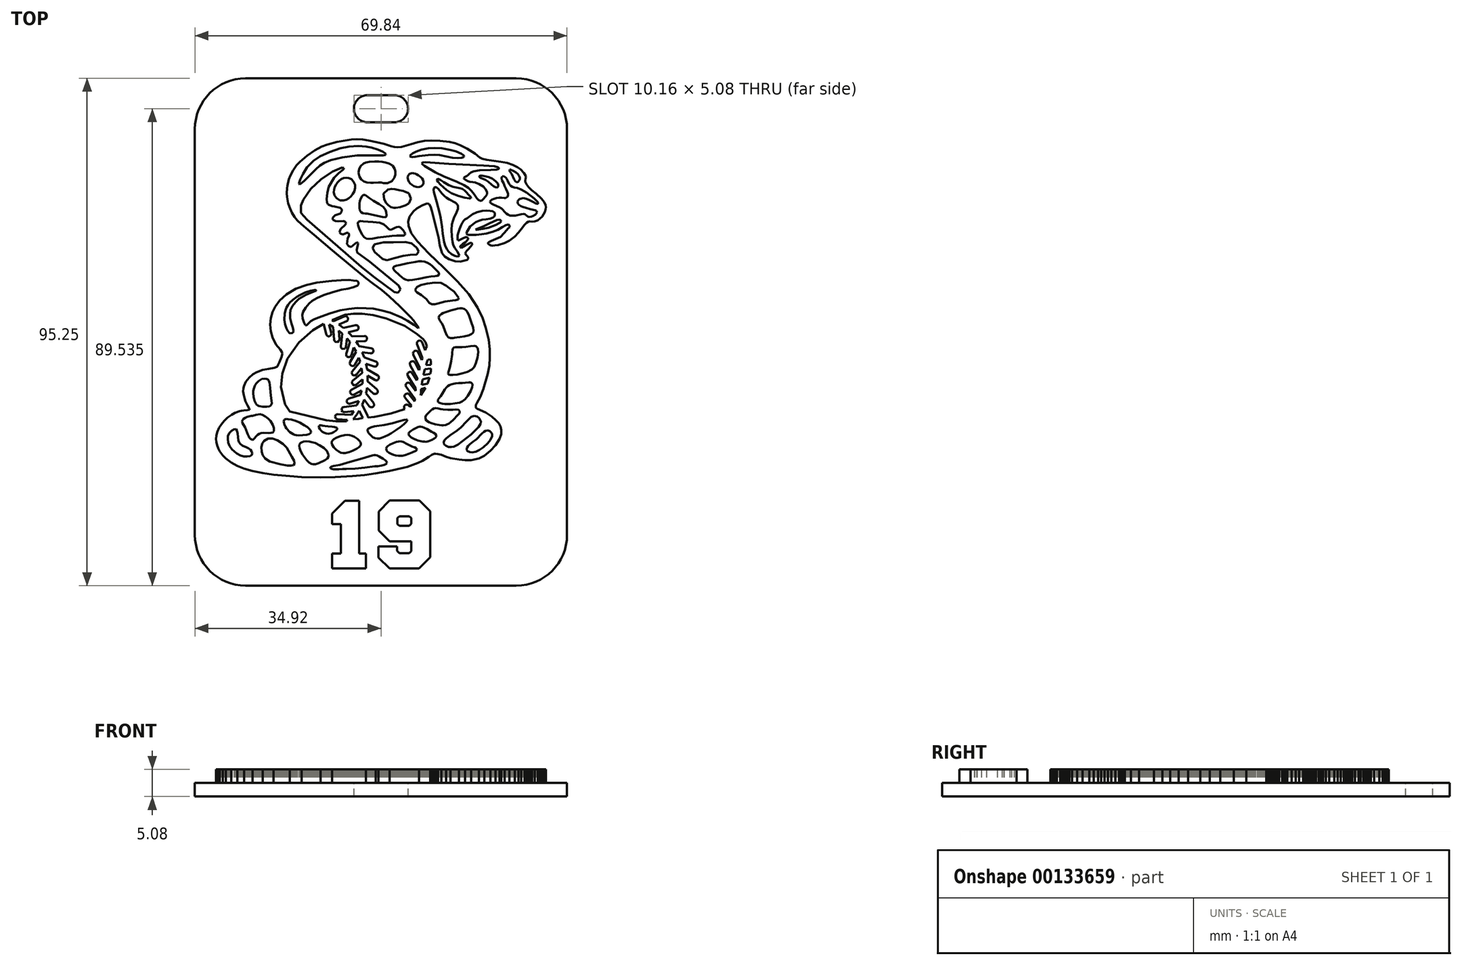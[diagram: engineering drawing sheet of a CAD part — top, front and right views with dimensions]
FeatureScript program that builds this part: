
annotation { "Feature Type Name" : "Feature", "Feature Type Description" : "" }
export const myFeature = defineFeature(function(context is Context, id is Id, definition is map)
    precondition{}
    {
        {
            var Q0;
            Q0=qCreatedBy(makeId("Top.planeOp"),FACE);
            var sketch = newSketch(context, id + "F0", { "sketchPlane" : qUnion([Q0])});
            skLineSegment(sketch, "E0", {"start": v(-10.1, 30.77) * mm, "end": v(-11.14, 30.36) * mm});
            skLineSegment(sketch, "E1", {"start": v(-11.14, 30.36) * mm, "end": v(-12.42, 29.65) * mm});
            skLineSegment(sketch, "E2", {"start": v(-12.42, 29.65) * mm, "end": v(-13.87, 28.65) * mm});
            skLineSegment(sketch, "E3", {"start": v(-13.87, 28.65) * mm, "end": v(-15.23, 27.49) * mm});
            skLineSegment(sketch, "E4", {"start": v(-15.23, 27.49) * mm, "end": v(-15.83, 26.85) * mm});
            skLineSegment(sketch, "E5", {"start": v(-15.83, 26.85) * mm, "end": v(-16.5, 25.91) * mm});
            skLineSegment(sketch, "E6", {"start": v(-16.5, 25.91) * mm, "end": v(-16.99, 24.99) * mm});
            skLineSegment(sketch, "E7", {"start": v(-16.99, 24.99) * mm, "end": v(-17.29, 24.2) * mm});
            skLineSegment(sketch, "E8", {"start": v(-17.29, 24.2) * mm, "end": v(-17.57, 23.01) * mm});
            skLineSegment(sketch, "E9", {"start": v(-17.57, 23.01) * mm, "end": v(-17.63, 22.55) * mm});
            skLineSegment(sketch, "E10", {"start": v(-17.63, 22.55) * mm, "end": v(-17.67, 21.62) * mm});
            skLineSegment(sketch, "E11", {"start": v(-17.67, 21.62) * mm, "end": v(-17.63, 20.87) * mm});
            skLineSegment(sketch, "E12", {"start": v(-17.63, 20.87) * mm, "end": v(-17.43, 19.76) * mm});
            skLineSegment(sketch, "E13", {"start": v(-17.43, 19.76) * mm, "end": v(-17.2, 19.03) * mm});
            skLineSegment(sketch, "E14", {"start": v(-17.2, 19.03) * mm, "end": v(-16.74, 17.98) * mm});
            skLineSegment(sketch, "E15", {"start": v(-16.74, 17.98) * mm, "end": v(-16.21, 17.14) * mm});
            skLineSegment(sketch, "E16", {"start": v(-16.21, 17.14) * mm, "end": v(-15.69, 16.5) * mm});
            skLineSegment(sketch, "E17", {"start": v(-15.69, 16.5) * mm, "end": v(-14.95, 15.79) * mm});
            skLineSegment(sketch, "E18", {"start": v(-14.95, 15.79) * mm, "end": v(-14.07, 15.06) * mm});
            skLineSegment(sketch, "E19", {"start": v(-14.07, 15.06) * mm, "end": v(-12.56, 13.8) * mm});
            skLineSegment(sketch, "E20", {"start": v(-12.56, 13.8) * mm, "end": v(-9.09, 10.85) * mm});
            skLineSegment(sketch, "E21", {"start": v(-9.09, 10.85) * mm, "end": v(-5.34, 7.75) * mm});
            skLineSegment(sketch, "E22", {"start": v(-5.34, 7.75) * mm, "end": v(-2.8, 5.63) * mm});
            skLineSegment(sketch, "E23", {"start": v(-2.8, 5.63) * mm, "end": v(-1.5, 4.63) * mm});
            skLineSegment(sketch, "E24", {"start": v(-1.5, 4.63) * mm, "end": v(0.14, 3.4) * mm});
            skLineSegment(sketch, "E25", {"start": v(0.14, 3.4) * mm, "end": v(1.56, 2.21) * mm});
            skLineSegment(sketch, "E26", {"start": v(1.56, 2.21) * mm, "end": v(3.52, 0.38) * mm});
            skLineSegment(sketch, "E27", {"start": v(3.52, 0.38) * mm, "end": v(5.55, -1.66) * mm});
            skLineSegment(sketch, "E28", {"start": v(5.55, -1.66) * mm, "end": v(6.1, -2.3) * mm});
            skLineSegment(sketch, "E29", {"start": v(6.1, -2.3) * mm, "end": v(6.85, -3.29) * mm});
            skLineSegment(sketch, "E30", {"start": v(6.85, -3.29) * mm, "end": v(7.08, -3.6) * mm});
            skLineSegment(sketch, "E31", {"start": v(7.08, -3.6) * mm, "end": v(7.04, -3.72) * mm});
            skLineSegment(sketch, "E32", {"start": v(7.04, -3.72) * mm, "end": v(6.17, -3.08) * mm});
            skLineSegment(sketch, "E33", {"start": v(6.17, -3.08) * mm, "end": v(5, -2.32) * mm});
            skLineSegment(sketch, "E34", {"start": v(5, -2.32) * mm, "end": v(3.8, -1.71) * mm});
            skLineSegment(sketch, "E35", {"start": v(3.8, -1.71) * mm, "end": v(1.73, -0.85) * mm});
            skLineSegment(sketch, "E36", {"start": v(1.73, -0.85) * mm, "end": v(0.03, -0.35) * mm});
            skLineSegment(sketch, "E37", {"start": v(0.03, -0.35) * mm, "end": v(-1.46, -0.09) * mm});
            skLineSegment(sketch, "E38", {"start": v(-1.46, -0.09) * mm, "end": v(-2.78, 0.03) * mm});
            skLineSegment(sketch, "E39", {"start": v(-2.78, 0.03) * mm, "end": v(-4.43, 0.04) * mm});
            skLineSegment(sketch, "E40", {"start": v(-4.43, 0.04) * mm, "end": v(-6.07, -0.1) * mm});
            skLineSegment(sketch, "E41", {"start": v(-6.07, -0.1) * mm, "end": v(-7.66, -0.38) * mm});
            skLineSegment(sketch, "E42", {"start": v(-7.66, -0.38) * mm, "end": v(-9.54, -0.94) * mm});
            skLineSegment(sketch, "E43", {"start": v(-9.54, -0.94) * mm, "end": v(-11.87, -1.75) * mm});
            skLineSegment(sketch, "E44", {"start": v(-11.87, -1.75) * mm, "end": v(-12.63, -2.07) * mm});
            skLineSegment(sketch, "E45", {"start": v(-12.63, -2.07) * mm, "end": v(-13.17, -2.43) * mm});
            skLineSegment(sketch, "E46", {"start": v(-13.17, -2.43) * mm, "end": v(-13.62, -2.86) * mm});
            skLineSegment(sketch, "E47", {"start": v(-13.62, -2.86) * mm, "end": v(-13.87, -3.09) * mm});
            skLineSegment(sketch, "E48", {"start": v(-13.87, -3.09) * mm, "end": v(-14.01, -3.2) * mm});
            skLineSegment(sketch, "E49", {"start": v(-14.01, -3.2) * mm, "end": v(-14.19, -3.17) * mm});
            skLineSegment(sketch, "E50", {"start": v(-14.19, -3.17) * mm, "end": v(-14.43, -2.69) * mm});
            skLineSegment(sketch, "E51", {"start": v(-14.43, -2.69) * mm, "end": v(-14.7, -1.9) * mm});
            skLineSegment(sketch, "E52", {"start": v(-14.7, -1.9) * mm, "end": v(-14.77, -1.3) * mm});
            skLineSegment(sketch, "E53", {"start": v(-14.77, -1.3) * mm, "end": v(-14.64, -0.72) * mm});
            skLineSegment(sketch, "E54", {"start": v(-14.64, -0.72) * mm, "end": v(-14.15, 0.15) * mm});
            skLineSegment(sketch, "E55", {"start": v(-14.15, 0.15) * mm, "end": v(-13.5, 0.87) * mm});
            skLineSegment(sketch, "E56", {"start": v(-13.5, 0.87) * mm, "end": v(-12.9, 1.37) * mm});
            skLineSegment(sketch, "E57", {"start": v(-12.9, 1.37) * mm, "end": v(-12.05, 1.9) * mm});
            skLineSegment(sketch, "E58", {"start": v(-12.05, 1.9) * mm, "end": v(-10.74, 2.5) * mm});
            skLineSegment(sketch, "E59", {"start": v(-10.74, 2.5) * mm, "end": v(-8.96, 3.08) * mm});
            skLineSegment(sketch, "E60", {"start": v(-8.96, 3.08) * mm, "end": v(-7.41, 3.49) * mm});
            skLineSegment(sketch, "E61", {"start": v(-7.41, 3.49) * mm, "end": v(-6.2, 3.72) * mm});
            skLineSegment(sketch, "E62", {"start": v(-6.2, 3.72) * mm, "end": v(-5.24, 3.9) * mm});
            skLineSegment(sketch, "E63", {"start": v(-5.24, 3.9) * mm, "end": v(-4.44, 4.24) * mm});
            skLineSegment(sketch, "E64", {"start": v(-4.44, 4.24) * mm, "end": v(-4.2, 4.53) * mm});
            skLineSegment(sketch, "E65", {"start": v(-4.2, 4.53) * mm, "end": v(-4.24, 4.9) * mm});
            skLineSegment(sketch, "E66", {"start": v(-4.24, 4.9) * mm, "end": v(-4.48, 5.15) * mm});
            skLineSegment(sketch, "E67", {"start": v(-4.48, 5.15) * mm, "end": v(-5.2, 5.22) * mm});
            skLineSegment(sketch, "E68", {"start": v(-5.2, 5.22) * mm, "end": v(-6.02, 5.3) * mm});
            skLineSegment(sketch, "E69", {"start": v(-6.02, 5.3) * mm, "end": v(-7.46, 5.25) * mm});
            skLineSegment(sketch, "E70", {"start": v(-7.46, 5.25) * mm, "end": v(-9.22, 5.17) * mm});
            skLineSegment(sketch, "E71", {"start": v(-9.22, 5.17) * mm, "end": v(-12.06, 4.86) * mm});
            skLineSegment(sketch, "E72", {"start": v(-12.06, 4.86) * mm, "end": v(-13.96, 4.42) * mm});
            skLineSegment(sketch, "E73", {"start": v(-13.96, 4.42) * mm, "end": v(-15.95, 3.67) * mm});
            skLineSegment(sketch, "E74", {"start": v(-15.95, 3.67) * mm, "end": v(-17.73, 2.62) * mm});
            skLineSegment(sketch, "E75", {"start": v(-17.73, 2.62) * mm, "end": v(-19.03, 1.44) * mm});
            skLineSegment(sketch, "E76", {"start": v(-19.03, 1.44) * mm, "end": v(-19.86, 0.31) * mm});
            skLineSegment(sketch, "E77", {"start": v(-19.86, 0.31) * mm, "end": v(-20.36, -0.72) * mm});
            skLineSegment(sketch, "E78", {"start": v(-20.36, -0.72) * mm, "end": v(-20.7, -1.85) * mm});
            skLineSegment(sketch, "E79", {"start": v(-20.7, -1.85) * mm, "end": v(-20.78, -3.05) * mm});
            skLineSegment(sketch, "E80", {"start": v(-20.78, -3.05) * mm, "end": v(-20.65, -4.3) * mm});
            skLineSegment(sketch, "E81", {"start": v(-20.65, -4.3) * mm, "end": v(-20.33, -5.49) * mm});
            skLineSegment(sketch, "E82", {"start": v(-20.33, -5.49) * mm, "end": v(-19.72, -6.82) * mm});
            skLineSegment(sketch, "E83", {"start": v(-19.72, -6.82) * mm, "end": v(-18.9, -7.76) * mm});
            skLineSegment(sketch, "E84", {"start": v(-18.9, -7.76) * mm, "end": v(-18.56, -8.24) * mm});
            skLineSegment(sketch, "E85", {"start": v(-18.56, -8.24) * mm, "end": v(-18.51, -8.5) * mm});
            skLineSegment(sketch, "E86", {"start": v(-18.51, -8.5) * mm, "end": v(-18.66, -9.08) * mm});
            skLineSegment(sketch, "E87", {"start": v(-18.66, -9.08) * mm, "end": v(-19.09, -10.16) * mm});
            skLineSegment(sketch, "E88", {"start": v(-19.09, -10.16) * mm, "end": v(-19.3, -10.64) * mm});
            skLineSegment(sketch, "E89", {"start": v(-19.3, -10.64) * mm, "end": v(-19.4, -10.82) * mm});
            skLineSegment(sketch, "E90", {"start": v(-19.4, -10.82) * mm, "end": v(-19.52, -10.97) * mm});
            skLineSegment(sketch, "E91", {"start": v(-19.52, -10.97) * mm, "end": v(-20.02, -11.19) * mm});
            skLineSegment(sketch, "E92", {"start": v(-20.02, -11.19) * mm, "end": v(-21.07, -11.38) * mm});
            skLineSegment(sketch, "E93", {"start": v(-21.07, -11.38) * mm, "end": v(-22.22, -11.58) * mm});
            skLineSegment(sketch, "E94", {"start": v(-22.22, -11.58) * mm, "end": v(-23.33, -12) * mm});
            skLineSegment(sketch, "E95", {"start": v(-23.33, -12) * mm, "end": v(-24.01, -12.39) * mm});
            skLineSegment(sketch, "E96", {"start": v(-24.01, -12.39) * mm, "end": v(-24.76, -13.01) * mm});
            skLineSegment(sketch, "E97", {"start": v(-24.76, -13.01) * mm, "end": v(-25.35, -13.79) * mm});
            skLineSegment(sketch, "E98", {"start": v(-25.35, -13.79) * mm, "end": v(-25.69, -14.52) * mm});
            skLineSegment(sketch, "E99", {"start": v(-25.69, -14.52) * mm, "end": v(-25.81, -15) * mm});
            skLineSegment(sketch, "E100", {"start": v(-25.81, -15) * mm, "end": v(-25.85, -15.6) * mm});
            skLineSegment(sketch, "E101", {"start": v(-25.85, -15.6) * mm, "end": v(-25.76, -16.27) * mm});
            skLineSegment(sketch, "E102", {"start": v(-25.76, -16.27) * mm, "end": v(-25.55, -17.04) * mm});
            skLineSegment(sketch, "E103", {"start": v(-25.55, -17.04) * mm, "end": v(-25.42, -17.43) * mm});
            skLineSegment(sketch, "E104", {"start": v(-25.42, -17.43) * mm, "end": v(-25.06, -18.22) * mm});
            skLineSegment(sketch, "E105", {"start": v(-25.06, -18.22) * mm, "end": v(-24.72, -18.77) * mm});
            skLineSegment(sketch, "E106", {"start": v(-24.72, -18.77) * mm, "end": v(-24.67, -18.86) * mm});
            skLineSegment(sketch, "E107", {"start": v(-24.67, -18.86) * mm, "end": v(-24.69, -19.05) * mm});
            skLineSegment(sketch, "E108", {"start": v(-24.69, -19.05) * mm, "end": v(-25.03, -19.14) * mm});
            skLineSegment(sketch, "E109", {"start": v(-25.03, -19.14) * mm, "end": v(-25.72, -19.19) * mm});
            skLineSegment(sketch, "E110", {"start": v(-25.72, -19.19) * mm, "end": v(-26.18, -19.21) * mm});
            skLineSegment(sketch, "E111", {"start": v(-26.18, -19.21) * mm, "end": v(-26.54, -19.27) * mm});
            skLineSegment(sketch, "E112", {"start": v(-26.54, -19.27) * mm, "end": v(-27.37, -19.6) * mm});
            skLineSegment(sketch, "E113", {"start": v(-27.37, -19.6) * mm, "end": v(-28.02, -19.97) * mm});
            skLineSegment(sketch, "E114", {"start": v(-28.02, -19.97) * mm, "end": v(-28.8, -20.53) * mm});
            skLineSegment(sketch, "E115", {"start": v(-28.8, -20.53) * mm, "end": v(-29.42, -21.11) * mm});
            skLineSegment(sketch, "E116", {"start": v(-29.42, -21.11) * mm, "end": v(-29.97, -21.78) * mm});
            skLineSegment(sketch, "E117", {"start": v(-29.97, -21.78) * mm, "end": v(-30.37, -22.42) * mm});
            skLineSegment(sketch, "E118", {"start": v(-30.37, -22.42) * mm, "end": v(-30.7, -23.18) * mm});
            skLineSegment(sketch, "E119", {"start": v(-30.7, -23.18) * mm, "end": v(-30.88, -23.9) * mm});
            skLineSegment(sketch, "E120", {"start": v(-30.88, -23.9) * mm, "end": v(-30.92, -24.55) * mm});
            skLineSegment(sketch, "E121", {"start": v(-30.92, -24.55) * mm, "end": v(-30.88, -25.11) * mm});
            skLineSegment(sketch, "E122", {"start": v(-30.88, -25.11) * mm, "end": v(-30.75, -25.67) * mm});
            skLineSegment(sketch, "E123", {"start": v(-30.75, -25.67) * mm, "end": v(-30.49, -26.36) * mm});
            skLineSegment(sketch, "E124", {"start": v(-30.49, -26.36) * mm, "end": v(-30.24, -26.84) * mm});
            skLineSegment(sketch, "E125", {"start": v(-30.24, -26.84) * mm, "end": v(-29.66, -27.63) * mm});
            skLineSegment(sketch, "E126", {"start": v(-29.66, -27.63) * mm, "end": v(-29.09, -28.2) * mm});
            skLineSegment(sketch, "E127", {"start": v(-29.09, -28.2) * mm, "end": v(-28.13, -28.92) * mm});
            skLineSegment(sketch, "E128", {"start": v(-28.13, -28.92) * mm, "end": v(-26.96, -29.56) * mm});
            skLineSegment(sketch, "E129", {"start": v(-26.96, -29.56) * mm, "end": v(-25.69, -30.07) * mm});
            skLineSegment(sketch, "E130", {"start": v(-25.69, -30.07) * mm, "end": v(-24.07, -30.55) * mm});
            skLineSegment(sketch, "E131", {"start": v(-24.07, -30.55) * mm, "end": v(-22.17, -30.94) * mm});
            skLineSegment(sketch, "E132", {"start": v(-22.17, -30.94) * mm, "end": v(-20.14, -31.23) * mm});
            skLineSegment(sketch, "E133", {"start": v(-20.14, -31.23) * mm, "end": v(-17.14, -31.51) * mm});
            skLineSegment(sketch, "E134", {"start": v(-17.14, -31.51) * mm, "end": v(-14.9, -31.65) * mm});
            skLineSegment(sketch, "E135", {"start": v(-14.9, -31.65) * mm, "end": v(-11.3, -31.75) * mm});
            skLineSegment(sketch, "E136", {"start": v(-11.3, -31.75) * mm, "end": v(-8.64, -31.7) * mm});
            skLineSegment(sketch, "E137", {"start": v(-8.64, -31.7) * mm, "end": v(-5.36, -31.52) * mm});
            skLineSegment(sketch, "E138", {"start": v(-5.36, -31.52) * mm, "end": v(-3.11, -31.3) * mm});
            skLineSegment(sketch, "E139", {"start": v(-3.11, -31.3) * mm, "end": v(-0.98, -31) * mm});
            skLineSegment(sketch, "E140", {"start": v(-0.98, -31) * mm, "end": v(1.54, -30.56) * mm});
            skLineSegment(sketch, "E141", {"start": v(1.54, -30.56) * mm, "end": v(4.34, -29.93) * mm});
            skLineSegment(sketch, "E142", {"start": v(4.34, -29.93) * mm, "end": v(4.94, -29.76) * mm});
            skLineSegment(sketch, "E143", {"start": v(4.94, -29.76) * mm, "end": v(5.94, -29.42) * mm});
            skLineSegment(sketch, "E144", {"start": v(5.94, -29.42) * mm, "end": v(6.92, -29.03) * mm});
            skLineSegment(sketch, "E145", {"start": v(6.92, -29.03) * mm, "end": v(7.77, -28.62) * mm});
            skLineSegment(sketch, "E146", {"start": v(7.77, -28.62) * mm, "end": v(8.27, -28.33) * mm});
            skLineSegment(sketch, "E147", {"start": v(8.27, -28.33) * mm, "end": v(8.98, -27.85) * mm});
            skLineSegment(sketch, "E148", {"start": v(8.98, -27.85) * mm, "end": v(9.53, -27.5) * mm});
            skLineSegment(sketch, "E149", {"start": v(9.53, -27.5) * mm, "end": v(9.97, -27.33) * mm});
            skLineSegment(sketch, "E150", {"start": v(9.97, -27.33) * mm, "end": v(10.23, -27.3) * mm});
            skLineSegment(sketch, "E151", {"start": v(10.23, -27.3) * mm, "end": v(10.7, -27.34) * mm});
            skLineSegment(sketch, "E152", {"start": v(10.7, -27.34) * mm, "end": v(11.31, -27.51) * mm});
            skLineSegment(sketch, "E153", {"start": v(11.31, -27.51) * mm, "end": v(12.22, -27.85) * mm});
            skLineSegment(sketch, "E154", {"start": v(12.22, -27.85) * mm, "end": v(13.04, -28.1) * mm});
            skLineSegment(sketch, "E155", {"start": v(13.04, -28.1) * mm, "end": v(14.63, -28.4) * mm});
            skLineSegment(sketch, "E156", {"start": v(14.63, -28.4) * mm, "end": v(15.79, -28.5) * mm});
            skLineSegment(sketch, "E157", {"start": v(15.79, -28.5) * mm, "end": v(16.93, -28.5) * mm});
            skLineSegment(sketch, "E158", {"start": v(16.93, -28.5) * mm, "end": v(18.37, -28.2) * mm});
            skLineSegment(sketch, "E159", {"start": v(18.37, -28.2) * mm, "end": v(19.37, -27.7) * mm});
            skLineSegment(sketch, "E160", {"start": v(19.37, -27.7) * mm, "end": v(20.57, -26.75) * mm});
            skLineSegment(sketch, "E161", {"start": v(20.57, -26.75) * mm, "end": v(21.5, -25.71) * mm});
            skLineSegment(sketch, "E162", {"start": v(21.5, -25.71) * mm, "end": v(22.25, -24.49) * mm});
            skLineSegment(sketch, "E163", {"start": v(22.25, -24.49) * mm, "end": v(22.55, -23.6) * mm});
            skLineSegment(sketch, "E164", {"start": v(22.55, -23.6) * mm, "end": v(22.6, -22.83) * mm});
            skLineSegment(sketch, "E165", {"start": v(22.6, -22.83) * mm, "end": v(22.45, -22.24) * mm});
            skLineSegment(sketch, "E166", {"start": v(22.45, -22.24) * mm, "end": v(22.1, -21.61) * mm});
            skLineSegment(sketch, "E167", {"start": v(22.1, -21.61) * mm, "end": v(21.57, -20.98) * mm});
            skLineSegment(sketch, "E168", {"start": v(21.57, -20.98) * mm, "end": v(20.8, -20.33) * mm});
            skLineSegment(sketch, "E169", {"start": v(20.8, -20.33) * mm, "end": v(19.63, -19.59) * mm});
            skLineSegment(sketch, "E170", {"start": v(19.63, -19.59) * mm, "end": v(18.08, -18.84) * mm});
            skLineSegment(sketch, "E171", {"start": v(18.08, -18.84) * mm, "end": v(17.83, -18.64) * mm});
            skLineSegment(sketch, "E172", {"start": v(17.83, -18.64) * mm, "end": v(17.78, -18.47) * mm});
            skLineSegment(sketch, "E173", {"start": v(17.78, -18.47) * mm, "end": v(17.83, -18.19) * mm});
            skLineSegment(sketch, "E174", {"start": v(17.83, -18.19) * mm, "end": v(17.99, -17.78) * mm});
            skLineSegment(sketch, "E175", {"start": v(17.99, -17.78) * mm, "end": v(18.65, -16.64) * mm});
            skLineSegment(sketch, "E176", {"start": v(18.65, -16.64) * mm, "end": v(19.22, -15.14) * mm});
            skLineSegment(sketch, "E177", {"start": v(19.22, -15.14) * mm, "end": v(20.06, -12.34) * mm});
            skLineSegment(sketch, "E178", {"start": v(20.06, -12.34) * mm, "end": v(20.34, -10.72) * mm});
            skLineSegment(sketch, "E179", {"start": v(20.34, -10.72) * mm, "end": v(20.43, -9.25) * mm});
            skLineSegment(sketch, "E180", {"start": v(20.43, -9.25) * mm, "end": v(20.4, -7.7) * mm});
            skLineSegment(sketch, "E181", {"start": v(20.4, -7.7) * mm, "end": v(20.2, -5.91) * mm});
            skLineSegment(sketch, "E182", {"start": v(20.2, -5.91) * mm, "end": v(19.68, -3.6) * mm});
            skLineSegment(sketch, "E183", {"start": v(19.68, -3.6) * mm, "end": v(19.05, -1.83) * mm});
            skLineSegment(sketch, "E184", {"start": v(19.05, -1.83) * mm, "end": v(18.12, 0.13) * mm});
            skLineSegment(sketch, "E185", {"start": v(18.12, 0.13) * mm, "end": v(16.49, 2.65) * mm});
            skLineSegment(sketch, "E186", {"start": v(16.49, 2.65) * mm, "end": v(14.4, 5.04) * mm});
            skLineSegment(sketch, "E187", {"start": v(14.4, 5.04) * mm, "end": v(11.78, 7.6) * mm});
            skLineSegment(sketch, "E188", {"start": v(11.78, 7.6) * mm, "end": v(8.99, 10.27) * mm});
            skLineSegment(sketch, "E189", {"start": v(8.99, 10.27) * mm, "end": v(6.8, 12.55) * mm});
            skLineSegment(sketch, "E190", {"start": v(6.8, 12.55) * mm, "end": v(5.7, 14.13) * mm});
            skLineSegment(sketch, "E191", {"start": v(5.7, 14.13) * mm, "end": v(5.18, 15.52) * mm});
            skLineSegment(sketch, "E192", {"start": v(5.18, 15.52) * mm, "end": v(5.13, 16.34) * mm});
            skLineSegment(sketch, "E193", {"start": v(5.13, 16.34) * mm, "end": v(5.35, 17.23) * mm});
            skLineSegment(sketch, "E194", {"start": v(5.35, 17.23) * mm, "end": v(6.03, 18.19) * mm});
            skLineSegment(sketch, "E195", {"start": v(6.03, 18.19) * mm, "end": v(6.72, 18.7) * mm});
            skLineSegment(sketch, "E196", {"start": v(6.72, 18.7) * mm, "end": v(7.74, 19.32) * mm});
            skLineSegment(sketch, "E197", {"start": v(7.74, 19.32) * mm, "end": v(8.48, 19.62) * mm});
            skLineSegment(sketch, "E198", {"start": v(8.48, 19.62) * mm, "end": v(8.75, 19.66) * mm});
            skLineSegment(sketch, "E199", {"start": v(8.75, 19.66) * mm, "end": v(9.05, 19.53) * mm});
            skLineSegment(sketch, "E200", {"start": v(9.05, 19.53) * mm, "end": v(9.3, 19.15) * mm});
            skLineSegment(sketch, "E201", {"start": v(9.3, 19.15) * mm, "end": v(9.58, 18.26) * mm});
            skLineSegment(sketch, "E202", {"start": v(9.58, 18.26) * mm, "end": v(9.87, 17) * mm});
            skLineSegment(sketch, "E203", {"start": v(9.87, 17) * mm, "end": v(10.83, 13.19) * mm});
            skLineSegment(sketch, "E204", {"start": v(10.83, 13.19) * mm, "end": v(11.04, 11.88) * mm});
            skLineSegment(sketch, "E205", {"start": v(11.04, 11.88) * mm, "end": v(11.47, 10.33) * mm});
            skLineSegment(sketch, "E206", {"start": v(11.47, 10.33) * mm, "end": v(11.96, 9.74) * mm});
            skLineSegment(sketch, "E207", {"start": v(11.96, 9.74) * mm, "end": v(12.8, 9.2) * mm});
            skLineSegment(sketch, "E208", {"start": v(12.8, 9.2) * mm, "end": v(13.95, 8.86) * mm});
            skLineSegment(sketch, "E209", {"start": v(13.95, 8.86) * mm, "end": v(14.91, 8.78) * mm});
            skLineSegment(sketch, "E210", {"start": v(14.91, 8.78) * mm, "end": v(16.17, 9.08) * mm});
            skLineSegment(sketch, "E211", {"start": v(16.17, 9.08) * mm, "end": v(16.35, 9.29) * mm});
            skLineSegment(sketch, "E212", {"start": v(16.35, 9.29) * mm, "end": v(16.37, 9.51) * mm});
            skLineSegment(sketch, "E213", {"start": v(16.37, 9.51) * mm, "end": v(16.22, 9.76) * mm});
            skLineSegment(sketch, "E214", {"start": v(16.22, 9.76) * mm, "end": v(15.9, 10.1) * mm});
            skLineSegment(sketch, "E215", {"start": v(15.9, 10.1) * mm, "end": v(15.84, 10.28) * mm});
            skLineSegment(sketch, "E216", {"start": v(15.84, 10.28) * mm, "end": v(15.9, 10.53) * mm});
            skLineSegment(sketch, "E217", {"start": v(15.9, 10.53) * mm, "end": v(16.07, 10.78) * mm});
            skLineSegment(sketch, "E218", {"start": v(16.07, 10.78) * mm, "end": v(16.4, 11.14) * mm});
            skLineSegment(sketch, "E219", {"start": v(16.4, 11.14) * mm, "end": v(17.1, 11.95) * mm});
            skLineSegment(sketch, "E220", {"start": v(17.1, 11.95) * mm, "end": v(17.05, 12.3) * mm});
            skLineSegment(sketch, "E221", {"start": v(17.05, 12.3) * mm, "end": v(16.73, 12.28) * mm});
            skLineSegment(sketch, "E222", {"start": v(16.73, 12.28) * mm, "end": v(15.82, 11.78) * mm});
            skLineSegment(sketch, "E223", {"start": v(15.82, 11.78) * mm, "end": v(15.1, 11.35) * mm});
            skLineSegment(sketch, "E224", {"start": v(15.1, 11.35) * mm, "end": v(14.9, 11.43) * mm});
            skLineSegment(sketch, "E225", {"start": v(14.9, 11.43) * mm, "end": v(14.91, 11.67) * mm});
            skLineSegment(sketch, "E226", {"start": v(14.91, 11.67) * mm, "end": v(15.36, 12.07) * mm});
            skLineSegment(sketch, "E227", {"start": v(15.36, 12.07) * mm, "end": v(15.82, 12.39) * mm});
            skLineSegment(sketch, "E228", {"start": v(15.82, 12.39) * mm, "end": v(16.33, 12.93) * mm});
            skLineSegment(sketch, "E229", {"start": v(16.33, 12.93) * mm, "end": v(16.37, 13.23) * mm});
            skLineSegment(sketch, "E230", {"start": v(16.37, 13.23) * mm, "end": v(16, 13.37) * mm});
            skLineSegment(sketch, "E231", {"start": v(16, 13.37) * mm, "end": v(15.3, 13.1) * mm});
            skLineSegment(sketch, "E232", {"start": v(15.3, 13.1) * mm, "end": v(14.67, 12.8) * mm});
            skLineSegment(sketch, "E233", {"start": v(14.67, 12.8) * mm, "end": v(14.44, 12.75) * mm});
            skLineSegment(sketch, "E234", {"start": v(14.44, 12.75) * mm, "end": v(14.39, 12.9) * mm});
            skLineSegment(sketch, "E235", {"start": v(14.39, 12.9) * mm, "end": v(14.36, 13.15) * mm});
            skLineSegment(sketch, "E236", {"start": v(14.36, 13.15) * mm, "end": v(14.35, 13.48) * mm});
            skLineSegment(sketch, "E237", {"start": v(14.35, 13.48) * mm, "end": v(14.41, 13.72) * mm});
            skLineSegment(sketch, "E238", {"start": v(14.41, 13.72) * mm, "end": v(14.5, 14.16) * mm});
            skLineSegment(sketch, "E239", {"start": v(14.5, 14.16) * mm, "end": v(14.78, 14.91) * mm});
            skLineSegment(sketch, "E240", {"start": v(14.78, 14.91) * mm, "end": v(15.03, 15.57) * mm});
            skLineSegment(sketch, "E241", {"start": v(15.03, 15.57) * mm, "end": v(15.3, 16.1) * mm});
            skLineSegment(sketch, "E242", {"start": v(15.3, 16.1) * mm, "end": v(15.54, 16.45) * mm});
            skLineSegment(sketch, "E243", {"start": v(15.54, 16.45) * mm, "end": v(15.78, 16.68) * mm});
            skLineSegment(sketch, "E244", {"start": v(15.78, 16.68) * mm, "end": v(16.13, 16.9) * mm});
            skLineSegment(sketch, "E245", {"start": v(16.13, 16.9) * mm, "end": v(17.15, 17.65) * mm});
            skLineSegment(sketch, "E246", {"start": v(17.15, 17.65) * mm, "end": v(18, 18.02) * mm});
            skLineSegment(sketch, "E247", {"start": v(18, 18.02) * mm, "end": v(19, 18.29) * mm});
            skLineSegment(sketch, "E248", {"start": v(19, 18.29) * mm, "end": v(19.76, 18.35) * mm});
            skLineSegment(sketch, "E249", {"start": v(19.76, 18.35) * mm, "end": v(20.45, 18.3) * mm});
            skLineSegment(sketch, "E250", {"start": v(20.45, 18.3) * mm, "end": v(21.02, 18.2) * mm});
            skLineSegment(sketch, "E251", {"start": v(21.02, 18.2) * mm, "end": v(21.35, 17.9) * mm});
            skLineSegment(sketch, "E252", {"start": v(21.35, 17.9) * mm, "end": v(21.37, 17.62) * mm});
            skLineSegment(sketch, "E253", {"start": v(21.37, 17.62) * mm, "end": v(21.28, 17.3) * mm});
            skLineSegment(sketch, "E254", {"start": v(21.28, 17.3) * mm, "end": v(21, 17) * mm});
            skLineSegment(sketch, "E255", {"start": v(21, 17) * mm, "end": v(20.48, 16.83) * mm});
            skLineSegment(sketch, "E256", {"start": v(20.48, 16.83) * mm, "end": v(19.7, 16.7) * mm});
            skLineSegment(sketch, "E257", {"start": v(19.7, 16.7) * mm, "end": v(19.01, 16.63) * mm});
            skLineSegment(sketch, "E258", {"start": v(19.01, 16.63) * mm, "end": v(18.42, 16.45) * mm});
            skLineSegment(sketch, "E259", {"start": v(18.42, 16.45) * mm, "end": v(17.78, 16.2) * mm});
            skLineSegment(sketch, "E260", {"start": v(17.78, 16.2) * mm, "end": v(16.75, 15.4) * mm});
            skLineSegment(sketch, "E261", {"start": v(16.75, 15.4) * mm, "end": v(16.3, 14.61) * mm});
            skLineSegment(sketch, "E262", {"start": v(16.3, 14.61) * mm, "end": v(16.08, 14.3) * mm});
            skLineSegment(sketch, "E263", {"start": v(16.08, 14.3) * mm, "end": v(16.06, 14.05) * mm});
            skLineSegment(sketch, "E264", {"start": v(16.06, 14.05) * mm, "end": v(16.14, 13.94) * mm});
            skLineSegment(sketch, "E265", {"start": v(16.14, 13.94) * mm, "end": v(16.27, 13.86) * mm});
            skLineSegment(sketch, "E266", {"start": v(16.27, 13.86) * mm, "end": v(16.45, 13.81) * mm});
            skLineSegment(sketch, "E267", {"start": v(16.45, 13.81) * mm, "end": v(16.87, 13.78) * mm});
            skLineSegment(sketch, "E268", {"start": v(16.87, 13.78) * mm, "end": v(17.88, 13.81) * mm});
            skLineSegment(sketch, "E269", {"start": v(17.88, 13.81) * mm, "end": v(18.92, 13.9) * mm});
            skLineSegment(sketch, "E270", {"start": v(18.92, 13.9) * mm, "end": v(19.8, 14.06) * mm});
            skLineSegment(sketch, "E271", {"start": v(19.8, 14.06) * mm, "end": v(20.9, 14.37) * mm});
            skLineSegment(sketch, "E272", {"start": v(20.9, 14.37) * mm, "end": v(21.95, 14.77) * mm});
            skLineSegment(sketch, "E273", {"start": v(21.95, 14.77) * mm, "end": v(22.77, 15.23) * mm});
            skLineSegment(sketch, "E274", {"start": v(22.77, 15.23) * mm, "end": v(23.44, 15.63) * mm});
            skLineSegment(sketch, "E275", {"start": v(23.44, 15.63) * mm, "end": v(23.7, 15.69) * mm});
            skLineSegment(sketch, "E276", {"start": v(23.7, 15.69) * mm, "end": v(23.96, 15.73) * mm});
            skLineSegment(sketch, "E277", {"start": v(23.96, 15.73) * mm, "end": v(24.11, 15.56) * mm});
            skLineSegment(sketch, "E278", {"start": v(24.11, 15.56) * mm, "end": v(24.14, 15.26) * mm});
            skLineSegment(sketch, "E279", {"start": v(24.14, 15.26) * mm, "end": v(23.86, 14.97) * mm});
            skLineSegment(sketch, "E280", {"start": v(23.86, 14.97) * mm, "end": v(23.6, 14.66) * mm});
            skLineSegment(sketch, "E281", {"start": v(23.6, 14.66) * mm, "end": v(23.11, 14.1) * mm});
            skLineSegment(sketch, "E282", {"start": v(23.11, 14.1) * mm, "end": v(22.45, 13.4) * mm});
            skLineSegment(sketch, "E283", {"start": v(22.45, 13.4) * mm, "end": v(21.59, 13.03) * mm});
            skLineSegment(sketch, "E284", {"start": v(21.59, 13.03) * mm, "end": v(20.67, 12.61) * mm});
            skLineSegment(sketch, "E285", {"start": v(20.67, 12.61) * mm, "end": v(20.27, 12.45) * mm});
            skLineSegment(sketch, "E286", {"start": v(20.27, 12.45) * mm, "end": v(20.13, 12.32) * mm});
            skLineSegment(sketch, "E287", {"start": v(20.13, 12.32) * mm, "end": v(20.12, 12.1) * mm});
            skLineSegment(sketch, "E288", {"start": v(20.12, 12.1) * mm, "end": v(20.32, 11.95) * mm});
            skLineSegment(sketch, "E289", {"start": v(20.32, 11.95) * mm, "end": v(20.62, 11.79) * mm});
            skLineSegment(sketch, "E290", {"start": v(20.62, 11.79) * mm, "end": v(20.95, 11.75) * mm});
            skLineSegment(sketch, "E291", {"start": v(20.95, 11.75) * mm, "end": v(21.36, 11.79) * mm});
            skLineSegment(sketch, "E292", {"start": v(21.36, 11.79) * mm, "end": v(22.01, 11.88) * mm});
            skLineSegment(sketch, "E293", {"start": v(22.01, 11.88) * mm, "end": v(23.19, 12.28) * mm});
            skLineSegment(sketch, "E294", {"start": v(23.19, 12.28) * mm, "end": v(24.09, 12.72) * mm});
            skLineSegment(sketch, "E295", {"start": v(24.09, 12.72) * mm, "end": v(25.1, 13.5) * mm});
            skLineSegment(sketch, "E296", {"start": v(25.1, 13.5) * mm, "end": v(25.82, 14.26) * mm});
            skLineSegment(sketch, "E297", {"start": v(25.82, 14.26) * mm, "end": v(26.29, 14.89) * mm});
            skLineSegment(sketch, "E298", {"start": v(26.29, 14.89) * mm, "end": v(26.96, 15.68) * mm});
            skLineSegment(sketch, "E299", {"start": v(26.96, 15.68) * mm, "end": v(27.32, 16.05) * mm});
            skLineSegment(sketch, "E300", {"start": v(27.32, 16.05) * mm, "end": v(27.64, 16.25) * mm});
            skLineSegment(sketch, "E301", {"start": v(27.64, 16.25) * mm, "end": v(27.93, 16.3) * mm});
            skLineSegment(sketch, "E302", {"start": v(27.93, 16.3) * mm, "end": v(28.36, 16.29) * mm});
            skLineSegment(sketch, "E303", {"start": v(28.36, 16.29) * mm, "end": v(28.87, 16.33) * mm});
            skLineSegment(sketch, "E304", {"start": v(28.87, 16.33) * mm, "end": v(29.43, 16.55) * mm});
            skLineSegment(sketch, "E305", {"start": v(29.43, 16.55) * mm, "end": v(29.9, 16.88) * mm});
            skLineSegment(sketch, "E306", {"start": v(29.9, 16.88) * mm, "end": v(30.23, 17.24) * mm});
            skLineSegment(sketch, "E307", {"start": v(30.23, 17.24) * mm, "end": v(30.51, 17.65) * mm});
            skLineSegment(sketch, "E308", {"start": v(30.51, 17.65) * mm, "end": v(30.74, 18.1) * mm});
            skLineSegment(sketch, "E309", {"start": v(30.74, 18.1) * mm, "end": v(30.89, 18.6) * mm});
            skLineSegment(sketch, "E310", {"start": v(30.89, 18.6) * mm, "end": v(30.92, 18.97) * mm});
            skLineSegment(sketch, "E311", {"start": v(30.92, 18.97) * mm, "end": v(30.87, 19.4) * mm});
            skLineSegment(sketch, "E312", {"start": v(30.87, 19.4) * mm, "end": v(30.65, 19.92) * mm});
            skLineSegment(sketch, "E313", {"start": v(30.65, 19.92) * mm, "end": v(30.14, 20.57) * mm});
            skLineSegment(sketch, "E314", {"start": v(30.14, 20.57) * mm, "end": v(29.09, 21.5) * mm});
            skLineSegment(sketch, "E315", {"start": v(29.09, 21.5) * mm, "end": v(28.3, 22.17) * mm});
            skLineSegment(sketch, "E316", {"start": v(28.3, 22.17) * mm, "end": v(27.7, 22.76) * mm});
            skLineSegment(sketch, "E317", {"start": v(27.7, 22.76) * mm, "end": v(27.31, 23.27) * mm});
            skLineSegment(sketch, "E318", {"start": v(27.31, 23.27) * mm, "end": v(27.07, 23.76) * mm});
            skLineSegment(sketch, "E319", {"start": v(27.07, 23.76) * mm, "end": v(27.05, 24.02) * mm});
            skLineSegment(sketch, "E320", {"start": v(27.05, 24.02) * mm, "end": v(27.13, 24.37) * mm});
            skLineSegment(sketch, "E321", {"start": v(27.13, 24.37) * mm, "end": v(27.18, 24.63) * mm});
            skLineSegment(sketch, "E322", {"start": v(27.18, 24.63) * mm, "end": v(27.12, 24.89) * mm});
            skLineSegment(sketch, "E323", {"start": v(27.12, 24.89) * mm, "end": v(26.83, 25.39) * mm});
            skLineSegment(sketch, "E324", {"start": v(26.83, 25.39) * mm, "end": v(26.21, 26.07) * mm});
            skLineSegment(sketch, "E325", {"start": v(26.21, 26.07) * mm, "end": v(25.63, 26.5) * mm});
            skLineSegment(sketch, "E326", {"start": v(25.63, 26.5) * mm, "end": v(24.72, 26.95) * mm});
            skLineSegment(sketch, "E327", {"start": v(24.72, 26.95) * mm, "end": v(23.63, 27.29) * mm});
            skLineSegment(sketch, "E328", {"start": v(23.63, 27.29) * mm, "end": v(22.48, 27.52) * mm});
            skLineSegment(sketch, "E329", {"start": v(22.48, 27.52) * mm, "end": v(19.85, 27.9) * mm});
            skLineSegment(sketch, "E330", {"start": v(19.85, 27.9) * mm, "end": v(19.02, 28.09) * mm});
            skLineSegment(sketch, "E331", {"start": v(19.02, 28.09) * mm, "end": v(18.49, 28.35) * mm});
            skLineSegment(sketch, "E332", {"start": v(18.49, 28.35) * mm, "end": v(17.66, 29) * mm});
            skLineSegment(sketch, "E333", {"start": v(17.66, 29) * mm, "end": v(16.13, 29.96) * mm});
            skLineSegment(sketch, "E334", {"start": v(16.13, 29.96) * mm, "end": v(14.89, 30.6) * mm});
            skLineSegment(sketch, "E335", {"start": v(14.89, 30.6) * mm, "end": v(13.9, 31) * mm});
            skLineSegment(sketch, "E336", {"start": v(13.9, 31) * mm, "end": v(12.85, 31.24) * mm});
            skLineSegment(sketch, "E337", {"start": v(12.85, 31.24) * mm, "end": v(11.05, 31.43) * mm});
            skLineSegment(sketch, "E338", {"start": v(11.05, 31.43) * mm, "end": v(9.43, 31.52) * mm});
            skLineSegment(sketch, "E339", {"start": v(9.43, 31.52) * mm, "end": v(8.17, 31.46) * mm});
            skLineSegment(sketch, "E340", {"start": v(8.17, 31.46) * mm, "end": v(6.88, 31.2) * mm});
            skLineSegment(sketch, "E341", {"start": v(6.88, 31.2) * mm, "end": v(5.6, 30.8) * mm});
            skLineSegment(sketch, "E342", {"start": v(5.6, 30.8) * mm, "end": v(3.82, 30.32) * mm});
            skLineSegment(sketch, "E343", {"start": v(3.82, 30.32) * mm, "end": v(3.05, 30.23) * mm});
            skLineSegment(sketch, "E344", {"start": v(3.05, 30.23) * mm, "end": v(2.5, 30.27) * mm});
            skLineSegment(sketch, "E345", {"start": v(2.5, 30.27) * mm, "end": v(1.92, 30.42) * mm});
            skLineSegment(sketch, "E346", {"start": v(1.92, 30.42) * mm, "end": v(0.59, 30.87) * mm});
            skLineSegment(sketch, "E347", {"start": v(0.59, 30.87) * mm, "end": v(-0.8, 31.2) * mm});
            skLineSegment(sketch, "E348", {"start": v(-0.8, 31.2) * mm, "end": v(-2.34, 31.52) * mm});
            skLineSegment(sketch, "E349", {"start": v(-2.34, 31.52) * mm, "end": v(-3.4, 31.67) * mm});
            skLineSegment(sketch, "E350", {"start": v(-3.4, 31.67) * mm, "end": v(-4.55, 31.75) * mm});
            skLineSegment(sketch, "E351", {"start": v(-4.55, 31.75) * mm, "end": v(-5.56, 31.72) * mm});
            skLineSegment(sketch, "E352", {"start": v(-5.56, 31.72) * mm, "end": v(-8.23, 31.25) * mm});
            skLineSegment(sketch, "E353", {"start": v(-8.23, 31.25) * mm, "end": v(-10.1, 30.77) * mm});
            skLineSegment(sketch, "E354", {"start": v(-16.8, -2.87) * mm, "end": v(-17.05, -1.86) * mm});
            skLineSegment(sketch, "E355", {"start": v(-17.05, -1.86) * mm, "end": v(-17.08, -0.98) * mm});
            skLineSegment(sketch, "E356", {"start": v(-17.08, -0.98) * mm, "end": v(-16.96, -0.34) * mm});
            skLineSegment(sketch, "E357", {"start": v(-16.96, -0.34) * mm, "end": v(-16.61, 0.47) * mm});
            skLineSegment(sketch, "E358", {"start": v(-16.61, 0.47) * mm, "end": v(-16.06, 1.17) * mm});
            skLineSegment(sketch, "E359", {"start": v(-16.06, 1.17) * mm, "end": v(-15.37, 1.76) * mm});
            skLineSegment(sketch, "E360", {"start": v(-15.37, 1.76) * mm, "end": v(-14.09, 2.54) * mm});
            skLineSegment(sketch, "E361", {"start": v(-14.09, 2.54) * mm, "end": v(-13.2, 2.9) * mm});
            skLineSegment(sketch, "E362", {"start": v(-13.2, 2.9) * mm, "end": v(-12.33, 3.23) * mm});
            skLineSegment(sketch, "E363", {"start": v(-12.33, 3.23) * mm, "end": v(-12.18, 3.32) * mm});
            skLineSegment(sketch, "E364", {"start": v(-12.18, 3.32) * mm, "end": v(-12.18, 3.37) * mm});
            skLineSegment(sketch, "E365", {"start": v(-12.18, 3.37) * mm, "end": v(-12.22, 3.44) * mm});
            skLineSegment(sketch, "E366", {"start": v(-12.22, 3.44) * mm, "end": v(-12.5, 3.44) * mm});
            skLineSegment(sketch, "E367", {"start": v(-12.5, 3.44) * mm, "end": v(-13.15, 3.3) * mm});
            skLineSegment(sketch, "E368", {"start": v(-13.15, 3.3) * mm, "end": v(-14.16, 2.97) * mm});
            skLineSegment(sketch, "E369", {"start": v(-14.16, 2.97) * mm, "end": v(-15.18, 2.51) * mm});
            skLineSegment(sketch, "E370", {"start": v(-15.18, 2.51) * mm, "end": v(-15.8, 2.16) * mm});
            skLineSegment(sketch, "E371", {"start": v(-15.8, 2.16) * mm, "end": v(-16.54, 1.62) * mm});
            skLineSegment(sketch, "E372", {"start": v(-16.54, 1.62) * mm, "end": v(-17.1, 1.07) * mm});
            skLineSegment(sketch, "E373", {"start": v(-17.1, 1.07) * mm, "end": v(-17.45, 0.61) * mm});
            skLineSegment(sketch, "E374", {"start": v(-17.45, 0.61) * mm, "end": v(-17.72, 0.12) * mm});
            skLineSegment(sketch, "E375", {"start": v(-17.72, 0.12) * mm, "end": v(-17.86, -0.23) * mm});
            skLineSegment(sketch, "E376", {"start": v(-17.86, -0.23) * mm, "end": v(-18.04, -0.94) * mm});
            skLineSegment(sketch, "E377", {"start": v(-18.04, -0.94) * mm, "end": v(-18.14, -2.16) * mm});
            skLineSegment(sketch, "E378", {"start": v(-18.14, -2.16) * mm, "end": v(-18.03, -2.96) * mm});
            skLineSegment(sketch, "E379", {"start": v(-18.03, -2.96) * mm, "end": v(-17.76, -3.75) * mm});
            skLineSegment(sketch, "E380", {"start": v(-17.76, -3.75) * mm, "end": v(-17.51, -4.25) * mm});
            skLineSegment(sketch, "E381", {"start": v(-17.51, -4.25) * mm, "end": v(-17.2, -4.6) * mm});
            skLineSegment(sketch, "E382", {"start": v(-17.2, -4.6) * mm, "end": v(-16.95, -4.7) * mm});
            skLineSegment(sketch, "E383", {"start": v(-16.95, -4.7) * mm, "end": v(-16.68, -4.65) * mm});
            skLineSegment(sketch, "E384", {"start": v(-16.68, -4.65) * mm, "end": v(-16.46, -4.5) * mm});
            skLineSegment(sketch, "E385", {"start": v(-16.46, -4.5) * mm, "end": v(-16.4, -4.24) * mm});
            skLineSegment(sketch, "E386", {"start": v(-16.4, -4.24) * mm, "end": v(-16.56, -3.62) * mm});
            skLineSegment(sketch, "E387", {"start": v(-16.56, -3.62) * mm, "end": v(-16.8, -2.87) * mm});
            skLineSegment(sketch, "E388", {"start": v(5.8, 23.2) * mm, "end": v(6.2, 22.95) * mm});
            skLineSegment(sketch, "E389", {"start": v(6.2, 22.95) * mm, "end": v(6.62, 22.8) * mm});
            skLineSegment(sketch, "E390", {"start": v(6.62, 22.8) * mm, "end": v(6.97, 22.75) * mm});
            skLineSegment(sketch, "E391", {"start": v(6.97, 22.75) * mm, "end": v(7.24, 22.78) * mm});
            skLineSegment(sketch, "E392", {"start": v(7.24, 22.78) * mm, "end": v(7.56, 22.9) * mm});
            skLineSegment(sketch, "E393", {"start": v(7.56, 22.9) * mm, "end": v(7.73, 23.05) * mm});
            skLineSegment(sketch, "E394", {"start": v(7.73, 23.05) * mm, "end": v(7.88, 23.22) * mm});
            skLineSegment(sketch, "E395", {"start": v(7.88, 23.22) * mm, "end": v(7.98, 23.47) * mm});
            skLineSegment(sketch, "E396", {"start": v(7.98, 23.47) * mm, "end": v(8, 23.73) * mm});
            skLineSegment(sketch, "E397", {"start": v(8, 23.73) * mm, "end": v(7.9, 24.06) * mm});
            skLineSegment(sketch, "E398", {"start": v(7.9, 24.06) * mm, "end": v(7.7, 24.38) * mm});
            skLineSegment(sketch, "E399", {"start": v(7.7, 24.38) * mm, "end": v(7.55, 24.56) * mm});
            skLineSegment(sketch, "E400", {"start": v(7.55, 24.56) * mm, "end": v(7.23, 24.83) * mm});
            skLineSegment(sketch, "E401", {"start": v(7.23, 24.83) * mm, "end": v(7.02, 24.98) * mm});
            skLineSegment(sketch, "E402", {"start": v(7.02, 24.98) * mm, "end": v(6.72, 25.15) * mm});
            skLineSegment(sketch, "E403", {"start": v(6.72, 25.15) * mm, "end": v(6.42, 25.27) * mm});
            skLineSegment(sketch, "E404", {"start": v(6.42, 25.27) * mm, "end": v(6.12, 25.35) * mm});
            skLineSegment(sketch, "E405", {"start": v(6.12, 25.35) * mm, "end": v(5.91, 25.38) * mm});
            skLineSegment(sketch, "E406", {"start": v(5.91, 25.38) * mm, "end": v(5.71, 25.37) * mm});
            skLineSegment(sketch, "E407", {"start": v(5.71, 25.37) * mm, "end": v(5.48, 25.3) * mm});
            skLineSegment(sketch, "E408", {"start": v(5.48, 25.3) * mm, "end": v(5.38, 25.25) * mm});
            skLineSegment(sketch, "E409", {"start": v(5.38, 25.25) * mm, "end": v(5.18, 25.05) * mm});
            skLineSegment(sketch, "E410", {"start": v(5.18, 25.05) * mm, "end": v(5.1, 24.9) * mm});
            skLineSegment(sketch, "E411", {"start": v(5.1, 24.9) * mm, "end": v(5.01, 24.64) * mm});
            skLineSegment(sketch, "E412", {"start": v(5.01, 24.64) * mm, "end": v(5.02, 24.32) * mm});
            skLineSegment(sketch, "E413", {"start": v(5.02, 24.32) * mm, "end": v(5.1, 24.06) * mm});
            skLineSegment(sketch, "E414", {"start": v(5.1, 24.06) * mm, "end": v(5.27, 23.75) * mm});
            skLineSegment(sketch, "E415", {"start": v(5.27, 23.75) * mm, "end": v(5.5, 23.46) * mm});
            skLineSegment(sketch, "E416", {"start": v(5.5, 23.46) * mm, "end": v(5.8, 23.2) * mm});
            skLineSegment(sketch, "E417", {"start": v(-2.58, 17.76) * mm, "end": v(-1.14, 17.48) * mm});
            skLineSegment(sketch, "E418", {"start": v(-1.14, 17.48) * mm, "end": v(0.29, 17.16) * mm});
            skLineSegment(sketch, "E419", {"start": v(0.29, 17.16) * mm, "end": v(0.83, 17.1) * mm});
            skLineSegment(sketch, "E420", {"start": v(0.83, 17.1) * mm, "end": v(1, 17.24) * mm});
            skLineSegment(sketch, "E421", {"start": v(1, 17.24) * mm, "end": v(1.06, 17.5) * mm});
            skLineSegment(sketch, "E422", {"start": v(1.06, 17.5) * mm, "end": v(1, 18.03) * mm});
            skLineSegment(sketch, "E423", {"start": v(1, 18.03) * mm, "end": v(0.85, 18.5) * mm});
            skLineSegment(sketch, "E424", {"start": v(0.85, 18.5) * mm, "end": v(0.4, 19.03) * mm});
            skLineSegment(sketch, "E425", {"start": v(0.4, 19.03) * mm, "end": v(-0.33, 19.57) * mm});
            skLineSegment(sketch, "E426", {"start": v(-0.33, 19.57) * mm, "end": v(-1.44, 20.2) * mm});
            skLineSegment(sketch, "E427", {"start": v(-1.44, 20.2) * mm, "end": v(-2.2, 20.68) * mm});
            skLineSegment(sketch, "E428", {"start": v(-2.2, 20.68) * mm, "end": v(-2.71, 21.11) * mm});
            skLineSegment(sketch, "E429", {"start": v(-2.71, 21.11) * mm, "end": v(-2.98, 21.27) * mm});
            skLineSegment(sketch, "E430", {"start": v(-2.98, 21.27) * mm, "end": v(-3.31, 21.28) * mm});
            skLineSegment(sketch, "E431", {"start": v(-3.31, 21.28) * mm, "end": v(-3.54, 21.1) * mm});
            skLineSegment(sketch, "E432", {"start": v(-3.54, 21.1) * mm, "end": v(-3.8, 20.64) * mm});
            skLineSegment(sketch, "E433", {"start": v(-3.8, 20.64) * mm, "end": v(-3.96, 20.14) * mm});
            skLineSegment(sketch, "E434", {"start": v(-3.96, 20.14) * mm, "end": v(-4.04, 19.7) * mm});
            skLineSegment(sketch, "E435", {"start": v(-4.04, 19.7) * mm, "end": v(-4.06, 18.86) * mm});
            skLineSegment(sketch, "E436", {"start": v(-4.06, 18.86) * mm, "end": v(-3.95, 18.33) * mm});
            skLineSegment(sketch, "E437", {"start": v(-3.95, 18.33) * mm, "end": v(-3.74, 18.03) * mm});
            skLineSegment(sketch, "E438", {"start": v(-3.74, 18.03) * mm, "end": v(-3.39, 17.86) * mm});
            skLineSegment(sketch, "E439", {"start": v(-3.39, 17.86) * mm, "end": v(-2.98, 17.8) * mm});
            skLineSegment(sketch, "E440", {"start": v(-2.98, 17.8) * mm, "end": v(-2.58, 17.76) * mm});
            skLineSegment(sketch, "E441", {"start": v(-0.58, 13.29) * mm, "end": v(2.08, 13.62) * mm});
            skLineSegment(sketch, "E442", {"start": v(2.08, 13.62) * mm, "end": v(2.95, 13.69) * mm});
            skLineSegment(sketch, "E443", {"start": v(2.95, 13.69) * mm, "end": v(3.88, 13.65) * mm});
            skLineSegment(sketch, "E444", {"start": v(3.88, 13.65) * mm, "end": v(4.22, 13.66) * mm});
            skLineSegment(sketch, "E445", {"start": v(4.22, 13.66) * mm, "end": v(4.49, 13.76) * mm});
            skLineSegment(sketch, "E446", {"start": v(4.49, 13.76) * mm, "end": v(4.52, 13.95) * mm});
            skLineSegment(sketch, "E447", {"start": v(4.52, 13.95) * mm, "end": v(4.4, 14.27) * mm});
            skLineSegment(sketch, "E448", {"start": v(4.4, 14.27) * mm, "end": v(4.14, 14.68) * mm});
            skLineSegment(sketch, "E449", {"start": v(4.14, 14.68) * mm, "end": v(3.67, 15.17) * mm});
            skLineSegment(sketch, "E450", {"start": v(3.67, 15.17) * mm, "end": v(3.32, 15.32) * mm});
            skLineSegment(sketch, "E451", {"start": v(3.32, 15.32) * mm, "end": v(2.95, 15.26) * mm});
            skLineSegment(sketch, "E452", {"start": v(2.95, 15.26) * mm, "end": v(2.66, 15.12) * mm});
            skLineSegment(sketch, "E453", {"start": v(2.66, 15.12) * mm, "end": v(2.14, 14.84) * mm});
            skLineSegment(sketch, "E454", {"start": v(2.14, 14.84) * mm, "end": v(1.83, 14.77) * mm});
            skLineSegment(sketch, "E455", {"start": v(1.83, 14.77) * mm, "end": v(1.5, 14.87) * mm});
            skLineSegment(sketch, "E456", {"start": v(1.5, 14.87) * mm, "end": v(1.02, 15.33) * mm});
            skLineSegment(sketch, "E457", {"start": v(1.02, 15.33) * mm, "end": v(0.57, 15.76) * mm});
            skLineSegment(sketch, "E458", {"start": v(0.57, 15.76) * mm, "end": v(-0.23, 16.05) * mm});
            skLineSegment(sketch, "E459", {"start": v(-0.23, 16.05) * mm, "end": v(-1.5, 16.22) * mm});
            skLineSegment(sketch, "E460", {"start": v(-1.5, 16.22) * mm, "end": v(-2.45, 16.26) * mm});
            skLineSegment(sketch, "E461", {"start": v(-2.45, 16.26) * mm, "end": v(-3.34, 16.32) * mm});
            skLineSegment(sketch, "E462", {"start": v(-3.34, 16.32) * mm, "end": v(-3.86, 16.36) * mm});
            skLineSegment(sketch, "E463", {"start": v(-3.86, 16.36) * mm, "end": v(-4.22, 16.24) * mm});
            skLineSegment(sketch, "E464", {"start": v(-4.22, 16.24) * mm, "end": v(-4.33, 15.95) * mm});
            skLineSegment(sketch, "E465", {"start": v(-4.33, 15.95) * mm, "end": v(-4.28, 15.54) * mm});
            skLineSegment(sketch, "E466", {"start": v(-4.28, 15.54) * mm, "end": v(-4.02, 14.8) * mm});
            skLineSegment(sketch, "E467", {"start": v(-4.02, 14.8) * mm, "end": v(-3.52, 13.82) * mm});
            skLineSegment(sketch, "E468", {"start": v(-3.52, 13.82) * mm, "end": v(-3.2, 13.41) * mm});
            skLineSegment(sketch, "E469", {"start": v(-3.2, 13.41) * mm, "end": v(-2.76, 13.1) * mm});
            skLineSegment(sketch, "E470", {"start": v(-2.76, 13.1) * mm, "end": v(-2.25, 13.03) * mm});
            skLineSegment(sketch, "E471", {"start": v(-2.25, 13.03) * mm, "end": v(-1.58, 13.1) * mm});
            skLineSegment(sketch, "E472", {"start": v(-1.58, 13.1) * mm, "end": v(-0.58, 13.29) * mm});
            skLineSegment(sketch, "E473", {"start": v(7.06, 5.54) * mm, "end": v(8.6, 5.86) * mm});
            skLineSegment(sketch, "E474", {"start": v(8.6, 5.86) * mm, "end": v(9.36, 5.97) * mm});
            skLineSegment(sketch, "E475", {"start": v(9.36, 5.97) * mm, "end": v(10.13, 6.02) * mm});
            skLineSegment(sketch, "E476", {"start": v(10.13, 6.02) * mm, "end": v(10.57, 6.1) * mm});
            skLineSegment(sketch, "E477", {"start": v(10.57, 6.1) * mm, "end": v(10.88, 6.27) * mm});
            skLineSegment(sketch, "E478", {"start": v(10.88, 6.27) * mm, "end": v(10.91, 6.48) * mm});
            skLineSegment(sketch, "E479", {"start": v(10.91, 6.48) * mm, "end": v(10.8, 6.73) * mm});
            skLineSegment(sketch, "E480", {"start": v(10.8, 6.73) * mm, "end": v(10.38, 7.2) * mm});
            skLineSegment(sketch, "E481", {"start": v(10.38, 7.2) * mm, "end": v(9.62, 7.94) * mm});
            skLineSegment(sketch, "E482", {"start": v(9.62, 7.94) * mm, "end": v(9.24, 8.25) * mm});
            skLineSegment(sketch, "E483", {"start": v(9.24, 8.25) * mm, "end": v(8.7, 8.57) * mm});
            skLineSegment(sketch, "E484", {"start": v(8.7, 8.57) * mm, "end": v(8.19, 8.74) * mm});
            skLineSegment(sketch, "E485", {"start": v(8.19, 8.74) * mm, "end": v(7.62, 8.82) * mm});
            skLineSegment(sketch, "E486", {"start": v(7.62, 8.82) * mm, "end": v(7.1, 8.8) * mm});
            skLineSegment(sketch, "E487", {"start": v(7.1, 8.8) * mm, "end": v(6.45, 8.72) * mm});
            skLineSegment(sketch, "E488", {"start": v(6.45, 8.72) * mm, "end": v(4.9, 8.45) * mm});
            skLineSegment(sketch, "E489", {"start": v(4.9, 8.45) * mm, "end": v(3.57, 8.15) * mm});
            skLineSegment(sketch, "E490", {"start": v(3.57, 8.15) * mm, "end": v(2.86, 7.99) * mm});
            skLineSegment(sketch, "E491", {"start": v(2.86, 7.99) * mm, "end": v(2.46, 7.82) * mm});
            skLineSegment(sketch, "E492", {"start": v(2.46, 7.82) * mm, "end": v(2.33, 7.7) * mm});
            skLineSegment(sketch, "E493", {"start": v(2.33, 7.7) * mm, "end": v(2.29, 7.54) * mm});
            skLineSegment(sketch, "E494", {"start": v(2.29, 7.54) * mm, "end": v(2.34, 7.38) * mm});
            skLineSegment(sketch, "E495", {"start": v(2.34, 7.38) * mm, "end": v(2.58, 7.07) * mm});
            skLineSegment(sketch, "E496", {"start": v(2.58, 7.07) * mm, "end": v(3.47, 6.24) * mm});
            skLineSegment(sketch, "E497", {"start": v(3.47, 6.24) * mm, "end": v(3.9, 5.87) * mm});
            skLineSegment(sketch, "E498", {"start": v(3.9, 5.87) * mm, "end": v(4.25, 5.61) * mm});
            skLineSegment(sketch, "E499", {"start": v(4.25, 5.61) * mm, "end": v(4.61, 5.41) * mm});
            skLineSegment(sketch, "E500", {"start": v(4.61, 5.41) * mm, "end": v(5.05, 5.28) * mm});
            skLineSegment(sketch, "E501", {"start": v(5.05, 5.28) * mm, "end": v(5.32, 5.28) * mm});
            skLineSegment(sketch, "E502", {"start": v(5.32, 5.28) * mm, "end": v(5.93, 5.34) * mm});
            skLineSegment(sketch, "E503", {"start": v(5.93, 5.34) * mm, "end": v(7.06, 5.54) * mm});
            skLineSegment(sketch, "E504", {"start": v(14.85, -5.41) * mm, "end": v(15.67, -5.28) * mm});
            skLineSegment(sketch, "E505", {"start": v(15.67, -5.28) * mm, "end": v(16.47, -5.07) * mm});
            skLineSegment(sketch, "E506", {"start": v(16.47, -5.07) * mm, "end": v(17, -4.84) * mm});
            skLineSegment(sketch, "E507", {"start": v(17, -4.84) * mm, "end": v(17.28, -4.56) * mm});
            skLineSegment(sketch, "E508", {"start": v(17.28, -4.56) * mm, "end": v(17.37, -4.2) * mm});
            skLineSegment(sketch, "E509", {"start": v(17.37, -4.2) * mm, "end": v(17.3, -3.64) * mm});
            skLineSegment(sketch, "E510", {"start": v(17.3, -3.64) * mm, "end": v(16.94, -2.56) * mm});
            skLineSegment(sketch, "E511", {"start": v(16.94, -2.56) * mm, "end": v(16.56, -1.37) * mm});
            skLineSegment(sketch, "E512", {"start": v(16.56, -1.37) * mm, "end": v(16.24, -0.7) * mm});
            skLineSegment(sketch, "E513", {"start": v(16.24, -0.7) * mm, "end": v(15.96, -0.36) * mm});
            skLineSegment(sketch, "E514", {"start": v(15.96, -0.36) * mm, "end": v(15.63, -0.11) * mm});
            skLineSegment(sketch, "E515", {"start": v(15.63, -0.11) * mm, "end": v(15.2, 0.01) * mm});
            skLineSegment(sketch, "E516", {"start": v(15.2, 0.01) * mm, "end": v(14.77, 0.01) * mm});
            skLineSegment(sketch, "E517", {"start": v(14.77, 0.01) * mm, "end": v(14.37, -0.06) * mm});
            skLineSegment(sketch, "E518", {"start": v(14.37, -0.06) * mm, "end": v(13.97, -0.18) * mm});
            skLineSegment(sketch, "E519", {"start": v(13.97, -0.18) * mm, "end": v(13.18, -0.4) * mm});
            skLineSegment(sketch, "E520", {"start": v(13.18, -0.4) * mm, "end": v(12.41, -0.62) * mm});
            skLineSegment(sketch, "E521", {"start": v(12.41, -0.62) * mm, "end": v(11.67, -0.9) * mm});
            skLineSegment(sketch, "E522", {"start": v(11.67, -0.9) * mm, "end": v(11.32, -1.1) * mm});
            skLineSegment(sketch, "E523", {"start": v(11.32, -1.1) * mm, "end": v(10.98, -1.37) * mm});
            skLineSegment(sketch, "E524", {"start": v(10.98, -1.37) * mm, "end": v(10.84, -1.69) * mm});
            skLineSegment(sketch, "E525", {"start": v(10.84, -1.69) * mm, "end": v(10.9, -1.94) * mm});
            skLineSegment(sketch, "E526", {"start": v(10.9, -1.94) * mm, "end": v(11.09, -2.33) * mm});
            skLineSegment(sketch, "E527", {"start": v(11.09, -2.33) * mm, "end": v(11.4, -2.82) * mm});
            skLineSegment(sketch, "E528", {"start": v(11.4, -2.82) * mm, "end": v(11.63, -3.24) * mm});
            skLineSegment(sketch, "E529", {"start": v(11.63, -3.24) * mm, "end": v(12.04, -4.34) * mm});
            skLineSegment(sketch, "E530", {"start": v(12.04, -4.34) * mm, "end": v(12.36, -5.05) * mm});
            skLineSegment(sketch, "E531", {"start": v(12.36, -5.05) * mm, "end": v(12.7, -5.48) * mm});
            skLineSegment(sketch, "E532", {"start": v(12.7, -5.48) * mm, "end": v(13.03, -5.6) * mm});
            skLineSegment(sketch, "E533", {"start": v(13.03, -5.6) * mm, "end": v(13.54, -5.56) * mm});
            skLineSegment(sketch, "E534", {"start": v(13.54, -5.56) * mm, "end": v(13.83, -5.52) * mm});
            skLineSegment(sketch, "E535", {"start": v(13.83, -5.52) * mm, "end": v(14.23, -5.48) * mm});
            skLineSegment(sketch, "E536", {"start": v(14.23, -5.48) * mm, "end": v(14.85, -5.41) * mm});
            skLineSegment(sketch, "E537", {"start": v(14.3, -12.43) * mm, "end": v(15.35, -12.2) * mm});
            skLineSegment(sketch, "E538", {"start": v(15.35, -12.2) * mm, "end": v(16.2, -11.92) * mm});
            skLineSegment(sketch, "E539", {"start": v(16.2, -11.92) * mm, "end": v(17.05, -11.48) * mm});
            skLineSegment(sketch, "E540", {"start": v(17.05, -11.48) * mm, "end": v(17.5, -11.05) * mm});
            skLineSegment(sketch, "E541", {"start": v(17.5, -11.05) * mm, "end": v(17.84, -10.26) * mm});
            skLineSegment(sketch, "E542", {"start": v(17.84, -10.26) * mm, "end": v(18.14, -9.21) * mm});
            skLineSegment(sketch, "E543", {"start": v(18.14, -9.21) * mm, "end": v(18.26, -8.23) * mm});
            skLineSegment(sketch, "E544", {"start": v(18.26, -8.23) * mm, "end": v(18.18, -7.62) * mm});
            skLineSegment(sketch, "E545", {"start": v(18.18, -7.62) * mm, "end": v(18.04, -7.33) * mm});
            skLineSegment(sketch, "E546", {"start": v(18.04, -7.33) * mm, "end": v(17.8, -7.14) * mm});
            skLineSegment(sketch, "E547", {"start": v(17.8, -7.14) * mm, "end": v(17.47, -7.05) * mm});
            skLineSegment(sketch, "E548", {"start": v(17.47, -7.05) * mm, "end": v(16.8, -7.12) * mm});
            skLineSegment(sketch, "E549", {"start": v(16.8, -7.12) * mm, "end": v(16, -7.23) * mm});
            skLineSegment(sketch, "E550", {"start": v(16, -7.23) * mm, "end": v(15.18, -7.3) * mm});
            skLineSegment(sketch, "E551", {"start": v(15.18, -7.3) * mm, "end": v(14.47, -7.32) * mm});
            skLineSegment(sketch, "E552", {"start": v(14.47, -7.32) * mm, "end": v(14.02, -7.31) * mm});
            skLineSegment(sketch, "E553", {"start": v(14.02, -7.31) * mm, "end": v(13.69, -7.39) * mm});
            skLineSegment(sketch, "E554", {"start": v(13.69, -7.39) * mm, "end": v(13.5, -7.57) * mm});
            skLineSegment(sketch, "E555", {"start": v(13.5, -7.57) * mm, "end": v(13.42, -7.85) * mm});
            skLineSegment(sketch, "E556", {"start": v(13.42, -7.85) * mm, "end": v(13.4, -8.27) * mm});
            skLineSegment(sketch, "E557", {"start": v(13.4, -8.27) * mm, "end": v(13.37, -8.66) * mm});
            skLineSegment(sketch, "E558", {"start": v(13.37, -8.66) * mm, "end": v(13.18, -9.9) * mm});
            skLineSegment(sketch, "E559", {"start": v(13.18, -9.9) * mm, "end": v(12.91, -11.12) * mm});
            skLineSegment(sketch, "E560", {"start": v(12.91, -11.12) * mm, "end": v(12.66, -11.9) * mm});
            skLineSegment(sketch, "E561", {"start": v(12.66, -11.9) * mm, "end": v(12.6, -12.2) * mm});
            skLineSegment(sketch, "E562", {"start": v(12.6, -12.2) * mm, "end": v(12.64, -12.35) * mm});
            skLineSegment(sketch, "E563", {"start": v(12.64, -12.35) * mm, "end": v(12.74, -12.43) * mm});
            skLineSegment(sketch, "E564", {"start": v(12.74, -12.43) * mm, "end": v(13.01, -12.49) * mm});
            skLineSegment(sketch, "E565", {"start": v(13.01, -12.49) * mm, "end": v(13.47, -12.5) * mm});
            skLineSegment(sketch, "E566", {"start": v(13.47, -12.5) * mm, "end": v(14.3, -12.43) * mm});
            skLineSegment(sketch, "E567", {"start": v(12.4, -17.97) * mm, "end": v(13.07, -17.94) * mm});
            skLineSegment(sketch, "E568", {"start": v(13.07, -17.94) * mm, "end": v(13.9, -17.86) * mm});
            skLineSegment(sketch, "E569", {"start": v(13.9, -17.86) * mm, "end": v(14.74, -17.69) * mm});
            skLineSegment(sketch, "E570", {"start": v(14.74, -17.69) * mm, "end": v(15.3, -17.47) * mm});
            skLineSegment(sketch, "E571", {"start": v(15.3, -17.47) * mm, "end": v(15.8, -17.08) * mm});
            skLineSegment(sketch, "E572", {"start": v(15.8, -17.08) * mm, "end": v(16.28, -16.43) * mm});
            skLineSegment(sketch, "E573", {"start": v(16.28, -16.43) * mm, "end": v(16.86, -15.46) * mm});
            skLineSegment(sketch, "E574", {"start": v(16.86, -15.46) * mm, "end": v(17.13, -14.8) * mm});
            skLineSegment(sketch, "E575", {"start": v(17.13, -14.8) * mm, "end": v(17.18, -14.4) * mm});
            skLineSegment(sketch, "E576", {"start": v(17.18, -14.4) * mm, "end": v(17.15, -14.2) * mm});
            skLineSegment(sketch, "E577", {"start": v(17.15, -14.2) * mm, "end": v(17.07, -14.08) * mm});
            skLineSegment(sketch, "E578", {"start": v(17.07, -14.08) * mm, "end": v(16.9, -13.97) * mm});
            skLineSegment(sketch, "E579", {"start": v(16.9, -13.97) * mm, "end": v(16.73, -13.92) * mm});
            skLineSegment(sketch, "E580", {"start": v(16.73, -13.92) * mm, "end": v(16.5, -13.93) * mm});
            skLineSegment(sketch, "E581", {"start": v(16.5, -13.93) * mm, "end": v(15.87, -13.98) * mm});
            skLineSegment(sketch, "E582", {"start": v(15.87, -13.98) * mm, "end": v(15.24, -14.01) * mm});
            skLineSegment(sketch, "E583", {"start": v(15.24, -14.01) * mm, "end": v(14.57, -14.06) * mm});
            skLineSegment(sketch, "E584", {"start": v(14.57, -14.06) * mm, "end": v(14, -14.11) * mm});
            skLineSegment(sketch, "E585", {"start": v(14, -14.11) * mm, "end": v(13.68, -14.16) * mm});
            skLineSegment(sketch, "E586", {"start": v(13.68, -14.16) * mm, "end": v(13.18, -14.28) * mm});
            skLineSegment(sketch, "E587", {"start": v(13.18, -14.28) * mm, "end": v(12.83, -14.41) * mm});
            skLineSegment(sketch, "E588", {"start": v(12.83, -14.41) * mm, "end": v(12.54, -14.59) * mm});
            skLineSegment(sketch, "E589", {"start": v(12.54, -14.59) * mm, "end": v(12.27, -14.84) * mm});
            skLineSegment(sketch, "E590", {"start": v(12.27, -14.84) * mm, "end": v(11.95, -15.24) * mm});
            skLineSegment(sketch, "E591", {"start": v(11.95, -15.24) * mm, "end": v(11.5, -15.99) * mm});
            skLineSegment(sketch, "E592", {"start": v(11.5, -15.99) * mm, "end": v(11.18, -16.53) * mm});
            skLineSegment(sketch, "E593", {"start": v(11.18, -16.53) * mm, "end": v(10.9, -16.9) * mm});
            skLineSegment(sketch, "E594", {"start": v(10.9, -16.9) * mm, "end": v(10.73, -17.16) * mm});
            skLineSegment(sketch, "E595", {"start": v(10.73, -17.16) * mm, "end": v(10.67, -17.44) * mm});
            skLineSegment(sketch, "E596", {"start": v(10.67, -17.44) * mm, "end": v(10.77, -17.64) * mm});
            skLineSegment(sketch, "E597", {"start": v(10.77, -17.64) * mm, "end": v(11.07, -17.8) * mm});
            skLineSegment(sketch, "E598", {"start": v(11.07, -17.8) * mm, "end": v(11.5, -17.9) * mm});
            skLineSegment(sketch, "E599", {"start": v(11.5, -17.9) * mm, "end": v(11.97, -17.95) * mm});
            skLineSegment(sketch, "E600", {"start": v(11.97, -17.95) * mm, "end": v(12.4, -17.97) * mm});
            skLineSegment(sketch, "E601", {"start": v(-13.9, 16.65) * mm, "end": v(-8.08, 11.6) * mm});
            skLineSegment(sketch, "E602", {"start": v(-8.08, 11.6) * mm, "end": v(-3.68, 7.74) * mm});
            skLineSegment(sketch, "E603", {"start": v(-3.68, 7.74) * mm, "end": v(-1.15, 5.76) * mm});
            skLineSegment(sketch, "E604", {"start": v(-1.15, 5.76) * mm, "end": v(2.48, 3.03) * mm});
            skLineSegment(sketch, "E605", {"start": v(2.48, 3.03) * mm, "end": v(3.2, 2.93) * mm});
            skLineSegment(sketch, "E606", {"start": v(3.2, 2.93) * mm, "end": v(3.67, 3.54) * mm});
            skLineSegment(sketch, "E607", {"start": v(3.67, 3.54) * mm, "end": v(3.35, 4.25) * mm});
            skLineSegment(sketch, "E608", {"start": v(3.35, 4.25) * mm, "end": v(-2.14, 8.74) * mm});
            skLineSegment(sketch, "E609", {"start": v(-2.14, 8.74) * mm, "end": v(-4.5, 10.46) * mm});
            skLineSegment(sketch, "E610", {"start": v(-4.5, 10.46) * mm, "end": v(-4.54, 11) * mm});
            skLineSegment(sketch, "E611", {"start": v(-4.54, 11) * mm, "end": v(-4.27, 12.17) * mm});
            skLineSegment(sketch, "E612", {"start": v(-4.27, 12.17) * mm, "end": v(-4.34, 12.34) * mm});
            skLineSegment(sketch, "E613", {"start": v(-4.34, 12.34) * mm, "end": v(-4.54, 12.4) * mm});
            skLineSegment(sketch, "E614", {"start": v(-4.54, 12.4) * mm, "end": v(-5.17, 11.9) * mm});
            skLineSegment(sketch, "E615", {"start": v(-5.17, 11.9) * mm, "end": v(-5.63, 11.53) * mm});
            skLineSegment(sketch, "E616", {"start": v(-5.63, 11.53) * mm, "end": v(-6.1, 11.7) * mm});
            skLineSegment(sketch, "E617", {"start": v(-6.1, 11.7) * mm, "end": v(-6.4, 12.08) * mm});
            skLineSegment(sketch, "E618", {"start": v(-6.4, 12.08) * mm, "end": v(-6.27, 13.1) * mm});
            skLineSegment(sketch, "E619", {"start": v(-6.27, 13.1) * mm, "end": v(-6, 13.64) * mm});
            skLineSegment(sketch, "E620", {"start": v(-6, 13.64) * mm, "end": v(-6.03, 13.93) * mm});
            skLineSegment(sketch, "E621", {"start": v(-6.03, 13.93) * mm, "end": v(-6.12, 14.17) * mm});
            skLineSegment(sketch, "E622", {"start": v(-6.12, 14.17) * mm, "end": v(-6.43, 14.16) * mm});
            skLineSegment(sketch, "E623", {"start": v(-6.43, 14.16) * mm, "end": v(-7.13, 13.84) * mm});
            skLineSegment(sketch, "E624", {"start": v(-7.13, 13.84) * mm, "end": v(-7.6, 14.03) * mm});
            skLineSegment(sketch, "E625", {"start": v(-7.6, 14.03) * mm, "end": v(-7.76, 14.28) * mm});
            skLineSegment(sketch, "E626", {"start": v(-7.76, 14.28) * mm, "end": v(-7.62, 14.84) * mm});
            skLineSegment(sketch, "E627", {"start": v(-7.62, 14.84) * mm, "end": v(-6.7, 15.66) * mm});
            skLineSegment(sketch, "E628", {"start": v(-6.7, 15.66) * mm, "end": v(-6.56, 15.93) * mm});
            skLineSegment(sketch, "E629", {"start": v(-6.56, 15.93) * mm, "end": v(-6.64, 16.21) * mm});
            skLineSegment(sketch, "E630", {"start": v(-6.64, 16.21) * mm, "end": v(-7.03, 16.37) * mm});
            skLineSegment(sketch, "E631", {"start": v(-7.03, 16.37) * mm, "end": v(-8.05, 16.32) * mm});
            skLineSegment(sketch, "E632", {"start": v(-8.05, 16.32) * mm, "end": v(-8.51, 16.36) * mm});
            skLineSegment(sketch, "E633", {"start": v(-8.51, 16.36) * mm, "end": v(-9.07, 16.64) * mm});
            skLineSegment(sketch, "E634", {"start": v(-9.07, 16.64) * mm, "end": v(-9.07, 17.02) * mm});
            skLineSegment(sketch, "E635", {"start": v(-9.07, 17.02) * mm, "end": v(-8.6, 17.46) * mm});
            skLineSegment(sketch, "E636", {"start": v(-8.6, 17.46) * mm, "end": v(-7.64, 17.79) * mm});
            skLineSegment(sketch, "E637", {"start": v(-7.64, 17.79) * mm, "end": v(-7.37, 18.08) * mm});
            skLineSegment(sketch, "E638", {"start": v(-7.37, 18.08) * mm, "end": v(-7.32, 18.54) * mm});
            skLineSegment(sketch, "E639", {"start": v(-7.32, 18.54) * mm, "end": v(-7.67, 18.87) * mm});
            skLineSegment(sketch, "E640", {"start": v(-7.67, 18.87) * mm, "end": v(-8.74, 19.15) * mm});
            skLineSegment(sketch, "E641", {"start": v(-8.74, 19.15) * mm, "end": v(-9.16, 19.17) * mm});
            skLineSegment(sketch, "E642", {"start": v(-9.16, 19.17) * mm, "end": v(-9.95, 19.5) * mm});
            skLineSegment(sketch, "E643", {"start": v(-9.95, 19.5) * mm, "end": v(-10.15, 19.87) * mm});
            skLineSegment(sketch, "E644", {"start": v(-10.15, 19.87) * mm, "end": v(-10.18, 20.5) * mm});
            skLineSegment(sketch, "E645", {"start": v(-10.18, 20.5) * mm, "end": v(-10.1, 21.68) * mm});
            skLineSegment(sketch, "E646", {"start": v(-10.1, 21.68) * mm, "end": v(-9.83, 22.78) * mm});
            skLineSegment(sketch, "E647", {"start": v(-9.83, 22.78) * mm, "end": v(-8.81, 24.5) * mm});
            skLineSegment(sketch, "E648", {"start": v(-8.81, 24.5) * mm, "end": v(-7.9, 25.4) * mm});
            skLineSegment(sketch, "E649", {"start": v(-7.9, 25.4) * mm, "end": v(-7.06, 26.07) * mm});
            skLineSegment(sketch, "E650", {"start": v(-7.06, 26.07) * mm, "end": v(-6.97, 26.38) * mm});
            skLineSegment(sketch, "E651", {"start": v(-6.97, 26.38) * mm, "end": v(-7.34, 26.43) * mm});
            skLineSegment(sketch, "E652", {"start": v(-7.34, 26.43) * mm, "end": v(-9.12, 25.65) * mm});
            skLineSegment(sketch, "E653", {"start": v(-9.12, 25.65) * mm, "end": v(-11.3, 24.2) * mm});
            skLineSegment(sketch, "E654", {"start": v(-11.3, 24.2) * mm, "end": v(-13.17, 22.45) * mm});
            skLineSegment(sketch, "E655", {"start": v(-13.17, 22.45) * mm, "end": v(-14.6, 20.36) * mm});
            skLineSegment(sketch, "E656", {"start": v(-14.6, 20.36) * mm, "end": v(-14.99, 19.28) * mm});
            skLineSegment(sketch, "E657", {"start": v(-14.99, 19.28) * mm, "end": v(-15, 17.92) * mm});
            skLineSegment(sketch, "E658", {"start": v(-15, 17.92) * mm, "end": v(-13.9, 16.65) * mm});
            skLineSegment(sketch, "E659", {"start": v(-8.18, 23.6) * mm, "end": v(-8.42, 23.27) * mm});
            skLineSegment(sketch, "E660", {"start": v(-8.42, 23.27) * mm, "end": v(-8.66, 22.81) * mm});
            skLineSegment(sketch, "E661", {"start": v(-8.66, 22.81) * mm, "end": v(-8.82, 22.3) * mm});
            skLineSegment(sketch, "E662", {"start": v(-8.82, 22.3) * mm, "end": v(-8.85, 21.81) * mm});
            skLineSegment(sketch, "E663", {"start": v(-8.85, 21.81) * mm, "end": v(-8.75, 21.22) * mm});
            skLineSegment(sketch, "E664", {"start": v(-8.75, 21.22) * mm, "end": v(-8.36, 20.68) * mm});
            skLineSegment(sketch, "E665", {"start": v(-8.36, 20.68) * mm, "end": v(-7.74, 20.27) * mm});
            skLineSegment(sketch, "E666", {"start": v(-7.74, 20.27) * mm, "end": v(-7.03, 20.23) * mm});
            skLineSegment(sketch, "E667", {"start": v(-7.03, 20.23) * mm, "end": v(-6.48, 20.39) * mm});
            skLineSegment(sketch, "E668", {"start": v(-6.48, 20.39) * mm, "end": v(-6.04, 20.66) * mm});
            skLineSegment(sketch, "E669", {"start": v(-6.04, 20.66) * mm, "end": v(-5.63, 21.04) * mm});
            skLineSegment(sketch, "E670", {"start": v(-5.63, 21.04) * mm, "end": v(-5.29, 21.49) * mm});
            skLineSegment(sketch, "E671", {"start": v(-5.29, 21.49) * mm, "end": v(-5.02, 22) * mm});
            skLineSegment(sketch, "E672", {"start": v(-5.02, 22) * mm, "end": v(-4.86, 22.58) * mm});
            skLineSegment(sketch, "E673", {"start": v(-4.86, 22.58) * mm, "end": v(-4.87, 23.21) * mm});
            skLineSegment(sketch, "E674", {"start": v(-4.87, 23.21) * mm, "end": v(-5.15, 23.8) * mm});
            skLineSegment(sketch, "E675", {"start": v(-5.15, 23.8) * mm, "end": v(-5.57, 24.24) * mm});
            skLineSegment(sketch, "E676", {"start": v(-5.57, 24.24) * mm, "end": v(-6.04, 24.46) * mm});
            skLineSegment(sketch, "E677", {"start": v(-6.04, 24.46) * mm, "end": v(-6.52, 24.53) * mm});
            skLineSegment(sketch, "E678", {"start": v(-6.52, 24.53) * mm, "end": v(-7.04, 24.44) * mm});
            skLineSegment(sketch, "E679", {"start": v(-7.04, 24.44) * mm, "end": v(-7.48, 24.24) * mm});
            skLineSegment(sketch, "E680", {"start": v(-7.48, 24.24) * mm, "end": v(-7.84, 23.96) * mm});
            skLineSegment(sketch, "E681", {"start": v(-7.84, 23.96) * mm, "end": v(-8.18, 23.6) * mm});
            skLineSegment(sketch, "E682", {"start": v(-1.43, 23.58) * mm, "end": v(-0.46, 23.65) * mm});
            skLineSegment(sketch, "E683", {"start": v(-0.46, 23.65) * mm, "end": v(-0.2, 23.65) * mm});
            skLineSegment(sketch, "E684", {"start": v(-0.2, 23.65) * mm, "end": v(0.01, 23.62) * mm});
            skLineSegment(sketch, "E685", {"start": v(0.01, 23.62) * mm, "end": v(0.48, 23.5) * mm});
            skLineSegment(sketch, "E686", {"start": v(0.48, 23.5) * mm, "end": v(1.27, 23.47) * mm});
            skLineSegment(sketch, "E687", {"start": v(1.27, 23.47) * mm, "end": v(2.09, 23.87) * mm});
            skLineSegment(sketch, "E688", {"start": v(2.09, 23.87) * mm, "end": v(2.52, 24.5) * mm});
            skLineSegment(sketch, "E689", {"start": v(2.52, 24.5) * mm, "end": v(2.7, 25.12) * mm});
            skLineSegment(sketch, "E690", {"start": v(2.7, 25.12) * mm, "end": v(2.68, 25.72) * mm});
            skLineSegment(sketch, "E691", {"start": v(2.68, 25.72) * mm, "end": v(2.56, 26.17) * mm});
            skLineSegment(sketch, "E692", {"start": v(2.56, 26.17) * mm, "end": v(2.2, 26.8) * mm});
            skLineSegment(sketch, "E693", {"start": v(2.2, 26.8) * mm, "end": v(1.5, 27.2) * mm});
            skLineSegment(sketch, "E694", {"start": v(1.5, 27.2) * mm, "end": v(0.82, 27.4) * mm});
            skLineSegment(sketch, "E695", {"start": v(0.82, 27.4) * mm, "end": v(0.2, 27.5) * mm});
            skLineSegment(sketch, "E696", {"start": v(0.2, 27.5) * mm, "end": v(-0.44, 27.57) * mm});
            skLineSegment(sketch, "E697", {"start": v(-0.44, 27.57) * mm, "end": v(-1.2, 27.6) * mm});
            skLineSegment(sketch, "E698", {"start": v(-1.2, 27.6) * mm, "end": v(-2.18, 27.52) * mm});
            skLineSegment(sketch, "E699", {"start": v(-2.18, 27.52) * mm, "end": v(-2.83, 27.38) * mm});
            skLineSegment(sketch, "E700", {"start": v(-2.83, 27.38) * mm, "end": v(-3.28, 27.18) * mm});
            skLineSegment(sketch, "E701", {"start": v(-3.28, 27.18) * mm, "end": v(-3.82, 26.67) * mm});
            skLineSegment(sketch, "E702", {"start": v(-3.82, 26.67) * mm, "end": v(-4.1, 26.13) * mm});
            skLineSegment(sketch, "E703", {"start": v(-4.1, 26.13) * mm, "end": v(-4.24, 25.48) * mm});
            skLineSegment(sketch, "E704", {"start": v(-4.24, 25.48) * mm, "end": v(-4.06, 24.68) * mm});
            skLineSegment(sketch, "E705", {"start": v(-4.06, 24.68) * mm, "end": v(-3.7, 24.2) * mm});
            skLineSegment(sketch, "E706", {"start": v(-3.7, 24.2) * mm, "end": v(-3.18, 23.81) * mm});
            skLineSegment(sketch, "E707", {"start": v(-3.18, 23.81) * mm, "end": v(-2.65, 23.64) * mm});
            skLineSegment(sketch, "E708", {"start": v(-2.65, 23.64) * mm, "end": v(-1.97, 23.57) * mm});
            skLineSegment(sketch, "E709", {"start": v(-1.97, 23.57) * mm, "end": v(-1.43, 23.58) * mm});
            skLineSegment(sketch, "E710", {"start": v(2.79, 18.88) * mm, "end": v(3.6, 19) * mm});
            skLineSegment(sketch, "E711", {"start": v(3.6, 19) * mm, "end": v(4.51, 19.3) * mm});
            skLineSegment(sketch, "E712", {"start": v(4.51, 19.3) * mm, "end": v(5.23, 19.72) * mm});
            skLineSegment(sketch, "E713", {"start": v(5.23, 19.72) * mm, "end": v(5.64, 20.55) * mm});
            skLineSegment(sketch, "E714", {"start": v(5.64, 20.55) * mm, "end": v(5.25, 21.61) * mm});
            skLineSegment(sketch, "E715", {"start": v(5.25, 21.61) * mm, "end": v(4.5, 21.94) * mm});
            skLineSegment(sketch, "E716", {"start": v(4.5, 21.94) * mm, "end": v(4.14, 22.01) * mm});
            skLineSegment(sketch, "E717", {"start": v(4.14, 22.01) * mm, "end": v(3.46, 22.19) * mm});
            skLineSegment(sketch, "E718", {"start": v(3.46, 22.19) * mm, "end": v(2.66, 22.37) * mm});
            skLineSegment(sketch, "E719", {"start": v(2.66, 22.37) * mm, "end": v(2.02, 22.44) * mm});
            skLineSegment(sketch, "E720", {"start": v(2.02, 22.44) * mm, "end": v(1.28, 22.32) * mm});
            skLineSegment(sketch, "E721", {"start": v(1.28, 22.32) * mm, "end": v(0.45, 21.54) * mm});
            skLineSegment(sketch, "E722", {"start": v(0.45, 21.54) * mm, "end": v(0.57, 20.43) * mm});
            skLineSegment(sketch, "E723", {"start": v(0.57, 20.43) * mm, "end": v(1, 19.74) * mm});
            skLineSegment(sketch, "E724", {"start": v(1, 19.74) * mm, "end": v(1.38, 19.35) * mm});
            skLineSegment(sketch, "E725", {"start": v(1.38, 19.35) * mm, "end": v(1.86, 19) * mm});
            skLineSegment(sketch, "E726", {"start": v(1.86, 19) * mm, "end": v(2.44, 18.89) * mm});
            skLineSegment(sketch, "E727", {"start": v(2.44, 18.89) * mm, "end": v(2.79, 18.88) * mm});
            skLineSegment(sketch, "E728", {"start": v(-1.15, 10.52) * mm, "end": v(-0.35, 9.87) * mm});
            skLineSegment(sketch, "E729", {"start": v(-0.35, 9.87) * mm, "end": v(0.28, 9.28) * mm});
            skLineSegment(sketch, "E730", {"start": v(0.28, 9.28) * mm, "end": v(1.1, 9.02) * mm});
            skLineSegment(sketch, "E731", {"start": v(1.1, 9.02) * mm, "end": v(2.43, 9.43) * mm});
            skLineSegment(sketch, "E732", {"start": v(2.43, 9.43) * mm, "end": v(4.16, 9.85) * mm});
            skLineSegment(sketch, "E733", {"start": v(4.16, 9.85) * mm, "end": v(5.5, 10.02) * mm});
            skLineSegment(sketch, "E734", {"start": v(5.5, 10.02) * mm, "end": v(6.69, 10.12) * mm});
            skLineSegment(sketch, "E735", {"start": v(6.69, 10.12) * mm, "end": v(7.06, 10.66) * mm});
            skLineSegment(sketch, "E736", {"start": v(7.06, 10.66) * mm, "end": v(6.7, 11.37) * mm});
            skLineSegment(sketch, "E737", {"start": v(6.7, 11.37) * mm, "end": v(5.73, 12.16) * mm});
            skLineSegment(sketch, "E738", {"start": v(5.73, 12.16) * mm, "end": v(4.5, 12.42) * mm});
            skLineSegment(sketch, "E739", {"start": v(4.5, 12.42) * mm, "end": v(2.31, 12.4) * mm});
            skLineSegment(sketch, "E740", {"start": v(2.31, 12.4) * mm, "end": v(0.47, 12.36) * mm});
            skLineSegment(sketch, "E741", {"start": v(0.47, 12.36) * mm, "end": v(-1.23, 11.98) * mm});
            skLineSegment(sketch, "E742", {"start": v(-1.23, 11.98) * mm, "end": v(-1.53, 11.32) * mm});
            skLineSegment(sketch, "E743", {"start": v(-1.53, 11.32) * mm, "end": v(-1.15, 10.52) * mm});
            skLineSegment(sketch, "E744", {"start": v(10.65, 0.87) * mm, "end": v(12.01, 1.28) * mm});
            skLineSegment(sketch, "E745", {"start": v(12.01, 1.28) * mm, "end": v(13.4, 1.48) * mm});
            skLineSegment(sketch, "E746", {"start": v(13.4, 1.48) * mm, "end": v(14.02, 1.55) * mm});
            skLineSegment(sketch, "E747", {"start": v(14.02, 1.55) * mm, "end": v(14.5, 1.67) * mm});
            skLineSegment(sketch, "E748", {"start": v(14.5, 1.67) * mm, "end": v(14.55, 2) * mm});
            skLineSegment(sketch, "E749", {"start": v(14.55, 2) * mm, "end": v(13.72, 3.1) * mm});
            skLineSegment(sketch, "E750", {"start": v(13.72, 3.1) * mm, "end": v(12.8, 3.8) * mm});
            skLineSegment(sketch, "E751", {"start": v(12.8, 3.8) * mm, "end": v(12.24, 4.28) * mm});
            skLineSegment(sketch, "E752", {"start": v(12.24, 4.28) * mm, "end": v(11.25, 4.75) * mm});
            skLineSegment(sketch, "E753", {"start": v(11.25, 4.75) * mm, "end": v(10.15, 4.82) * mm});
            skLineSegment(sketch, "E754", {"start": v(10.15, 4.82) * mm, "end": v(8.65, 4.62) * mm});
            skLineSegment(sketch, "E755", {"start": v(8.65, 4.62) * mm, "end": v(7.53, 4.4) * mm});
            skLineSegment(sketch, "E756", {"start": v(7.53, 4.4) * mm, "end": v(6.74, 3.98) * mm});
            skLineSegment(sketch, "E757", {"start": v(6.74, 3.98) * mm, "end": v(6.38, 3.46) * mm});
            skLineSegment(sketch, "E758", {"start": v(6.38, 3.46) * mm, "end": v(6.74, 3) * mm});
            skLineSegment(sketch, "E759", {"start": v(6.74, 3) * mm, "end": v(7.59, 2.5) * mm});
            skLineSegment(sketch, "E760", {"start": v(7.59, 2.5) * mm, "end": v(8.51, 1.7) * mm});
            skLineSegment(sketch, "E761", {"start": v(8.51, 1.7) * mm, "end": v(9.06, 1.02) * mm});
            skLineSegment(sketch, "E762", {"start": v(9.06, 1.02) * mm, "end": v(9.57, 0.78) * mm});
            skLineSegment(sketch, "E763", {"start": v(9.57, 0.78) * mm, "end": v(10.14, 0.8) * mm});
            skLineSegment(sketch, "E764", {"start": v(10.14, 0.8) * mm, "end": v(10.65, 0.87) * mm});
            skLineSegment(sketch, "E765", {"start": v(8.92, -24.94) * mm, "end": v(9.57, -24.68) * mm});
            skLineSegment(sketch, "E766", {"start": v(9.57, -24.68) * mm, "end": v(10, -24.45) * mm});
            skLineSegment(sketch, "E767", {"start": v(10, -24.45) * mm, "end": v(10.18, -24.31) * mm});
            skLineSegment(sketch, "E768", {"start": v(10.18, -24.31) * mm, "end": v(10.37, -24.08) * mm});
            skLineSegment(sketch, "E769", {"start": v(10.37, -24.08) * mm, "end": v(10.4, -23.84) * mm});
            skLineSegment(sketch, "E770", {"start": v(10.4, -23.84) * mm, "end": v(10.2, -23.55) * mm});
            skLineSegment(sketch, "E771", {"start": v(10.2, -23.55) * mm, "end": v(9.9, -23.37) * mm});
            skLineSegment(sketch, "E772", {"start": v(9.9, -23.37) * mm, "end": v(9.51, -23.18) * mm});
            skLineSegment(sketch, "E773", {"start": v(9.51, -23.18) * mm, "end": v(9.19, -23) * mm});
            skLineSegment(sketch, "E774", {"start": v(9.19, -23) * mm, "end": v(8.66, -22.67) * mm});
            skLineSegment(sketch, "E775", {"start": v(8.66, -22.67) * mm, "end": v(8.09, -22.39) * mm});
            skLineSegment(sketch, "E776", {"start": v(8.09, -22.39) * mm, "end": v(7.79, -22.29) * mm});
            skLineSegment(sketch, "E777", {"start": v(7.79, -22.29) * mm, "end": v(7.49, -22.23) * mm});
            skLineSegment(sketch, "E778", {"start": v(7.49, -22.23) * mm, "end": v(7.19, -22.25) * mm});
            skLineSegment(sketch, "E779", {"start": v(7.19, -22.25) * mm, "end": v(6.98, -22.3) * mm});
            skLineSegment(sketch, "E780", {"start": v(6.98, -22.3) * mm, "end": v(6.72, -22.41) * mm});
            skLineSegment(sketch, "E781", {"start": v(6.72, -22.41) * mm, "end": v(6.08, -22.74) * mm});
            skLineSegment(sketch, "E782", {"start": v(6.08, -22.74) * mm, "end": v(5.66, -23) * mm});
            skLineSegment(sketch, "E783", {"start": v(5.66, -23) * mm, "end": v(5.4, -23.2) * mm});
            skLineSegment(sketch, "E784", {"start": v(5.4, -23.2) * mm, "end": v(5.26, -23.35) * mm});
            skLineSegment(sketch, "E785", {"start": v(5.26, -23.35) * mm, "end": v(5.18, -23.53) * mm});
            skLineSegment(sketch, "E786", {"start": v(5.18, -23.53) * mm, "end": v(5.25, -23.78) * mm});
            skLineSegment(sketch, "E787", {"start": v(5.25, -23.78) * mm, "end": v(5.46, -24.05) * mm});
            skLineSegment(sketch, "E788", {"start": v(5.46, -24.05) * mm, "end": v(5.7, -24.23) * mm});
            skLineSegment(sketch, "E789", {"start": v(5.7, -24.23) * mm, "end": v(6.17, -24.5) * mm});
            skLineSegment(sketch, "E790", {"start": v(6.17, -24.5) * mm, "end": v(6.6, -24.68) * mm});
            skLineSegment(sketch, "E791", {"start": v(6.6, -24.68) * mm, "end": v(6.95, -24.8) * mm});
            skLineSegment(sketch, "E792", {"start": v(6.95, -24.8) * mm, "end": v(7.51, -24.95) * mm});
            skLineSegment(sketch, "E793", {"start": v(7.51, -24.95) * mm, "end": v(7.84, -25) * mm});
            skLineSegment(sketch, "E794", {"start": v(7.84, -25) * mm, "end": v(8.13, -25.04) * mm});
            skLineSegment(sketch, "E795", {"start": v(8.13, -25.04) * mm, "end": v(8.39, -25.06) * mm});
            skLineSegment(sketch, "E796", {"start": v(8.39, -25.06) * mm, "end": v(8.66, -25.02) * mm});
            skLineSegment(sketch, "E797", {"start": v(8.66, -25.02) * mm, "end": v(8.92, -24.94) * mm});
            skLineSegment(sketch, "E798", {"start": v(9.4, -21.54) * mm, "end": v(10.18, -21.78) * mm});
            skLineSegment(sketch, "E799", {"start": v(10.18, -21.78) * mm, "end": v(10.96, -21.92) * mm});
            skLineSegment(sketch, "E800", {"start": v(10.96, -21.92) * mm, "end": v(11.4, -21.96) * mm});
            skLineSegment(sketch, "E801", {"start": v(11.4, -21.96) * mm, "end": v(11.74, -21.95) * mm});
            skLineSegment(sketch, "E802", {"start": v(11.74, -21.95) * mm, "end": v(12.16, -21.9) * mm});
            skLineSegment(sketch, "E803", {"start": v(12.16, -21.9) * mm, "end": v(12.44, -21.8) * mm});
            skLineSegment(sketch, "E804", {"start": v(12.44, -21.8) * mm, "end": v(12.72, -21.67) * mm});
            skLineSegment(sketch, "E805", {"start": v(12.72, -21.67) * mm, "end": v(13.07, -21.42) * mm});
            skLineSegment(sketch, "E806", {"start": v(13.07, -21.42) * mm, "end": v(13.55, -20.97) * mm});
            skLineSegment(sketch, "E807", {"start": v(13.55, -20.97) * mm, "end": v(14.38, -20.07) * mm});
            skLineSegment(sketch, "E808", {"start": v(14.38, -20.07) * mm, "end": v(14.68, -19.73) * mm});
            skLineSegment(sketch, "E809", {"start": v(14.68, -19.73) * mm, "end": v(14.8, -19.49) * mm});
            skLineSegment(sketch, "E810", {"start": v(14.8, -19.49) * mm, "end": v(14.77, -19.31) * mm});
            skLineSegment(sketch, "E811", {"start": v(14.77, -19.31) * mm, "end": v(14.57, -19.06) * mm});
            skLineSegment(sketch, "E812", {"start": v(14.57, -19.06) * mm, "end": v(14.08, -19) * mm});
            skLineSegment(sketch, "E813", {"start": v(14.08, -19) * mm, "end": v(13.49, -19.03) * mm});
            skLineSegment(sketch, "E814", {"start": v(13.49, -19.03) * mm, "end": v(12.57, -19.04) * mm});
            skLineSegment(sketch, "E815", {"start": v(12.57, -19.04) * mm, "end": v(11.66, -18.99) * mm});
            skLineSegment(sketch, "E816", {"start": v(11.66, -18.99) * mm, "end": v(11.18, -18.9) * mm});
            skLineSegment(sketch, "E817", {"start": v(11.18, -18.9) * mm, "end": v(10.7, -18.78) * mm});
            skLineSegment(sketch, "E818", {"start": v(10.7, -18.78) * mm, "end": v(10.27, -18.74) * mm});
            skLineSegment(sketch, "E819", {"start": v(10.27, -18.74) * mm, "end": v(9.94, -18.8) * mm});
            skLineSegment(sketch, "E820", {"start": v(9.94, -18.8) * mm, "end": v(9.62, -18.98) * mm});
            skLineSegment(sketch, "E821", {"start": v(9.62, -18.98) * mm, "end": v(9.43, -19.14) * mm});
            skLineSegment(sketch, "E822", {"start": v(9.43, -19.14) * mm, "end": v(8.8, -19.73) * mm});
            skLineSegment(sketch, "E823", {"start": v(8.8, -19.73) * mm, "end": v(8.49, -20.08) * mm});
            skLineSegment(sketch, "E824", {"start": v(8.49, -20.08) * mm, "end": v(8.34, -20.4) * mm});
            skLineSegment(sketch, "E825", {"start": v(8.34, -20.4) * mm, "end": v(8.33, -20.76) * mm});
            skLineSegment(sketch, "E826", {"start": v(8.33, -20.76) * mm, "end": v(8.55, -21.07) * mm});
            skLineSegment(sketch, "E827", {"start": v(8.55, -21.07) * mm, "end": v(9.04, -21.39) * mm});
            skLineSegment(sketch, "E828", {"start": v(9.04, -21.39) * mm, "end": v(9.4, -21.54) * mm});
            skLineSegment(sketch, "E829", {"start": v(4.56, -27.54) * mm, "end": v(5.27, -27.28) * mm});
            skLineSegment(sketch, "E830", {"start": v(5.27, -27.28) * mm, "end": v(5.85, -27.04) * mm});
            skLineSegment(sketch, "E831", {"start": v(5.85, -27.04) * mm, "end": v(6.03, -26.96) * mm});
            skLineSegment(sketch, "E832", {"start": v(6.03, -26.96) * mm, "end": v(6.45, -26.8) * mm});
            skLineSegment(sketch, "E833", {"start": v(6.45, -26.8) * mm, "end": v(6.58, -26.73) * mm});
            skLineSegment(sketch, "E834", {"start": v(6.58, -26.73) * mm, "end": v(6.78, -26.52) * mm});
            skLineSegment(sketch, "E835", {"start": v(6.78, -26.52) * mm, "end": v(6.66, -26.26) * mm});
            skLineSegment(sketch, "E836", {"start": v(6.66, -26.26) * mm, "end": v(6.3, -26.1) * mm});
            skLineSegment(sketch, "E837", {"start": v(6.3, -26.1) * mm, "end": v(5.85, -25.96) * mm});
            skLineSegment(sketch, "E838", {"start": v(5.85, -25.96) * mm, "end": v(5.25, -25.65) * mm});
            skLineSegment(sketch, "E839", {"start": v(5.25, -25.65) * mm, "end": v(4.87, -25.43) * mm});
            skLineSegment(sketch, "E840", {"start": v(4.87, -25.43) * mm, "end": v(4.18, -25.1) * mm});
            skLineSegment(sketch, "E841", {"start": v(4.18, -25.1) * mm, "end": v(3.88, -25) * mm});
            skLineSegment(sketch, "E842", {"start": v(3.88, -25) * mm, "end": v(3.59, -24.96) * mm});
            skLineSegment(sketch, "E843", {"start": v(3.59, -24.96) * mm, "end": v(3.28, -25) * mm});
            skLineSegment(sketch, "E844", {"start": v(3.28, -25) * mm, "end": v(2.9, -25.1) * mm});
            skLineSegment(sketch, "E845", {"start": v(2.9, -25.1) * mm, "end": v(2.23, -25.35) * mm});
            skLineSegment(sketch, "E846", {"start": v(2.23, -25.35) * mm, "end": v(1.67, -25.62) * mm});
            skLineSegment(sketch, "E847", {"start": v(1.67, -25.62) * mm, "end": v(1.3, -25.85) * mm});
            skLineSegment(sketch, "E848", {"start": v(1.3, -25.85) * mm, "end": v(1.1, -26.03) * mm});
            skLineSegment(sketch, "E849", {"start": v(1.1, -26.03) * mm, "end": v(1.03, -26.12) * mm});
            skLineSegment(sketch, "E850", {"start": v(1.03, -26.12) * mm, "end": v(0.97, -26.37) * mm});
            skLineSegment(sketch, "E851", {"start": v(0.97, -26.37) * mm, "end": v(1.04, -26.64) * mm});
            skLineSegment(sketch, "E852", {"start": v(1.04, -26.64) * mm, "end": v(1.18, -26.84) * mm});
            skLineSegment(sketch, "E853", {"start": v(1.18, -26.84) * mm, "end": v(1.51, -27.11) * mm});
            skLineSegment(sketch, "E854", {"start": v(1.51, -27.11) * mm, "end": v(1.9, -27.31) * mm});
            skLineSegment(sketch, "E855", {"start": v(1.9, -27.31) * mm, "end": v(2.33, -27.47) * mm});
            skLineSegment(sketch, "E856", {"start": v(2.33, -27.47) * mm, "end": v(2.77, -27.59) * mm});
            skLineSegment(sketch, "E857", {"start": v(2.77, -27.59) * mm, "end": v(3.27, -27.68) * mm});
            skLineSegment(sketch, "E858", {"start": v(3.27, -27.68) * mm, "end": v(3.6, -27.7) * mm});
            skLineSegment(sketch, "E859", {"start": v(3.6, -27.7) * mm, "end": v(4.04, -27.66) * mm});
            skLineSegment(sketch, "E860", {"start": v(4.04, -27.66) * mm, "end": v(4.56, -27.54) * mm});
            skLineSegment(sketch, "E861", {"start": v(-6.5, -30.16) * mm, "end": v(-4.85, -30.09) * mm});
            skLineSegment(sketch, "E862", {"start": v(-4.85, -30.09) * mm, "end": v(-3, -29.91) * mm});
            skLineSegment(sketch, "E863", {"start": v(-3, -29.91) * mm, "end": v(-1.16, -29.68) * mm});
            skLineSegment(sketch, "E864", {"start": v(-1.16, -29.68) * mm, "end": v(-0.61, -29.62) * mm});
            skLineSegment(sketch, "E865", {"start": v(-0.61, -29.62) * mm, "end": v(0.07, -29.54) * mm});
            skLineSegment(sketch, "E866", {"start": v(0.07, -29.54) * mm, "end": v(0.62, -29.4) * mm});
            skLineSegment(sketch, "E867", {"start": v(0.62, -29.4) * mm, "end": v(0.98, -29.2) * mm});
            skLineSegment(sketch, "E868", {"start": v(0.98, -29.2) * mm, "end": v(1.11, -29) * mm});
            skLineSegment(sketch, "E869", {"start": v(1.11, -29) * mm, "end": v(1.06, -28.75) * mm});
            skLineSegment(sketch, "E870", {"start": v(1.06, -28.75) * mm, "end": v(0.82, -28.52) * mm});
            skLineSegment(sketch, "E871", {"start": v(0.82, -28.52) * mm, "end": v(0.42, -28.26) * mm});
            skLineSegment(sketch, "E872", {"start": v(0.42, -28.26) * mm, "end": v(-0.35, -27.79) * mm});
            skLineSegment(sketch, "E873", {"start": v(-0.35, -27.79) * mm, "end": v(-0.74, -27.64) * mm});
            skLineSegment(sketch, "E874", {"start": v(-0.74, -27.64) * mm, "end": v(-1.05, -27.58) * mm});
            skLineSegment(sketch, "E875", {"start": v(-1.05, -27.58) * mm, "end": v(-1.28, -27.57) * mm});
            skLineSegment(sketch, "E876", {"start": v(-1.28, -27.57) * mm, "end": v(-1.61, -27.62) * mm});
            skLineSegment(sketch, "E877", {"start": v(-1.61, -27.62) * mm, "end": v(-2.27, -27.8) * mm});
            skLineSegment(sketch, "E878", {"start": v(-2.27, -27.8) * mm, "end": v(-3.52, -28.16) * mm});
            skLineSegment(sketch, "E879", {"start": v(-3.52, -28.16) * mm, "end": v(-5.81, -28.82) * mm});
            skLineSegment(sketch, "E880", {"start": v(-5.81, -28.82) * mm, "end": v(-7.69, -29.37) * mm});
            skLineSegment(sketch, "E881", {"start": v(-7.69, -29.37) * mm, "end": v(-8.85, -29.6) * mm});
            skLineSegment(sketch, "E882", {"start": v(-8.85, -29.6) * mm, "end": v(-9.31, -29.7) * mm});
            skLineSegment(sketch, "E883", {"start": v(-9.31, -29.7) * mm, "end": v(-9.52, -29.81) * mm});
            skLineSegment(sketch, "E884", {"start": v(-9.52, -29.81) * mm, "end": v(-9.47, -30.04) * mm});
            skLineSegment(sketch, "E885", {"start": v(-9.47, -30.04) * mm, "end": v(-9.34, -30.11) * mm});
            skLineSegment(sketch, "E886", {"start": v(-9.34, -30.11) * mm, "end": v(-9.2, -30.16) * mm});
            skLineSegment(sketch, "E887", {"start": v(-9.2, -30.16) * mm, "end": v(-8.95, -30.2) * mm});
            skLineSegment(sketch, "E888", {"start": v(-8.95, -30.2) * mm, "end": v(-8.6, -30.22) * mm});
            skLineSegment(sketch, "E889", {"start": v(-8.6, -30.22) * mm, "end": v(-7.88, -30.21) * mm});
            skLineSegment(sketch, "E890", {"start": v(-7.88, -30.21) * mm, "end": v(-7.22, -30.17) * mm});
            skLineSegment(sketch, "E891", {"start": v(-7.22, -30.17) * mm, "end": v(-6.5, -30.16) * mm});
            skLineSegment(sketch, "E892", {"start": v(-5.22, -20.85) * mm, "end": v(-4.22, -20.79) * mm});
            skLineSegment(sketch, "E893", {"start": v(-4.22, -20.79) * mm, "end": v(-3.4, -20.58) * mm});
            skLineSegment(sketch, "E894", {"start": v(-3.4, -20.58) * mm, "end": v(-4.1, -19.22) * mm});
            skArc(sketch, "E895", {"start": v(-4.1, -19.22) * mm, "mid": v(-4.62, -20.06) * mm, "end": v(-5.22, -20.85) * mm});
            skLineSegment(sketch, "E896", {"start": v(7.44, -16.3) * mm, "end": v(7.92, -15.64) * mm});
            skLineSegment(sketch, "E897", {"start": v(7.92, -15.64) * mm, "end": v(8.34, -14.94) * mm});
            skLineSegment(sketch, "E898", {"start": v(8.34, -14.94) * mm, "end": v(7.55, -15.18) * mm});
            skLineSegment(sketch, "E899", {"start": v(7.55, -15.18) * mm, "end": v(7.5, -15.74) * mm});
            skLineSegment(sketch, "E900", {"start": v(7.5, -15.74) * mm, "end": v(7.44, -16.3) * mm});
            skLineSegment(sketch, "E901", {"start": v(7.66, -14.37) * mm, "end": v(8.73, -14.13) * mm});
            skLineSegment(sketch, "E902", {"start": v(8.73, -14.13) * mm, "end": v(8.93, -13.58) * mm});
            skLineSegment(sketch, "E903", {"start": v(8.93, -13.58) * mm, "end": v(9.1, -13.02) * mm});
            skLineSegment(sketch, "E904", {"start": v(9.1, -13.02) * mm, "end": v(7.84, -13.3) * mm});
            skLineSegment(sketch, "E905", {"start": v(7.84, -13.3) * mm, "end": v(7.74, -13.84) * mm});
            skLineSegment(sketch, "E906", {"start": v(7.74, -13.84) * mm, "end": v(7.66, -14.37) * mm});
            skLineSegment(sketch, "E907", {"start": v(8, -12.5) * mm, "end": v(9.26, -12.3) * mm});
            skLineSegment(sketch, "E908", {"start": v(9.26, -12.3) * mm, "end": v(9.33, -11.8) * mm});
            skLineSegment(sketch, "E909", {"start": v(9.33, -11.8) * mm, "end": v(9.38, -11.27) * mm});
            skLineSegment(sketch, "E910", {"start": v(9.38, -11.27) * mm, "end": v(8.24, -11.46) * mm});
            skLineSegment(sketch, "E911", {"start": v(8.24, -11.46) * mm, "end": v(8.11, -11.98) * mm});
            skLineSegment(sketch, "E912", {"start": v(8.11, -11.98) * mm, "end": v(8, -12.5) * mm});
            skLineSegment(sketch, "E913", {"start": v(8.45, -10.67) * mm, "end": v(9.4, -10.58) * mm});
            skLineSegment(sketch, "E914", {"start": v(9.4, -10.58) * mm, "end": v(9.37, -10.08) * mm});
            skLineSegment(sketch, "E915", {"start": v(9.37, -10.08) * mm, "end": v(9.32, -9.59) * mm});
            skLineSegment(sketch, "E916", {"start": v(9.32, -9.59) * mm, "end": v(8.77, -9.64) * mm});
            skLineSegment(sketch, "E917", {"start": v(8.77, -9.64) * mm, "end": v(8.6, -10.15) * mm});
            skLineSegment(sketch, "E918", {"start": v(8.6, -10.15) * mm, "end": v(8.45, -10.67) * mm});
            skLineSegment(sketch, "E919", {"start": v(-10.8, -2.93) * mm, "end": v(-12.83, -4.15) * mm});
            skLineSegment(sketch, "E920", {"start": v(-12.83, -4.15) * mm, "end": v(-15.41, -6.42) * mm});
            skLineSegment(sketch, "E921", {"start": v(-15.41, -6.42) * mm, "end": v(-17.55, -9.46) * mm});
            skLineSegment(sketch, "E922", {"start": v(-17.55, -9.46) * mm, "end": v(-18.51, -12.23) * mm});
            skLineSegment(sketch, "E923", {"start": v(-18.51, -12.23) * mm, "end": v(-18.77, -14.78) * mm});
            skLineSegment(sketch, "E924", {"start": v(-18.77, -14.78) * mm, "end": v(-18.02, -18.04) * mm});
            skLineSegment(sketch, "E925", {"start": v(-18.02, -18.04) * mm, "end": v(-17.13, -19.35) * mm});
            skLineSegment(sketch, "E926", {"start": v(-17.13, -19.35) * mm, "end": v(-10.28, -21.02) * mm});
            skLineSegment(sketch, "E927", {"start": v(-10.28, -21.02) * mm, "end": v(-8.49, -21.2) * mm});
            skLineSegment(sketch, "E928", {"start": v(-8.49, -21.2) * mm, "end": v(-6.45, -21.2) * mm});
            skLineSegment(sketch, "E929", {"start": v(-6.45, -21.2) * mm, "end": v(-6.32, -20.96) * mm});
            skLineSegment(sketch, "E930", {"start": v(-6.32, -20.96) * mm, "end": v(-8.15, -20.85) * mm});
            skLineSegment(sketch, "E931", {"start": v(-8.15, -20.85) * mm, "end": v(-8.48, -20.69) * mm});
            skLineSegment(sketch, "E932", {"start": v(-8.48, -20.69) * mm, "end": v(-8.61, -20.34) * mm});
            skLineSegment(sketch, "E933", {"start": v(-8.61, -20.34) * mm, "end": v(-8.54, -20.08) * mm});
            skLineSegment(sketch, "E934", {"start": v(-8.54, -20.08) * mm, "end": v(-8.35, -19.9) * mm});
            skLineSegment(sketch, "E935", {"start": v(-8.35, -19.9) * mm, "end": v(-8.1, -19.85) * mm});
            skLineSegment(sketch, "E936", {"start": v(-8.1, -19.85) * mm, "end": v(-5.57, -20) * mm});
            skLineSegment(sketch, "E937", {"start": v(-5.57, -20) * mm, "end": v(-5.1, -19.28) * mm});
            skLineSegment(sketch, "E938", {"start": v(-5.1, -19.28) * mm, "end": v(-6.83, -19.5) * mm});
            skLineSegment(sketch, "E939", {"start": v(-6.83, -19.5) * mm, "end": v(-7.19, -19.4) * mm});
            skLineSegment(sketch, "E940", {"start": v(-7.19, -19.4) * mm, "end": v(-7.38, -19.1) * mm});
            skLineSegment(sketch, "E941", {"start": v(-7.38, -19.1) * mm, "end": v(-7.35, -18.81) * mm});
            skLineSegment(sketch, "E942", {"start": v(-7.35, -18.81) * mm, "end": v(-7.2, -18.62) * mm});
            skLineSegment(sketch, "E943", {"start": v(-7.2, -18.62) * mm, "end": v(-6.96, -18.51) * mm});
            skLineSegment(sketch, "E944", {"start": v(-6.96, -18.51) * mm, "end": v(-4.52, -18.2) * mm});
            skLineSegment(sketch, "E945", {"start": v(-4.52, -18.2) * mm, "end": v(-4.19, -17.4) * mm});
            skLineSegment(sketch, "E946", {"start": v(-4.19, -17.4) * mm, "end": v(-5.78, -17.93) * mm});
            skLineSegment(sketch, "E947", {"start": v(-5.78, -17.93) * mm, "end": v(-6.15, -17.9) * mm});
            skLineSegment(sketch, "E948", {"start": v(-6.15, -17.9) * mm, "end": v(-6.4, -17.63) * mm});
            skLineSegment(sketch, "E949", {"start": v(-6.4, -17.63) * mm, "end": v(-6.43, -17.37) * mm});
            skLineSegment(sketch, "E950", {"start": v(-6.43, -17.37) * mm, "end": v(-6.3, -17.12) * mm});
            skLineSegment(sketch, "E951", {"start": v(-6.3, -17.12) * mm, "end": v(-6.1, -16.98) * mm});
            skLineSegment(sketch, "E952", {"start": v(-6.1, -16.98) * mm, "end": v(-3.82, -16.24) * mm});
            skLineSegment(sketch, "E953", {"start": v(-3.82, -16.24) * mm, "end": v(-3.63, -15.4) * mm});
            skLineSegment(sketch, "E954", {"start": v(-3.63, -15.4) * mm, "end": v(-5.05, -16.2) * mm});
            skLineSegment(sketch, "E955", {"start": v(-5.05, -16.2) * mm, "end": v(-5.41, -16.24) * mm});
            skLineSegment(sketch, "E956", {"start": v(-5.41, -16.24) * mm, "end": v(-5.72, -16) * mm});
            skLineSegment(sketch, "E957", {"start": v(-5.72, -16) * mm, "end": v(-5.78, -15.72) * mm});
            skLineSegment(sketch, "E958", {"start": v(-5.78, -15.72) * mm, "end": v(-5.72, -15.5) * mm});
            skLineSegment(sketch, "E959", {"start": v(-5.72, -15.5) * mm, "end": v(-5.53, -15.32) * mm});
            skLineSegment(sketch, "E960", {"start": v(-5.53, -15.32) * mm, "end": v(-3.48, -14.18) * mm});
            skLineSegment(sketch, "E961", {"start": v(-3.48, -14.18) * mm, "end": v(-3.44, -13.34) * mm});
            skLineSegment(sketch, "E962", {"start": v(-3.44, -13.34) * mm, "end": v(-4.65, -14.35) * mm});
            skLineSegment(sketch, "E963", {"start": v(-4.65, -14.35) * mm, "end": v(-5, -14.46) * mm});
            skLineSegment(sketch, "E964", {"start": v(-5, -14.46) * mm, "end": v(-5.33, -14.3) * mm});
            skLineSegment(sketch, "E965", {"start": v(-5.33, -14.3) * mm, "end": v(-5.46, -14.04) * mm});
            skLineSegment(sketch, "E966", {"start": v(-5.46, -14.04) * mm, "end": v(-5.44, -13.79) * mm});
            skLineSegment(sketch, "E967", {"start": v(-5.44, -13.79) * mm, "end": v(-5.3, -13.58) * mm});
            skLineSegment(sketch, "E968", {"start": v(-5.3, -13.58) * mm, "end": v(-3.5, -12.1) * mm});
            skLineSegment(sketch, "E969", {"start": v(-3.5, -12.1) * mm, "end": v(-3.63, -11.27) * mm});
            skLineSegment(sketch, "E970", {"start": v(-3.63, -11.27) * mm, "end": v(-4.6, -12.46) * mm});
            skLineSegment(sketch, "E971", {"start": v(-4.6, -12.46) * mm, "end": v(-4.93, -12.64) * mm});
            skLineSegment(sketch, "E972", {"start": v(-4.93, -12.64) * mm, "end": v(-5.3, -12.53) * mm});
            skLineSegment(sketch, "E973", {"start": v(-5.3, -12.53) * mm, "end": v(-5.46, -12.31) * mm});
            skLineSegment(sketch, "E974", {"start": v(-5.46, -12.31) * mm, "end": v(-5.48, -12.05) * mm});
            skLineSegment(sketch, "E975", {"start": v(-5.48, -12.05) * mm, "end": v(-5.38, -11.83) * mm});
            skLineSegment(sketch, "E976", {"start": v(-5.38, -11.83) * mm, "end": v(-3.92, -10.05) * mm});
            skLineSegment(sketch, "E977", {"start": v(-3.92, -10.05) * mm, "end": v(-4.18, -9.25) * mm});
            skLineSegment(sketch, "E978", {"start": v(-4.18, -9.25) * mm, "end": v(-4.92, -10.6) * mm});
            skLineSegment(sketch, "E979", {"start": v(-4.92, -10.6) * mm, "end": v(-5.2, -10.83) * mm});
            skLineSegment(sketch, "E980", {"start": v(-5.2, -10.83) * mm, "end": v(-5.57, -10.8) * mm});
            skLineSegment(sketch, "E981", {"start": v(-5.57, -10.8) * mm, "end": v(-5.78, -10.63) * mm});
            skLineSegment(sketch, "E982", {"start": v(-5.78, -10.63) * mm, "end": v(-5.86, -10.37) * mm});
            skLineSegment(sketch, "E983", {"start": v(-5.86, -10.37) * mm, "end": v(-5.8, -10.12) * mm});
            skLineSegment(sketch, "E984", {"start": v(-5.8, -10.12) * mm, "end": v(-4.7, -8.1) * mm});
            skLineSegment(sketch, "E985", {"start": v(-4.7, -8.1) * mm, "end": v(-5.1, -7.35) * mm});
            skLineSegment(sketch, "E986", {"start": v(-5.1, -7.35) * mm, "end": v(-5.58, -8.83) * mm});
            skLineSegment(sketch, "E987", {"start": v(-5.58, -8.83) * mm, "end": v(-5.81, -9.11) * mm});
            skLineSegment(sketch, "E988", {"start": v(-5.81, -9.11) * mm, "end": v(-6.2, -9.15) * mm});
            skLineSegment(sketch, "E989", {"start": v(-6.2, -9.15) * mm, "end": v(-6.42, -9) * mm});
            skLineSegment(sketch, "E990", {"start": v(-6.42, -9) * mm, "end": v(-6.54, -8.8) * mm});
            skLineSegment(sketch, "E991", {"start": v(-6.54, -8.8) * mm, "end": v(-6.53, -8.52) * mm});
            skLineSegment(sketch, "E992", {"start": v(-6.53, -8.52) * mm, "end": v(-5.81, -6.3) * mm});
            skLineSegment(sketch, "E993", {"start": v(-5.81, -6.3) * mm, "end": v(-6.36, -5.65) * mm});
            skLineSegment(sketch, "E994", {"start": v(-6.36, -5.65) * mm, "end": v(-6.55, -7.21) * mm});
            skLineSegment(sketch, "E995", {"start": v(-6.55, -7.21) * mm, "end": v(-6.73, -7.53) * mm});
            skLineSegment(sketch, "E996", {"start": v(-6.73, -7.53) * mm, "end": v(-7.09, -7.64) * mm});
            skLineSegment(sketch, "E997", {"start": v(-7.09, -7.64) * mm, "end": v(-7.35, -7.54) * mm});
            skLineSegment(sketch, "E998", {"start": v(-7.35, -7.54) * mm, "end": v(-7.5, -7.35) * mm});
            skLineSegment(sketch, "E999", {"start": v(-7.5, -7.35) * mm, "end": v(-7.54, -7.1) * mm});
            skLineSegment(sketch, "E1000", {"start": v(-7.54, -7.1) * mm, "end": v(-7.25, -4.74) * mm});
            skLineSegment(sketch, "E1001", {"start": v(-7.25, -4.74) * mm, "end": v(-7.92, -4.18) * mm});
            skLineSegment(sketch, "E1002", {"start": v(-7.92, -4.18) * mm, "end": v(-7.81, -5.8) * mm});
            skLineSegment(sketch, "E1003", {"start": v(-7.81, -5.8) * mm, "end": v(-7.93, -6.16) * mm});
            skLineSegment(sketch, "E1004", {"start": v(-7.93, -6.16) * mm, "end": v(-8.25, -6.33) * mm});
            skLineSegment(sketch, "E1005", {"start": v(-8.25, -6.33) * mm, "end": v(-8.53, -6.28) * mm});
            skLineSegment(sketch, "E1006", {"start": v(-8.53, -6.28) * mm, "end": v(-8.72, -6.12) * mm});
            skLineSegment(sketch, "E1007", {"start": v(-8.72, -6.12) * mm, "end": v(-8.8, -5.87) * mm});
            skLineSegment(sketch, "E1008", {"start": v(-8.8, -5.87) * mm, "end": v(-8.97, -3.46) * mm});
            skLineSegment(sketch, "E1009", {"start": v(-8.97, -3.46) * mm, "end": v(-9.74, -3.02) * mm});
            skLineSegment(sketch, "E1010", {"start": v(-9.74, -3.02) * mm, "end": v(-9.31, -4.66) * mm});
            skLineSegment(sketch, "E1011", {"start": v(-9.31, -4.66) * mm, "end": v(-9.36, -5.03) * mm});
            skLineSegment(sketch, "E1012", {"start": v(-9.36, -5.03) * mm, "end": v(-9.66, -5.26) * mm});
            skLineSegment(sketch, "E1013", {"start": v(-9.66, -5.26) * mm, "end": v(-9.92, -5.27) * mm});
            skLineSegment(sketch, "E1014", {"start": v(-9.92, -5.27) * mm, "end": v(-10.15, -5.14) * mm});
            skLineSegment(sketch, "E1015", {"start": v(-10.15, -5.14) * mm, "end": v(-10.28, -4.92) * mm});
            skLineSegment(sketch, "E1016", {"start": v(-10.28, -4.92) * mm, "end": v(-10.8, -2.93) * mm});
            skLineSegment(sketch, "E1017", {"start": v(-2.45, -20.5) * mm, "end": v(-2.44, -20.37) * mm});
            skLineSegment(sketch, "E1018", {"start": v(-2.44, -20.37) * mm, "end": v(-2.46, -20.25) * mm});
            skLineSegment(sketch, "E1019", {"start": v(-2.46, -20.25) * mm, "end": v(-2.49, -20.17) * mm});
            skLineSegment(sketch, "E1020", {"start": v(-2.49, -20.17) * mm, "end": v(-3.54, -18.12) * mm});
            skLineSegment(sketch, "E1021", {"start": v(-3.54, -18.12) * mm, "end": v(-3.33, -17.63) * mm});
            skLineSegment(sketch, "E1022", {"start": v(-3.33, -17.63) * mm, "end": v(-3.15, -17.14) * mm});
            skLineSegment(sketch, "E1023", {"start": v(-3.15, -17.14) * mm, "end": v(-2.18, -18.4) * mm});
            skLineSegment(sketch, "E1024", {"start": v(-2.18, -18.4) * mm, "end": v(-2.04, -18.51) * mm});
            skLineSegment(sketch, "E1025", {"start": v(-2.04, -18.51) * mm, "end": v(-1.9, -18.57) * mm});
            skLineSegment(sketch, "E1026", {"start": v(-1.9, -18.57) * mm, "end": v(-1.76, -18.58) * mm});
            skLineSegment(sketch, "E1027", {"start": v(-1.76, -18.58) * mm, "end": v(-1.63, -18.56) * mm});
            skLineSegment(sketch, "E1028", {"start": v(-1.63, -18.56) * mm, "end": v(-1.5, -18.49) * mm});
            skLineSegment(sketch, "E1029", {"start": v(-1.5, -18.49) * mm, "end": v(-1.39, -18.38) * mm});
            skLineSegment(sketch, "E1030", {"start": v(-1.39, -18.38) * mm, "end": v(-1.32, -18.24) * mm});
            skLineSegment(sketch, "E1031", {"start": v(-1.32, -18.24) * mm, "end": v(-1.29, -18.1) * mm});
            skLineSegment(sketch, "E1032", {"start": v(-1.29, -18.1) * mm, "end": v(-1.3, -17.96) * mm});
            skLineSegment(sketch, "E1033", {"start": v(-1.3, -17.96) * mm, "end": v(-1.34, -17.87) * mm});
            skLineSegment(sketch, "E1034", {"start": v(-1.34, -17.87) * mm, "end": v(-1.4, -17.78) * mm});
            skLineSegment(sketch, "E1035", {"start": v(-1.4, -17.78) * mm, "end": v(-2.8, -15.96) * mm});
            skLineSegment(sketch, "E1036", {"start": v(-2.8, -15.96) * mm, "end": v(-2.72, -15.56) * mm});
            skLineSegment(sketch, "E1037", {"start": v(-2.72, -15.56) * mm, "end": v(-2.61, -14.92) * mm});
            skLineSegment(sketch, "E1038", {"start": v(-2.61, -14.92) * mm, "end": v(-1.43, -15.97) * mm});
            skLineSegment(sketch, "E1039", {"start": v(-1.43, -15.97) * mm, "end": v(-1.27, -16.06) * mm});
            skLineSegment(sketch, "E1040", {"start": v(-1.27, -16.06) * mm, "end": v(-1.1, -16.1) * mm});
            skLineSegment(sketch, "E1041", {"start": v(-1.1, -16.1) * mm, "end": v(-0.96, -16.07) * mm});
            skLineSegment(sketch, "E1042", {"start": v(-0.96, -16.07) * mm, "end": v(-0.81, -16) * mm});
            skLineSegment(sketch, "E1043", {"start": v(-0.81, -16) * mm, "end": v(-0.68, -15.87) * mm});
            skLineSegment(sketch, "E1044", {"start": v(-0.68, -15.87) * mm, "end": v(-0.61, -15.7) * mm});
            skLineSegment(sketch, "E1045", {"start": v(-0.61, -15.7) * mm, "end": v(-0.6, -15.54) * mm});
            skLineSegment(sketch, "E1046", {"start": v(-0.6, -15.54) * mm, "end": v(-0.63, -15.42) * mm});
            skLineSegment(sketch, "E1047", {"start": v(-0.63, -15.42) * mm, "end": v(-0.7, -15.28) * mm});
            skLineSegment(sketch, "E1048", {"start": v(-0.7, -15.28) * mm, "end": v(-0.8, -15.2) * mm});
            skLineSegment(sketch, "E1049", {"start": v(-0.8, -15.2) * mm, "end": v(-2.5, -13.7) * mm});
            skLineSegment(sketch, "E1050", {"start": v(-2.5, -13.7) * mm, "end": v(-2.49, -13.25) * mm});
            skLineSegment(sketch, "E1051", {"start": v(-2.49, -13.25) * mm, "end": v(-2.5, -12.64) * mm});
            skLineSegment(sketch, "E1052", {"start": v(-2.5, -12.64) * mm, "end": v(-1.14, -13.45) * mm});
            skLineSegment(sketch, "E1053", {"start": v(-1.14, -13.45) * mm, "end": v(-1.03, -13.5) * mm});
            skLineSegment(sketch, "E1054", {"start": v(-1.03, -13.5) * mm, "end": v(-0.9, -13.52) * mm});
            skLineSegment(sketch, "E1055", {"start": v(-0.9, -13.52) * mm, "end": v(-0.77, -13.5) * mm});
            skLineSegment(sketch, "E1056", {"start": v(-0.77, -13.5) * mm, "end": v(-0.63, -13.45) * mm});
            skLineSegment(sketch, "E1057", {"start": v(-0.63, -13.45) * mm, "end": v(-0.52, -13.35) * mm});
            skLineSegment(sketch, "E1058", {"start": v(-0.52, -13.35) * mm, "end": v(-0.44, -13.25) * mm});
            skLineSegment(sketch, "E1059", {"start": v(-0.44, -13.25) * mm, "end": v(-0.4, -13.13) * mm});
            skLineSegment(sketch, "E1060", {"start": v(-0.4, -13.13) * mm, "end": v(-0.39, -13) * mm});
            skLineSegment(sketch, "E1061", {"start": v(-0.39, -13) * mm, "end": v(-0.41, -12.85) * mm});
            skLineSegment(sketch, "E1062", {"start": v(-0.41, -12.85) * mm, "end": v(-0.48, -12.72) * mm});
            skLineSegment(sketch, "E1063", {"start": v(-0.48, -12.72) * mm, "end": v(-0.56, -12.63) * mm});
            skLineSegment(sketch, "E1064", {"start": v(-0.56, -12.63) * mm, "end": v(-0.68, -12.56) * mm});
            skLineSegment(sketch, "E1065", {"start": v(-0.68, -12.56) * mm, "end": v(-2.61, -11.42) * mm});
            skLineSegment(sketch, "E1066", {"start": v(-2.61, -11.42) * mm, "end": v(-2.7, -10.86) * mm});
            skLineSegment(sketch, "E1067", {"start": v(-2.7, -10.86) * mm, "end": v(-2.81, -10.38) * mm});
            skLineSegment(sketch, "E1068", {"start": v(-2.81, -10.38) * mm, "end": v(-1.27, -10.93) * mm});
            skLineSegment(sketch, "E1069", {"start": v(-1.27, -10.93) * mm, "end": v(-1.14, -10.95) * mm});
            skLineSegment(sketch, "E1070", {"start": v(-1.14, -10.95) * mm, "end": v(-1, -10.92) * mm});
            skLineSegment(sketch, "E1071", {"start": v(-1, -10.92) * mm, "end": v(-0.87, -10.86) * mm});
            skLineSegment(sketch, "E1072", {"start": v(-0.87, -10.86) * mm, "end": v(-0.78, -10.77) * mm});
            skLineSegment(sketch, "E1073", {"start": v(-0.78, -10.77) * mm, "end": v(-0.7, -10.65) * mm});
            skLineSegment(sketch, "E1074", {"start": v(-0.7, -10.65) * mm, "end": v(-0.66, -10.49) * mm});
            skLineSegment(sketch, "E1075", {"start": v(-0.66, -10.49) * mm, "end": v(-0.67, -10.33) * mm});
            skLineSegment(sketch, "E1076", {"start": v(-0.67, -10.33) * mm, "end": v(-0.75, -10.16) * mm});
            skLineSegment(sketch, "E1077", {"start": v(-0.75, -10.16) * mm, "end": v(-0.86, -10.05) * mm});
            skLineSegment(sketch, "E1078", {"start": v(-0.86, -10.05) * mm, "end": v(-1.05, -9.96) * mm});
            skLineSegment(sketch, "E1079", {"start": v(-1.05, -9.96) * mm, "end": v(-3.16, -9.2) * mm});
            skLineSegment(sketch, "E1080", {"start": v(-3.16, -9.2) * mm, "end": v(-3.54, -8.22) * mm});
            skLineSegment(sketch, "E1081", {"start": v(-3.54, -8.22) * mm, "end": v(-1.98, -8.47) * mm});
            skLineSegment(sketch, "E1082", {"start": v(-1.98, -8.47) * mm, "end": v(-1.79, -8.46) * mm});
            skLineSegment(sketch, "E1083", {"start": v(-1.79, -8.46) * mm, "end": v(-1.62, -8.39) * mm});
            skLineSegment(sketch, "E1084", {"start": v(-1.62, -8.39) * mm, "end": v(-1.48, -8.24) * mm});
            skLineSegment(sketch, "E1085", {"start": v(-1.48, -8.24) * mm, "end": v(-1.41, -8.04) * mm});
            skLineSegment(sketch, "E1086", {"start": v(-1.41, -8.04) * mm, "end": v(-1.43, -7.83) * mm});
            skLineSegment(sketch, "E1087", {"start": v(-1.43, -7.83) * mm, "end": v(-1.54, -7.64) * mm});
            skLineSegment(sketch, "E1088", {"start": v(-1.54, -7.64) * mm, "end": v(-1.67, -7.53) * mm});
            skLineSegment(sketch, "E1089", {"start": v(-1.67, -7.53) * mm, "end": v(-1.88, -7.47) * mm});
            skLineSegment(sketch, "E1090", {"start": v(-1.88, -7.47) * mm, "end": v(-4.1, -7.12) * mm});
            skLineSegment(sketch, "E1091", {"start": v(-4.1, -7.12) * mm, "end": v(-4.34, -6.72) * mm});
            skLineSegment(sketch, "E1092", {"start": v(-4.34, -6.72) * mm, "end": v(-4.67, -6.24) * mm});
            skLineSegment(sketch, "E1093", {"start": v(-4.67, -6.24) * mm, "end": v(-3.09, -6.19) * mm});
            skLineSegment(sketch, "E1094", {"start": v(-3.09, -6.19) * mm, "end": v(-2.89, -6.14) * mm});
            skLineSegment(sketch, "E1095", {"start": v(-2.89, -6.14) * mm, "end": v(-2.73, -6.02) * mm});
            skLineSegment(sketch, "E1096", {"start": v(-2.73, -6.02) * mm, "end": v(-2.64, -5.85) * mm});
            skLineSegment(sketch, "E1097", {"start": v(-2.64, -5.85) * mm, "end": v(-2.61, -5.7) * mm});
            skLineSegment(sketch, "E1098", {"start": v(-2.61, -5.7) * mm, "end": v(-2.65, -5.48) * mm});
            skLineSegment(sketch, "E1099", {"start": v(-2.65, -5.48) * mm, "end": v(-2.76, -5.33) * mm});
            skLineSegment(sketch, "E1100", {"start": v(-2.76, -5.33) * mm, "end": v(-2.9, -5.23) * mm});
            skLineSegment(sketch, "E1101", {"start": v(-2.9, -5.23) * mm, "end": v(-3.06, -5.19) * mm});
            skLineSegment(sketch, "E1102", {"start": v(-3.06, -5.19) * mm, "end": v(-5.43, -5.26) * mm});
            skLineSegment(sketch, "E1103", {"start": v(-5.43, -5.26) * mm, "end": v(-5.78, -4.87) * mm});
            skLineSegment(sketch, "E1104", {"start": v(-5.78, -4.87) * mm, "end": v(-6.14, -4.5) * mm});
            skLineSegment(sketch, "E1105", {"start": v(-6.14, -4.5) * mm, "end": v(-4.6, -4.15) * mm});
            skLineSegment(sketch, "E1106", {"start": v(-4.6, -4.15) * mm, "end": v(-4.4, -4.05) * mm});
            skLineSegment(sketch, "E1107", {"start": v(-4.4, -4.05) * mm, "end": v(-4.25, -3.84) * mm});
            skLineSegment(sketch, "E1108", {"start": v(-4.25, -3.84) * mm, "end": v(-4.23, -3.58) * mm});
            skLineSegment(sketch, "E1109", {"start": v(-4.23, -3.58) * mm, "end": v(-4.31, -3.37) * mm});
            skLineSegment(sketch, "E1110", {"start": v(-4.31, -3.37) * mm, "end": v(-4.44, -3.25) * mm});
            skLineSegment(sketch, "E1111", {"start": v(-4.44, -3.25) * mm, "end": v(-4.62, -3.17) * mm});
            skLineSegment(sketch, "E1112", {"start": v(-4.62, -3.17) * mm, "end": v(-4.79, -3.17) * mm});
            skLineSegment(sketch, "E1113", {"start": v(-4.79, -3.17) * mm, "end": v(-7.07, -3.68) * mm});
            skLineSegment(sketch, "E1114", {"start": v(-7.07, -3.68) * mm, "end": v(-7.49, -3.36) * mm});
            skLineSegment(sketch, "E1115", {"start": v(-7.49, -3.36) * mm, "end": v(-7.92, -3.06) * mm});
            skLineSegment(sketch, "E1116", {"start": v(-7.92, -3.06) * mm, "end": v(-6.47, -2.44) * mm});
            skLineSegment(sketch, "E1117", {"start": v(-6.47, -2.44) * mm, "end": v(-6.33, -2.34) * mm});
            skLineSegment(sketch, "E1118", {"start": v(-6.33, -2.34) * mm, "end": v(-6.21, -2.17) * mm});
            skLineSegment(sketch, "E1119", {"start": v(-6.21, -2.17) * mm, "end": v(-6.17, -1.96) * mm});
            skLineSegment(sketch, "E1120", {"start": v(-6.17, -1.96) * mm, "end": v(-6.21, -1.8) * mm});
            skLineSegment(sketch, "E1121", {"start": v(-6.21, -1.8) * mm, "end": v(-6.31, -1.63) * mm});
            skLineSegment(sketch, "E1122", {"start": v(-6.31, -1.63) * mm, "end": v(-6.44, -1.54) * mm});
            skLineSegment(sketch, "E1123", {"start": v(-6.44, -1.54) * mm, "end": v(-6.57, -1.49) * mm});
            skLineSegment(sketch, "E1124", {"start": v(-6.57, -1.49) * mm, "end": v(-6.72, -1.48) * mm});
            skLineSegment(sketch, "E1125", {"start": v(-6.72, -1.48) * mm, "end": v(-6.9, -1.53) * mm});
            skLineSegment(sketch, "E1126", {"start": v(-6.9, -1.53) * mm, "end": v(-8.9, -2.4) * mm});
            skLineSegment(sketch, "E1127", {"start": v(-8.9, -2.4) * mm, "end": v(-9.02, -2.32) * mm});
            skLineSegment(sketch, "E1128", {"start": v(-9.02, -2.32) * mm, "end": v(-9.15, -2.25) * mm});
            skLineSegment(sketch, "E1129", {"start": v(-9.15, -2.25) * mm, "end": v(-7.66, -1.59) * mm});
            skLineSegment(sketch, "E1130", {"start": v(-7.66, -1.59) * mm, "end": v(-6.89, -1.26) * mm});
            skLineSegment(sketch, "E1131", {"start": v(-6.89, -1.26) * mm, "end": v(-6.72, -1.23) * mm});
            skLineSegment(sketch, "E1132", {"start": v(-6.72, -1.23) * mm, "end": v(-5.18, -1.01) * mm});
            skLineSegment(sketch, "E1133", {"start": v(-5.18, -1.01) * mm, "end": v(-3.55, -1) * mm});
            skLineSegment(sketch, "E1134", {"start": v(-3.55, -1) * mm, "end": v(-1.47, -1.27) * mm});
            skLineSegment(sketch, "E1135", {"start": v(-1.47, -1.27) * mm, "end": v(1, -1.87) * mm});
            skLineSegment(sketch, "E1136", {"start": v(1, -1.87) * mm, "end": v(4.45, -3.3) * mm});
            skLineSegment(sketch, "E1137", {"start": v(4.45, -3.3) * mm, "end": v(6.84, -4.9) * mm});
            skLineSegment(sketch, "E1138", {"start": v(6.84, -4.9) * mm, "end": v(7.9, -5.75) * mm});
            skLineSegment(sketch, "E1139", {"start": v(7.9, -5.75) * mm, "end": v(8.35, -6.36) * mm});
            skLineSegment(sketch, "E1140", {"start": v(8.35, -6.36) * mm, "end": v(8.6, -7.12) * mm});
            skLineSegment(sketch, "E1141", {"start": v(8.6, -7.12) * mm, "end": v(8.3, -7.87) * mm});
            skLineSegment(sketch, "E1142", {"start": v(8.3, -7.87) * mm, "end": v(7.72, -6.35) * mm});
            skLineSegment(sketch, "E1143", {"start": v(7.72, -6.35) * mm, "end": v(7.62, -6.2) * mm});
            skLineSegment(sketch, "E1144", {"start": v(7.62, -6.2) * mm, "end": v(7.46, -6.08) * mm});
            skLineSegment(sketch, "E1145", {"start": v(7.46, -6.08) * mm, "end": v(7.28, -6.03) * mm});
            skLineSegment(sketch, "E1146", {"start": v(7.28, -6.03) * mm, "end": v(7.1, -6.06) * mm});
            skLineSegment(sketch, "E1147", {"start": v(7.1, -6.06) * mm, "end": v(6.94, -6.14) * mm});
            skLineSegment(sketch, "E1148", {"start": v(6.94, -6.14) * mm, "end": v(6.82, -6.28) * mm});
            skLineSegment(sketch, "E1149", {"start": v(6.82, -6.28) * mm, "end": v(6.76, -6.43) * mm});
            skLineSegment(sketch, "E1150", {"start": v(6.76, -6.43) * mm, "end": v(6.75, -6.58) * mm});
            skLineSegment(sketch, "E1151", {"start": v(6.75, -6.58) * mm, "end": v(6.79, -6.7) * mm});
            skLineSegment(sketch, "E1152", {"start": v(6.79, -6.7) * mm, "end": v(7.8, -9.31) * mm});
            skLineSegment(sketch, "E1153", {"start": v(7.8, -9.31) * mm, "end": v(7.73, -9.52) * mm});
            skLineSegment(sketch, "E1154", {"start": v(7.73, -9.52) * mm, "end": v(7.67, -9.72) * mm});
            skLineSegment(sketch, "E1155", {"start": v(7.67, -9.72) * mm, "end": v(6.93, -8.17) * mm});
            skLineSegment(sketch, "E1156", {"start": v(6.93, -8.17) * mm, "end": v(6.84, -8.07) * mm});
            skLineSegment(sketch, "E1157", {"start": v(6.84, -8.07) * mm, "end": v(6.7, -8) * mm});
            skLineSegment(sketch, "E1158", {"start": v(6.7, -8) * mm, "end": v(6.53, -7.96) * mm});
            skLineSegment(sketch, "E1159", {"start": v(6.53, -7.96) * mm, "end": v(6.38, -7.98) * mm});
            skLineSegment(sketch, "E1160", {"start": v(6.38, -7.98) * mm, "end": v(6.22, -8.06) * mm});
            skLineSegment(sketch, "E1161", {"start": v(6.22, -8.06) * mm, "end": v(6.1, -8.18) * mm});
            skLineSegment(sketch, "E1162", {"start": v(6.1, -8.18) * mm, "end": v(6.06, -8.28) * mm});
            skLineSegment(sketch, "E1163", {"start": v(6.06, -8.28) * mm, "end": v(6.02, -8.42) * mm});
            skLineSegment(sketch, "E1164", {"start": v(6.02, -8.42) * mm, "end": v(6.03, -8.56) * mm});
            skLineSegment(sketch, "E1165", {"start": v(6.03, -8.56) * mm, "end": v(6.1, -8.72) * mm});
            skLineSegment(sketch, "E1166", {"start": v(6.1, -8.72) * mm, "end": v(7.25, -11.2) * mm});
            skLineSegment(sketch, "E1167", {"start": v(7.25, -11.2) * mm, "end": v(7.2, -11.4) * mm});
            skLineSegment(sketch, "E1168", {"start": v(7.2, -11.4) * mm, "end": v(7.15, -11.62) * mm});
            skLineSegment(sketch, "E1169", {"start": v(7.15, -11.62) * mm, "end": v(6.36, -10.18) * mm});
            skLineSegment(sketch, "E1170", {"start": v(6.36, -10.18) * mm, "end": v(6.28, -10.08) * mm});
            skLineSegment(sketch, "E1171", {"start": v(6.28, -10.08) * mm, "end": v(6.15, -9.98) * mm});
            skLineSegment(sketch, "E1172", {"start": v(6.15, -9.98) * mm, "end": v(5.98, -9.93) * mm});
            skLineSegment(sketch, "E1173", {"start": v(5.98, -9.93) * mm, "end": v(5.78, -9.95) * mm});
            skLineSegment(sketch, "E1174", {"start": v(5.78, -9.95) * mm, "end": v(5.63, -10.02) * mm});
            skLineSegment(sketch, "E1175", {"start": v(5.63, -10.02) * mm, "end": v(5.5, -10.17) * mm});
            skLineSegment(sketch, "E1176", {"start": v(5.5, -10.17) * mm, "end": v(5.43, -10.31) * mm});
            skLineSegment(sketch, "E1177", {"start": v(5.43, -10.31) * mm, "end": v(5.42, -10.45) * mm});
            skLineSegment(sketch, "E1178", {"start": v(5.42, -10.45) * mm, "end": v(5.46, -10.62) * mm});
            skLineSegment(sketch, "E1179", {"start": v(5.46, -10.62) * mm, "end": v(5.51, -10.72) * mm});
            skLineSegment(sketch, "E1180", {"start": v(5.51, -10.72) * mm, "end": v(6.83, -13.1) * mm});
            skLineSegment(sketch, "E1181", {"start": v(6.83, -13.1) * mm, "end": v(6.75, -13.54) * mm});
            skLineSegment(sketch, "E1182", {"start": v(6.75, -13.54) * mm, "end": v(5.81, -12.09) * mm});
            skLineSegment(sketch, "E1183", {"start": v(5.81, -12.09) * mm, "end": v(5.7, -12) * mm});
            skLineSegment(sketch, "E1184", {"start": v(5.7, -12) * mm, "end": v(5.5, -11.93) * mm});
            skLineSegment(sketch, "E1185", {"start": v(5.5, -11.93) * mm, "end": v(5.3, -11.95) * mm});
            skLineSegment(sketch, "E1186", {"start": v(5.3, -11.95) * mm, "end": v(5.16, -12.03) * mm});
            skLineSegment(sketch, "E1187", {"start": v(5.16, -12.03) * mm, "end": v(5.04, -12.15) * mm});
            skLineSegment(sketch, "E1188", {"start": v(5.04, -12.15) * mm, "end": v(4.96, -12.31) * mm});
            skLineSegment(sketch, "E1189", {"start": v(4.96, -12.31) * mm, "end": v(4.95, -12.47) * mm});
            skLineSegment(sketch, "E1190", {"start": v(4.95, -12.47) * mm, "end": v(4.98, -12.58) * mm});
            skLineSegment(sketch, "E1191", {"start": v(4.98, -12.58) * mm, "end": v(5.04, -12.7) * mm});
            skLineSegment(sketch, "E1192", {"start": v(5.04, -12.7) * mm, "end": v(6.53, -15.05) * mm});
            skLineSegment(sketch, "E1193", {"start": v(6.53, -15.05) * mm, "end": v(6.48, -15.48) * mm});
            skLineSegment(sketch, "E1194", {"start": v(6.48, -15.48) * mm, "end": v(5.51, -14.16) * mm});
            skLineSegment(sketch, "E1195", {"start": v(5.51, -14.16) * mm, "end": v(5.4, -14.05) * mm});
            skLineSegment(sketch, "E1196", {"start": v(5.4, -14.05) * mm, "end": v(5.2, -13.97) * mm});
            skLineSegment(sketch, "E1197", {"start": v(5.2, -13.97) * mm, "end": v(5.04, -13.97) * mm});
            skLineSegment(sketch, "E1198", {"start": v(5.04, -13.97) * mm, "end": v(4.84, -14.04) * mm});
            skLineSegment(sketch, "E1199", {"start": v(4.84, -14.04) * mm, "end": v(4.7, -14.17) * mm});
            skLineSegment(sketch, "E1200", {"start": v(4.7, -14.17) * mm, "end": v(4.64, -14.3) * mm});
            skLineSegment(sketch, "E1201", {"start": v(4.64, -14.3) * mm, "end": v(4.61, -14.47) * mm});
            skLineSegment(sketch, "E1202", {"start": v(4.61, -14.47) * mm, "end": v(4.64, -14.62) * mm});
            skLineSegment(sketch, "E1203", {"start": v(4.64, -14.62) * mm, "end": v(4.7, -14.75) * mm});
            skLineSegment(sketch, "E1204", {"start": v(4.7, -14.75) * mm, "end": v(6.36, -17) * mm});
            skLineSegment(sketch, "E1205", {"start": v(6.36, -17) * mm, "end": v(6.34, -17.44) * mm});
            skLineSegment(sketch, "E1206", {"start": v(6.34, -17.44) * mm, "end": v(5.29, -16.18) * mm});
            skLineSegment(sketch, "E1207", {"start": v(5.29, -16.18) * mm, "end": v(5.17, -16.08) * mm});
            skLineSegment(sketch, "E1208", {"start": v(5.17, -16.08) * mm, "end": v(5.04, -16.02) * mm});
            skLineSegment(sketch, "E1209", {"start": v(5.04, -16.02) * mm, "end": v(4.9, -16) * mm});
            skLineSegment(sketch, "E1210", {"start": v(4.9, -16) * mm, "end": v(4.76, -16.03) * mm});
            skLineSegment(sketch, "E1211", {"start": v(4.76, -16.03) * mm, "end": v(4.6, -16.11) * mm});
            skLineSegment(sketch, "E1212", {"start": v(4.6, -16.11) * mm, "end": v(4.49, -16.24) * mm});
            skLineSegment(sketch, "E1213", {"start": v(4.49, -16.24) * mm, "end": v(4.42, -16.38) * mm});
            skLineSegment(sketch, "E1214", {"start": v(4.42, -16.38) * mm, "end": v(4.4, -16.54) * mm});
            skLineSegment(sketch, "E1215", {"start": v(4.4, -16.54) * mm, "end": v(4.45, -16.72) * mm});
            skLineSegment(sketch, "E1216", {"start": v(4.45, -16.72) * mm, "end": v(4.58, -16.9) * mm});
            skLineSegment(sketch, "E1217", {"start": v(4.58, -16.9) * mm, "end": v(5.75, -18.28) * mm});
            skLineSegment(sketch, "E1218", {"start": v(5.75, -18.28) * mm, "end": v(5.6, -18.4) * mm});
            skLineSegment(sketch, "E1219", {"start": v(5.6, -18.4) * mm, "end": v(5.45, -18.48) * mm});
            skLineSegment(sketch, "E1220", {"start": v(5.45, -18.48) * mm, "end": v(5.2, -18.22) * mm});
            skLineSegment(sketch, "E1221", {"start": v(5.2, -18.22) * mm, "end": v(5.07, -18.12) * mm});
            skLineSegment(sketch, "E1222", {"start": v(5.07, -18.12) * mm, "end": v(4.91, -18.07) * mm});
            skLineSegment(sketch, "E1223", {"start": v(4.91, -18.07) * mm, "end": v(4.7, -18.08) * mm});
            skLineSegment(sketch, "E1224", {"start": v(4.7, -18.08) * mm, "end": v(4.55, -18.15) * mm});
            skLineSegment(sketch, "E1225", {"start": v(4.55, -18.15) * mm, "end": v(4.43, -18.27) * mm});
            skLineSegment(sketch, "E1226", {"start": v(4.43, -18.27) * mm, "end": v(4.36, -18.41) * mm});
            skLineSegment(sketch, "E1227", {"start": v(4.36, -18.41) * mm, "end": v(4.34, -18.6) * mm});
            skLineSegment(sketch, "E1228", {"start": v(4.34, -18.6) * mm, "end": v(4.35, -18.7) * mm});
            skLineSegment(sketch, "E1229", {"start": v(4.35, -18.7) * mm, "end": v(4.42, -18.84) * mm});
            skLineSegment(sketch, "E1230", {"start": v(4.42, -18.84) * mm, "end": v(4.5, -18.93) * mm});
            skLineSegment(sketch, "E1231", {"start": v(4.5, -18.93) * mm, "end": v(1.9, -19.74) * mm});
            skLineSegment(sketch, "E1232", {"start": v(1.9, -19.74) * mm, "end": v(-1.24, -20.4) * mm});
            skLineSegment(sketch, "E1233", {"start": v(-1.24, -20.4) * mm, "end": v(-2.45, -20.5) * mm});
            skLineSegment(sketch, "E1234", {"start": v(8.34, 27.45) * mm, "end": v(12.72, 27.14) * mm});
            skLineSegment(sketch, "E1235", {"start": v(12.72, 27.14) * mm, "end": v(19.28, 26.81) * mm});
            skLineSegment(sketch, "E1236", {"start": v(19.28, 26.81) * mm, "end": v(21.33, 26.66) * mm});
            skLineSegment(sketch, "E1237", {"start": v(21.33, 26.66) * mm, "end": v(21.92, 26.5) * mm});
            skLineSegment(sketch, "E1238", {"start": v(21.92, 26.5) * mm, "end": v(22.15, 26.34) * mm});
            skLineSegment(sketch, "E1239", {"start": v(22.15, 26.34) * mm, "end": v(22.16, 26.24) * mm});
            skLineSegment(sketch, "E1240", {"start": v(22.16, 26.24) * mm, "end": v(22.06, 26.16) * mm});
            skLineSegment(sketch, "E1241", {"start": v(22.06, 26.16) * mm, "end": v(21.67, 26.06) * mm});
            skLineSegment(sketch, "E1242", {"start": v(21.67, 26.06) * mm, "end": v(20.58, 25.99) * mm});
            skLineSegment(sketch, "E1243", {"start": v(20.58, 25.99) * mm, "end": v(18.5, 25.88) * mm});
            skLineSegment(sketch, "E1244", {"start": v(18.5, 25.88) * mm, "end": v(17.45, 25.71) * mm});
            skLineSegment(sketch, "E1245", {"start": v(17.45, 25.71) * mm, "end": v(16.94, 25.53) * mm});
            skLineSegment(sketch, "E1246", {"start": v(16.94, 25.53) * mm, "end": v(16.55, 25.22) * mm});
            skLineSegment(sketch, "E1247", {"start": v(16.55, 25.22) * mm, "end": v(16.31, 24.97) * mm});
            skLineSegment(sketch, "E1248", {"start": v(16.31, 24.97) * mm, "end": v(16.07, 24.8) * mm});
            skLineSegment(sketch, "E1249", {"start": v(16.07, 24.8) * mm, "end": v(15.71, 24.63) * mm});
            skLineSegment(sketch, "E1250", {"start": v(15.71, 24.63) * mm, "end": v(15.58, 24.53) * mm});
            skLineSegment(sketch, "E1251", {"start": v(15.58, 24.53) * mm, "end": v(15.55, 24.46) * mm});
            skLineSegment(sketch, "E1252", {"start": v(15.55, 24.46) * mm, "end": v(15.6, 24.35) * mm});
            skLineSegment(sketch, "E1253", {"start": v(15.6, 24.35) * mm, "end": v(15.87, 24.12) * mm});
            skLineSegment(sketch, "E1254", {"start": v(15.87, 24.12) * mm, "end": v(16.3, 23.9) * mm});
            skLineSegment(sketch, "E1255", {"start": v(16.3, 23.9) * mm, "end": v(16.66, 23.78) * mm});
            skLineSegment(sketch, "E1256", {"start": v(16.66, 23.78) * mm, "end": v(17.2, 23.7) * mm});
            skLineSegment(sketch, "E1257", {"start": v(17.2, 23.7) * mm, "end": v(17.67, 23.62) * mm});
            skLineSegment(sketch, "E1258", {"start": v(17.67, 23.62) * mm, "end": v(18.44, 23.31) * mm});
            skLineSegment(sketch, "E1259", {"start": v(18.44, 23.31) * mm, "end": v(19.18, 22.84) * mm});
            skLineSegment(sketch, "E1260", {"start": v(19.18, 22.84) * mm, "end": v(19.6, 22.44) * mm});
            skLineSegment(sketch, "E1261", {"start": v(19.6, 22.44) * mm, "end": v(19.9, 21.87) * mm});
            skLineSegment(sketch, "E1262", {"start": v(19.9, 21.87) * mm, "end": v(19.88, 21.42) * mm});
            skLineSegment(sketch, "E1263", {"start": v(19.88, 21.42) * mm, "end": v(19.66, 21.03) * mm});
            skLineSegment(sketch, "E1264", {"start": v(19.66, 21.03) * mm, "end": v(19.14, 20.43) * mm});
            skLineSegment(sketch, "E1265", {"start": v(19.14, 20.43) * mm, "end": v(18.95, 20.26) * mm});
            skLineSegment(sketch, "E1266", {"start": v(18.95, 20.26) * mm, "end": v(18.77, 20.18) * mm});
            skLineSegment(sketch, "E1267", {"start": v(18.77, 20.18) * mm, "end": v(18.61, 20.17) * mm});
            skLineSegment(sketch, "E1268", {"start": v(18.61, 20.17) * mm, "end": v(18.33, 20.3) * mm});
            skLineSegment(sketch, "E1269", {"start": v(18.33, 20.3) * mm, "end": v(18, 20.67) * mm});
            skLineSegment(sketch, "E1270", {"start": v(18, 20.67) * mm, "end": v(17.52, 21.38) * mm});
            skLineSegment(sketch, "E1271", {"start": v(17.52, 21.38) * mm, "end": v(16.98, 22.06) * mm});
            skLineSegment(sketch, "E1272", {"start": v(16.98, 22.06) * mm, "end": v(16.4, 22.58) * mm});
            skLineSegment(sketch, "E1273", {"start": v(16.4, 22.58) * mm, "end": v(15.56, 23.11) * mm});
            skLineSegment(sketch, "E1274", {"start": v(15.56, 23.11) * mm, "end": v(14.24, 23.73) * mm});
            skLineSegment(sketch, "E1275", {"start": v(14.24, 23.73) * mm, "end": v(11.77, 24.74) * mm});
            skLineSegment(sketch, "E1276", {"start": v(11.77, 24.74) * mm, "end": v(10.2, 25.53) * mm});
            skLineSegment(sketch, "E1277", {"start": v(10.2, 25.53) * mm, "end": v(8.18, 26.73) * mm});
            skLineSegment(sketch, "E1278", {"start": v(8.18, 26.73) * mm, "end": v(7.77, 27.04) * mm});
            skLineSegment(sketch, "E1279", {"start": v(7.77, 27.04) * mm, "end": v(7.64, 27.23) * mm});
            skLineSegment(sketch, "E1280", {"start": v(7.64, 27.23) * mm, "end": v(7.76, 27.38) * mm});
            skLineSegment(sketch, "E1281", {"start": v(7.76, 27.38) * mm, "end": v(8.34, 27.45) * mm});
            skLineSegment(sketch, "E1282", {"start": v(7.12, 28.55) * mm, "end": v(8.83, 28.8) * mm});
            skLineSegment(sketch, "E1283", {"start": v(8.83, 28.8) * mm, "end": v(10.05, 28.86) * mm});
            skLineSegment(sketch, "E1284", {"start": v(10.05, 28.86) * mm, "end": v(11, 28.8) * mm});
            skLineSegment(sketch, "E1285", {"start": v(11, 28.8) * mm, "end": v(12.22, 28.55) * mm});
            skLineSegment(sketch, "E1286", {"start": v(12.22, 28.55) * mm, "end": v(13.45, 28.29) * mm});
            skLineSegment(sketch, "E1287", {"start": v(13.45, 28.29) * mm, "end": v(14.42, 28.21) * mm});
            skLineSegment(sketch, "E1288", {"start": v(14.42, 28.21) * mm, "end": v(15.11, 28.27) * mm});
            skLineSegment(sketch, "E1289", {"start": v(15.11, 28.27) * mm, "end": v(15.5, 28.4) * mm});
            skLineSegment(sketch, "E1290", {"start": v(15.5, 28.4) * mm, "end": v(15.6, 28.5) * mm});
            skLineSegment(sketch, "E1291", {"start": v(15.6, 28.5) * mm, "end": v(15.53, 28.68) * mm});
            skLineSegment(sketch, "E1292", {"start": v(15.53, 28.68) * mm, "end": v(15.1, 29) * mm});
            skLineSegment(sketch, "E1293", {"start": v(15.1, 29) * mm, "end": v(14.04, 29.45) * mm});
            skLineSegment(sketch, "E1294", {"start": v(14.04, 29.45) * mm, "end": v(13.04, 29.73) * mm});
            skLineSegment(sketch, "E1295", {"start": v(13.04, 29.73) * mm, "end": v(11.44, 30.02) * mm});
            skLineSegment(sketch, "E1296", {"start": v(11.44, 30.02) * mm, "end": v(10.04, 30.12) * mm});
            skLineSegment(sketch, "E1297", {"start": v(10.04, 30.12) * mm, "end": v(8.87, 30.06) * mm});
            skLineSegment(sketch, "E1298", {"start": v(8.87, 30.06) * mm, "end": v(7.58, 29.78) * mm});
            skLineSegment(sketch, "E1299", {"start": v(7.58, 29.78) * mm, "end": v(6.54, 29.4) * mm});
            skLineSegment(sketch, "E1300", {"start": v(6.54, 29.4) * mm, "end": v(5.94, 29.07) * mm});
            skLineSegment(sketch, "E1301", {"start": v(5.94, 29.07) * mm, "end": v(5.53, 28.74) * mm});
            skLineSegment(sketch, "E1302", {"start": v(5.53, 28.74) * mm, "end": v(5.45, 28.59) * mm});
            skLineSegment(sketch, "E1303", {"start": v(5.45, 28.59) * mm, "end": v(5.5, 28.5) * mm});
            skLineSegment(sketch, "E1304", {"start": v(5.5, 28.5) * mm, "end": v(5.62, 28.44) * mm});
            skLineSegment(sketch, "E1305", {"start": v(5.62, 28.44) * mm, "end": v(5.93, 28.4) * mm});
            skLineSegment(sketch, "E1306", {"start": v(5.93, 28.4) * mm, "end": v(6.43, 28.45) * mm});
            skLineSegment(sketch, "E1307", {"start": v(6.43, 28.45) * mm, "end": v(7.12, 28.55) * mm});
            skLineSegment(sketch, "E1308", {"start": v(-10.66, 27.3) * mm, "end": v(-9.46, 27.82) * mm});
            skLineSegment(sketch, "E1309", {"start": v(-9.46, 27.82) * mm, "end": v(-7.3, 28.35) * mm});
            skLineSegment(sketch, "E1310", {"start": v(-7.3, 28.35) * mm, "end": v(-4.46, 28.7) * mm});
            skLineSegment(sketch, "E1311", {"start": v(-4.46, 28.7) * mm, "end": v(-0.96, 28.68) * mm});
            skLineSegment(sketch, "E1312", {"start": v(-0.96, 28.68) * mm, "end": v(0.4, 28.7) * mm});
            skLineSegment(sketch, "E1313", {"start": v(0.4, 28.7) * mm, "end": v(0.73, 28.76) * mm});
            skLineSegment(sketch, "E1314", {"start": v(0.73, 28.76) * mm, "end": v(0.88, 28.84) * mm});
            skLineSegment(sketch, "E1315", {"start": v(0.88, 28.84) * mm, "end": v(0.9, 28.96) * mm});
            skLineSegment(sketch, "E1316", {"start": v(0.9, 28.96) * mm, "end": v(0.8, 29.1) * mm});
            skLineSegment(sketch, "E1317", {"start": v(0.8, 29.1) * mm, "end": v(0.34, 29.39) * mm});
            skLineSegment(sketch, "E1318", {"start": v(0.34, 29.39) * mm, "end": v(-0.55, 29.78) * mm});
            skLineSegment(sketch, "E1319", {"start": v(-0.55, 29.78) * mm, "end": v(-1.72, 30.15) * mm});
            skLineSegment(sketch, "E1320", {"start": v(-1.72, 30.15) * mm, "end": v(-2.79, 30.38) * mm});
            skLineSegment(sketch, "E1321", {"start": v(-2.79, 30.38) * mm, "end": v(-4.31, 30.51) * mm});
            skLineSegment(sketch, "E1322", {"start": v(-4.31, 30.51) * mm, "end": v(-6.03, 30.38) * mm});
            skLineSegment(sketch, "E1323", {"start": v(-6.03, 30.38) * mm, "end": v(-7.64, 30.03) * mm});
            skLineSegment(sketch, "E1324", {"start": v(-7.64, 30.03) * mm, "end": v(-9.64, 29.36) * mm});
            skLineSegment(sketch, "E1325", {"start": v(-9.64, 29.36) * mm, "end": v(-11.48, 28.49) * mm});
            skLineSegment(sketch, "E1326", {"start": v(-11.48, 28.49) * mm, "end": v(-12.65, 27.67) * mm});
            skLineSegment(sketch, "E1327", {"start": v(-12.65, 27.67) * mm, "end": v(-13.85, 26.46) * mm});
            skLineSegment(sketch, "E1328", {"start": v(-13.85, 26.46) * mm, "end": v(-14.67, 25.22) * mm});
            skLineSegment(sketch, "E1329", {"start": v(-14.67, 25.22) * mm, "end": v(-15.16, 24.18) * mm});
            skLineSegment(sketch, "E1330", {"start": v(-15.16, 24.18) * mm, "end": v(-15.36, 23.6) * mm});
            skLineSegment(sketch, "E1331", {"start": v(-15.36, 23.6) * mm, "end": v(-15.4, 23.36) * mm});
            skLineSegment(sketch, "E1332", {"start": v(-15.4, 23.36) * mm, "end": v(-15.36, 23.28) * mm});
            skLineSegment(sketch, "E1333", {"start": v(-15.36, 23.28) * mm, "end": v(-15.28, 23.27) * mm});
            skLineSegment(sketch, "E1334", {"start": v(-15.28, 23.27) * mm, "end": v(-15.1, 23.35) * mm});
            skLineSegment(sketch, "E1335", {"start": v(-15.1, 23.35) * mm, "end": v(-14.39, 23.97) * mm});
            skLineSegment(sketch, "E1336", {"start": v(-14.39, 23.97) * mm, "end": v(-12.25, 26.11) * mm});
            skLineSegment(sketch, "E1337", {"start": v(-12.25, 26.11) * mm, "end": v(-11.44, 26.79) * mm});
            skLineSegment(sketch, "E1338", {"start": v(-11.44, 26.79) * mm, "end": v(-10.66, 27.3) * mm});
            skLineSegment(sketch, "E1339", {"start": v(17.78, 14.82) * mm, "end": v(19.22, 15.35) * mm});
            skLineSegment(sketch, "E1340", {"start": v(19.22, 15.35) * mm, "end": v(20.33, 15.91) * mm});
            skLineSegment(sketch, "E1341", {"start": v(20.33, 15.91) * mm, "end": v(21.75, 16.58) * mm});
            skLineSegment(sketch, "E1342", {"start": v(21.75, 16.58) * mm, "end": v(22.14, 16.63) * mm});
            skLineSegment(sketch, "E1343", {"start": v(22.14, 16.63) * mm, "end": v(22.41, 16.56) * mm});
            skLineSegment(sketch, "E1344", {"start": v(22.41, 16.56) * mm, "end": v(22.53, 16.47) * mm});
            skLineSegment(sketch, "E1345", {"start": v(22.53, 16.47) * mm, "end": v(22.55, 16.33) * mm});
            skLineSegment(sketch, "E1346", {"start": v(22.55, 16.33) * mm, "end": v(22.34, 16.05) * mm});
            skLineSegment(sketch, "E1347", {"start": v(22.34, 16.05) * mm, "end": v(21.51, 15.66) * mm});
            skLineSegment(sketch, "E1348", {"start": v(21.51, 15.66) * mm, "end": v(20.17, 15.1) * mm});
            skLineSegment(sketch, "E1349", {"start": v(20.17, 15.1) * mm, "end": v(19.15, 14.9) * mm});
            skLineSegment(sketch, "E1350", {"start": v(19.15, 14.9) * mm, "end": v(18, 14.76) * mm});
            skLineSegment(sketch, "E1351", {"start": v(18, 14.76) * mm, "end": v(17.84, 14.8) * mm});
            skLineSegment(sketch, "E1352", {"start": v(17.84, 14.8) * mm, "end": v(17.78, 14.82) * mm});
            skLineSegment(sketch, "E1353", {"start": v(25.3, 25.5) * mm, "end": v(25.66, 25.2) * mm});
            skLineSegment(sketch, "E1354", {"start": v(25.66, 25.2) * mm, "end": v(25.95, 24.82) * mm});
            skLineSegment(sketch, "E1355", {"start": v(25.95, 24.82) * mm, "end": v(26.06, 24.5) * mm});
            skLineSegment(sketch, "E1356", {"start": v(26.06, 24.5) * mm, "end": v(26.04, 24.25) * mm});
            skLineSegment(sketch, "E1357", {"start": v(26.04, 24.25) * mm, "end": v(25.92, 23.98) * mm});
            skLineSegment(sketch, "E1358", {"start": v(25.92, 23.98) * mm, "end": v(25.77, 23.78) * mm});
            skLineSegment(sketch, "E1359", {"start": v(25.77, 23.78) * mm, "end": v(25.57, 23.66) * mm});
            skLineSegment(sketch, "E1360", {"start": v(25.57, 23.66) * mm, "end": v(25.43, 23.67) * mm});
            skLineSegment(sketch, "E1361", {"start": v(25.43, 23.67) * mm, "end": v(25.26, 23.8) * mm});
            skLineSegment(sketch, "E1362", {"start": v(25.26, 23.8) * mm, "end": v(25, 24.2) * mm});
            skLineSegment(sketch, "E1363", {"start": v(25, 24.2) * mm, "end": v(24.53, 25.21) * mm});
            skLineSegment(sketch, "E1364", {"start": v(24.53, 25.21) * mm, "end": v(24.19, 25.74) * mm});
            skLineSegment(sketch, "E1365", {"start": v(24.19, 25.74) * mm, "end": v(24.12, 25.92) * mm});
            skLineSegment(sketch, "E1366", {"start": v(24.12, 25.92) * mm, "end": v(24.15, 26.03) * mm});
            skLineSegment(sketch, "E1367", {"start": v(24.15, 26.03) * mm, "end": v(24.32, 26.02) * mm});
            skLineSegment(sketch, "E1368", {"start": v(24.32, 26.02) * mm, "end": v(24.87, 25.78) * mm});
            skLineSegment(sketch, "E1369", {"start": v(24.87, 25.78) * mm, "end": v(25.3, 25.5) * mm});
            skLineSegment(sketch, "E1370", {"start": v(25.58, 22.58) * mm, "end": v(26.34, 22.3) * mm});
            skLineSegment(sketch, "E1371", {"start": v(26.34, 22.3) * mm, "end": v(27.34, 21.7) * mm});
            skLineSegment(sketch, "E1372", {"start": v(27.34, 21.7) * mm, "end": v(28.71, 20.65) * mm});
            skLineSegment(sketch, "E1373", {"start": v(28.71, 20.65) * mm, "end": v(29.35, 20.03) * mm});
            skLineSegment(sketch, "E1374", {"start": v(29.35, 20.03) * mm, "end": v(29.48, 19.8) * mm});
            skLineSegment(sketch, "E1375", {"start": v(29.48, 19.8) * mm, "end": v(29.5, 19.7) * mm});
            skLineSegment(sketch, "E1376", {"start": v(29.5, 19.7) * mm, "end": v(29.45, 19.64) * mm});
            skLineSegment(sketch, "E1377", {"start": v(29.45, 19.64) * mm, "end": v(29.32, 19.62) * mm});
            skLineSegment(sketch, "E1378", {"start": v(29.32, 19.62) * mm, "end": v(29.04, 19.72) * mm});
            skLineSegment(sketch, "E1379", {"start": v(29.04, 19.72) * mm, "end": v(28.58, 19.95) * mm});
            skLineSegment(sketch, "E1380", {"start": v(28.58, 19.95) * mm, "end": v(27.72, 20.4) * mm});
            skLineSegment(sketch, "E1381", {"start": v(27.72, 20.4) * mm, "end": v(27.21, 20.6) * mm});
            skLineSegment(sketch, "E1382", {"start": v(27.21, 20.6) * mm, "end": v(26.72, 20.68) * mm});
            skLineSegment(sketch, "E1383", {"start": v(26.72, 20.68) * mm, "end": v(26.26, 20.6) * mm});
            skLineSegment(sketch, "E1384", {"start": v(26.26, 20.6) * mm, "end": v(26, 20.5) * mm});
            skLineSegment(sketch, "E1385", {"start": v(26, 20.5) * mm, "end": v(25.75, 20.27) * mm});
            skLineSegment(sketch, "E1386", {"start": v(25.75, 20.27) * mm, "end": v(25.64, 20) * mm});
            skLineSegment(sketch, "E1387", {"start": v(25.64, 20) * mm, "end": v(25.68, 19.72) * mm});
            skLineSegment(sketch, "E1388", {"start": v(25.68, 19.72) * mm, "end": v(25.9, 19.42) * mm});
            skLineSegment(sketch, "E1389", {"start": v(25.9, 19.42) * mm, "end": v(26.27, 19.17) * mm});
            skLineSegment(sketch, "E1390", {"start": v(26.27, 19.17) * mm, "end": v(26.6, 19.03) * mm});
            skLineSegment(sketch, "E1391", {"start": v(26.6, 19.03) * mm, "end": v(27.2, 18.84) * mm});
            skLineSegment(sketch, "E1392", {"start": v(27.2, 18.84) * mm, "end": v(28.04, 18.64) * mm});
            skLineSegment(sketch, "E1393", {"start": v(28.04, 18.64) * mm, "end": v(28.92, 18.43) * mm});
            skLineSegment(sketch, "E1394", {"start": v(28.92, 18.43) * mm, "end": v(29.17, 18.3) * mm});
            skLineSegment(sketch, "E1395", {"start": v(29.17, 18.3) * mm, "end": v(29.27, 18.17) * mm});
            skLineSegment(sketch, "E1396", {"start": v(29.27, 18.17) * mm, "end": v(29.28, 18.04) * mm});
            skLineSegment(sketch, "E1397", {"start": v(29.28, 18.04) * mm, "end": v(29.2, 17.86) * mm});
            skLineSegment(sketch, "E1398", {"start": v(29.2, 17.86) * mm, "end": v(28.98, 17.6) * mm});
            skLineSegment(sketch, "E1399", {"start": v(28.98, 17.6) * mm, "end": v(28.56, 17.31) * mm});
            skLineSegment(sketch, "E1400", {"start": v(28.56, 17.31) * mm, "end": v(28.2, 17.19) * mm});
            skLineSegment(sketch, "E1401", {"start": v(28.2, 17.19) * mm, "end": v(27.84, 17.17) * mm});
            skLineSegment(sketch, "E1402", {"start": v(27.84, 17.17) * mm, "end": v(27.59, 17.23) * mm});
            skLineSegment(sketch, "E1403", {"start": v(27.59, 17.23) * mm, "end": v(27.32, 17.42) * mm});
            skLineSegment(sketch, "E1404", {"start": v(27.32, 17.42) * mm, "end": v(27.03, 17.63) * mm});
            skLineSegment(sketch, "E1405", {"start": v(27.03, 17.63) * mm, "end": v(26.74, 17.7) * mm});
            skLineSegment(sketch, "E1406", {"start": v(26.74, 17.7) * mm, "end": v(26.3, 17.64) * mm});
            skLineSegment(sketch, "E1407", {"start": v(26.3, 17.64) * mm, "end": v(25.25, 17.42) * mm});
            skLineSegment(sketch, "E1408", {"start": v(25.25, 17.42) * mm, "end": v(24.78, 17.37) * mm});
            skLineSegment(sketch, "E1409", {"start": v(24.78, 17.37) * mm, "end": v(24.24, 17.43) * mm});
            skLineSegment(sketch, "E1410", {"start": v(24.24, 17.43) * mm, "end": v(23.82, 17.58) * mm});
            skLineSegment(sketch, "E1411", {"start": v(23.82, 17.58) * mm, "end": v(23.52, 17.77) * mm});
            skLineSegment(sketch, "E1412", {"start": v(23.52, 17.77) * mm, "end": v(23.14, 18.16) * mm});
            skLineSegment(sketch, "E1413", {"start": v(23.14, 18.16) * mm, "end": v(22.86, 18.5) * mm});
            skLineSegment(sketch, "E1414", {"start": v(22.86, 18.5) * mm, "end": v(22.65, 18.71) * mm});
            skLineSegment(sketch, "E1415", {"start": v(22.65, 18.71) * mm, "end": v(22.22, 18.99) * mm});
            skLineSegment(sketch, "E1416", {"start": v(22.22, 18.99) * mm, "end": v(21.2, 19.4) * mm});
            skLineSegment(sketch, "E1417", {"start": v(21.2, 19.4) * mm, "end": v(20.8, 19.6) * mm});
            skLineSegment(sketch, "E1418", {"start": v(20.8, 19.6) * mm, "end": v(20.56, 19.82) * mm});
            skLineSegment(sketch, "E1419", {"start": v(20.56, 19.82) * mm, "end": v(20.5, 20) * mm});
            skLineSegment(sketch, "E1420", {"start": v(20.5, 20) * mm, "end": v(20.53, 20.13) * mm});
            skLineSegment(sketch, "E1421", {"start": v(20.53, 20.13) * mm, "end": v(20.63, 20.26) * mm});
            skLineSegment(sketch, "E1422", {"start": v(20.63, 20.26) * mm, "end": v(20.79, 20.38) * mm});
            skLineSegment(sketch, "E1423", {"start": v(20.79, 20.38) * mm, "end": v(21.12, 20.54) * mm});
            skLineSegment(sketch, "E1424", {"start": v(21.12, 20.54) * mm, "end": v(21.68, 20.69) * mm});
            skLineSegment(sketch, "E1425", {"start": v(21.68, 20.69) * mm, "end": v(22.14, 20.74) * mm});
            skLineSegment(sketch, "E1426", {"start": v(22.14, 20.74) * mm, "end": v(22.61, 20.74) * mm});
            skLineSegment(sketch, "E1427", {"start": v(22.61, 20.74) * mm, "end": v(23.12, 20.7) * mm});
            skLineSegment(sketch, "E1428", {"start": v(23.12, 20.7) * mm, "end": v(23.42, 20.73) * mm});
            skLineSegment(sketch, "E1429", {"start": v(23.42, 20.73) * mm, "end": v(23.6, 20.8) * mm});
            skLineSegment(sketch, "E1430", {"start": v(23.6, 20.8) * mm, "end": v(23.78, 20.99) * mm});
            skLineSegment(sketch, "E1431", {"start": v(23.78, 20.99) * mm, "end": v(23.84, 21.26) * mm});
            skLineSegment(sketch, "E1432", {"start": v(23.84, 21.26) * mm, "end": v(23.82, 21.53) * mm});
            skLineSegment(sketch, "E1433", {"start": v(23.82, 21.53) * mm, "end": v(23.72, 21.84) * mm});
            skLineSegment(sketch, "E1434", {"start": v(23.72, 21.84) * mm, "end": v(23.47, 22.4) * mm});
            skLineSegment(sketch, "E1435", {"start": v(23.47, 22.4) * mm, "end": v(23.23, 22.91) * mm});
            skLineSegment(sketch, "E1436", {"start": v(23.23, 22.91) * mm, "end": v(23.01, 23.52) * mm});
            skLineSegment(sketch, "E1437", {"start": v(23.01, 23.52) * mm, "end": v(22.73, 24.04) * mm});
            skLineSegment(sketch, "E1438", {"start": v(22.73, 24.04) * mm, "end": v(22.62, 24.38) * mm});
            skLineSegment(sketch, "E1439", {"start": v(22.62, 24.38) * mm, "end": v(22.63, 24.54) * mm});
            skLineSegment(sketch, "E1440", {"start": v(22.63, 24.54) * mm, "end": v(22.74, 24.75) * mm});
            skLineSegment(sketch, "E1441", {"start": v(22.74, 24.75) * mm, "end": v(22.83, 24.8) * mm});
            skLineSegment(sketch, "E1442", {"start": v(22.83, 24.8) * mm, "end": v(23.02, 24.8) * mm});
            skLineSegment(sketch, "E1443", {"start": v(23.02, 24.8) * mm, "end": v(23.3, 24.67) * mm});
            skLineSegment(sketch, "E1444", {"start": v(23.3, 24.67) * mm, "end": v(23.46, 24.52) * mm});
            skLineSegment(sketch, "E1445", {"start": v(23.46, 24.52) * mm, "end": v(23.6, 24.35) * mm});
            skLineSegment(sketch, "E1446", {"start": v(23.6, 24.35) * mm, "end": v(23.78, 23.96) * mm});
            skLineSegment(sketch, "E1447", {"start": v(23.78, 23.96) * mm, "end": v(24.02, 23.4) * mm});
            skLineSegment(sketch, "E1448", {"start": v(24.02, 23.4) * mm, "end": v(24.34, 22.98) * mm});
            skLineSegment(sketch, "E1449", {"start": v(24.34, 22.98) * mm, "end": v(24.65, 22.77) * mm});
            skLineSegment(sketch, "E1450", {"start": v(24.65, 22.77) * mm, "end": v(25.02, 22.68) * mm});
            skLineSegment(sketch, "E1451", {"start": v(25.02, 22.68) * mm, "end": v(25.58, 22.58) * mm});
            skLineSegment(sketch, "E1452", {"start": v(19.33, 24.84) * mm, "end": v(20.24, 24.64) * mm});
            skLineSegment(sketch, "E1453", {"start": v(20.24, 24.64) * mm, "end": v(20.92, 24.34) * mm});
            skLineSegment(sketch, "E1454", {"start": v(20.92, 24.34) * mm, "end": v(21.51, 23.89) * mm});
            skLineSegment(sketch, "E1455", {"start": v(21.51, 23.89) * mm, "end": v(21.9, 23.43) * mm});
            skLineSegment(sketch, "E1456", {"start": v(21.9, 23.43) * mm, "end": v(22.03, 23.1) * mm});
            skLineSegment(sketch, "E1457", {"start": v(22.03, 23.1) * mm, "end": v(22, 22.9) * mm});
            skLineSegment(sketch, "E1458", {"start": v(22, 22.9) * mm, "end": v(21.89, 22.74) * mm});
            skLineSegment(sketch, "E1459", {"start": v(21.89, 22.74) * mm, "end": v(21.72, 22.69) * mm});
            skLineSegment(sketch, "E1460", {"start": v(21.72, 22.69) * mm, "end": v(21.48, 22.72) * mm});
            skLineSegment(sketch, "E1461", {"start": v(21.48, 22.72) * mm, "end": v(21.13, 22.9) * mm});
            skLineSegment(sketch, "E1462", {"start": v(21.13, 22.9) * mm, "end": v(20.75, 23.24) * mm});
            skLineSegment(sketch, "E1463", {"start": v(20.75, 23.24) * mm, "end": v(20.19, 23.77) * mm});
            skLineSegment(sketch, "E1464", {"start": v(20.19, 23.77) * mm, "end": v(19.58, 24.14) * mm});
            skLineSegment(sketch, "E1465", {"start": v(19.58, 24.14) * mm, "end": v(19.1, 24.33) * mm});
            skLineSegment(sketch, "E1466", {"start": v(19.1, 24.33) * mm, "end": v(18.65, 24.49) * mm});
            skLineSegment(sketch, "E1467", {"start": v(18.65, 24.49) * mm, "end": v(18.48, 24.62) * mm});
            skLineSegment(sketch, "E1468", {"start": v(18.48, 24.62) * mm, "end": v(18.45, 24.7) * mm});
            skLineSegment(sketch, "E1469", {"start": v(18.45, 24.7) * mm, "end": v(18.45, 24.76) * mm});
            skLineSegment(sketch, "E1470", {"start": v(18.45, 24.76) * mm, "end": v(18.51, 24.83) * mm});
            skLineSegment(sketch, "E1471", {"start": v(18.51, 24.83) * mm, "end": v(18.65, 24.88) * mm});
            skLineSegment(sketch, "E1472", {"start": v(18.65, 24.88) * mm, "end": v(19.05, 24.88) * mm});
            skLineSegment(sketch, "E1473", {"start": v(19.05, 24.88) * mm, "end": v(19.33, 24.84) * mm});
            skLineSegment(sketch, "E1474", {"start": v(12.7, 23.12) * mm, "end": v(13.57, 22.8) * mm});
            skLineSegment(sketch, "E1475", {"start": v(13.57, 22.8) * mm, "end": v(14.82, 22.53) * mm});
            skLineSegment(sketch, "E1476", {"start": v(14.82, 22.53) * mm, "end": v(15.25, 22.42) * mm});
            skLineSegment(sketch, "E1477", {"start": v(15.25, 22.42) * mm, "end": v(15.67, 22.17) * mm});
            skLineSegment(sketch, "E1478", {"start": v(15.67, 22.17) * mm, "end": v(16.82, 20.94) * mm});
            skLineSegment(sketch, "E1479", {"start": v(16.82, 20.94) * mm, "end": v(16.92, 20.76) * mm});
            skLineSegment(sketch, "E1480", {"start": v(16.92, 20.76) * mm, "end": v(16.92, 20.72) * mm});
            skLineSegment(sketch, "E1481", {"start": v(16.92, 20.72) * mm, "end": v(16.88, 20.67) * mm});
            skLineSegment(sketch, "E1482", {"start": v(16.88, 20.67) * mm, "end": v(16.66, 20.63) * mm});
            skLineSegment(sketch, "E1483", {"start": v(16.66, 20.63) * mm, "end": v(16.51, 20.64) * mm});
            skLineSegment(sketch, "E1484", {"start": v(16.51, 20.64) * mm, "end": v(15.73, 20.79) * mm});
            skLineSegment(sketch, "E1485", {"start": v(15.73, 20.79) * mm, "end": v(14.6, 21.07) * mm});
            skLineSegment(sketch, "E1486", {"start": v(14.6, 21.07) * mm, "end": v(13.26, 21.6) * mm});
            skLineSegment(sketch, "E1487", {"start": v(13.26, 21.6) * mm, "end": v(12.25, 22.22) * mm});
            skLineSegment(sketch, "E1488", {"start": v(12.25, 22.22) * mm, "end": v(11.12, 23.22) * mm});
            skLineSegment(sketch, "E1489", {"start": v(11.12, 23.22) * mm, "end": v(10.67, 23.75) * mm});
            skLineSegment(sketch, "E1490", {"start": v(10.67, 23.75) * mm, "end": v(10.51, 24.07) * mm});
            skLineSegment(sketch, "E1491", {"start": v(10.51, 24.07) * mm, "end": v(10.53, 24.22) * mm});
            skLineSegment(sketch, "E1492", {"start": v(10.53, 24.22) * mm, "end": v(10.63, 24.3) * mm});
            skLineSegment(sketch, "E1493", {"start": v(10.63, 24.3) * mm, "end": v(10.81, 24.28) * mm});
            skLineSegment(sketch, "E1494", {"start": v(10.81, 24.28) * mm, "end": v(11.2, 24.07) * mm});
            skLineSegment(sketch, "E1495", {"start": v(11.2, 24.07) * mm, "end": v(11.8, 23.66) * mm});
            skLineSegment(sketch, "E1496", {"start": v(11.8, 23.66) * mm, "end": v(12.7, 23.12) * mm});
            skLineSegment(sketch, "E1497", {"start": v(11, 17.87) * mm, "end": v(10.44, 20.03) * mm});
            skLineSegment(sketch, "E1498", {"start": v(10.44, 20.03) * mm, "end": v(9.92, 21.76) * mm});
            skLineSegment(sketch, "E1499", {"start": v(9.92, 21.76) * mm, "end": v(9.86, 22.24) * mm});
            skLineSegment(sketch, "E1500", {"start": v(9.86, 22.24) * mm, "end": v(9.92, 22.56) * mm});
            skLineSegment(sketch, "E1501", {"start": v(9.92, 22.56) * mm, "end": v(10.06, 22.72) * mm});
            skLineSegment(sketch, "E1502", {"start": v(10.06, 22.72) * mm, "end": v(10.24, 22.74) * mm});
            skLineSegment(sketch, "E1503", {"start": v(10.24, 22.74) * mm, "end": v(10.47, 22.65) * mm});
            skLineSegment(sketch, "E1504", {"start": v(10.47, 22.65) * mm, "end": v(10.75, 22.41) * mm});
            skLineSegment(sketch, "E1505", {"start": v(10.75, 22.41) * mm, "end": v(11.47, 21.56) * mm});
            skLineSegment(sketch, "E1506", {"start": v(11.47, 21.56) * mm, "end": v(11.91, 21.08) * mm});
            skLineSegment(sketch, "E1507", {"start": v(11.91, 21.08) * mm, "end": v(12.27, 20.76) * mm});
            skLineSegment(sketch, "E1508", {"start": v(12.27, 20.76) * mm, "end": v(12.79, 20.42) * mm});
            skLineSegment(sketch, "E1509", {"start": v(12.79, 20.42) * mm, "end": v(13.97, 19.82) * mm});
            skLineSegment(sketch, "E1510", {"start": v(13.97, 19.82) * mm, "end": v(14.34, 19.52) * mm});
            skLineSegment(sketch, "E1511", {"start": v(14.34, 19.52) * mm, "end": v(14.47, 19.23) * mm});
            skLineSegment(sketch, "E1512", {"start": v(14.47, 19.23) * mm, "end": v(14.44, 18.7) * mm});
            skLineSegment(sketch, "E1513", {"start": v(14.44, 18.7) * mm, "end": v(14.04, 17.75) * mm});
            skLineSegment(sketch, "E1514", {"start": v(14.04, 17.75) * mm, "end": v(13.75, 17.12) * mm});
            skLineSegment(sketch, "E1515", {"start": v(13.75, 17.12) * mm, "end": v(13.47, 16.4) * mm});
            skLineSegment(sketch, "E1516", {"start": v(13.47, 16.4) * mm, "end": v(13.31, 15.75) * mm});
            skLineSegment(sketch, "E1517", {"start": v(13.31, 15.75) * mm, "end": v(13.24, 14.74) * mm});
            skLineSegment(sketch, "E1518", {"start": v(13.24, 14.74) * mm, "end": v(13.3, 13.5) * mm});
            skLineSegment(sketch, "E1519", {"start": v(13.3, 13.5) * mm, "end": v(13.4, 12.5) * mm});
            skLineSegment(sketch, "E1520", {"start": v(13.4, 12.5) * mm, "end": v(13.54, 11.9) * mm});
            skLineSegment(sketch, "E1521", {"start": v(13.54, 11.9) * mm, "end": v(13.85, 11.29) * mm});
            skLineSegment(sketch, "E1522", {"start": v(13.85, 11.29) * mm, "end": v(14.3, 10.67) * mm});
            skLineSegment(sketch, "E1523", {"start": v(14.3, 10.67) * mm, "end": v(14.64, 10.1) * mm});
            skLineSegment(sketch, "E1524", {"start": v(14.64, 10.1) * mm, "end": v(14.67, 9.88) * mm});
            skLineSegment(sketch, "E1525", {"start": v(14.67, 9.88) * mm, "end": v(14.54, 9.76) * mm});
            skLineSegment(sketch, "E1526", {"start": v(14.54, 9.76) * mm, "end": v(14.31, 9.75) * mm});
            skLineSegment(sketch, "E1527", {"start": v(14.31, 9.75) * mm, "end": v(13.88, 9.85) * mm});
            skLineSegment(sketch, "E1528", {"start": v(13.88, 9.85) * mm, "end": v(13.25, 10.15) * mm});
            skLineSegment(sketch, "E1529", {"start": v(13.25, 10.15) * mm, "end": v(12.67, 10.65) * mm});
            skLineSegment(sketch, "E1530", {"start": v(12.67, 10.65) * mm, "end": v(12.4, 11.03) * mm});
            skLineSegment(sketch, "E1531", {"start": v(12.4, 11.03) * mm, "end": v(12.1, 11.62) * mm});
            skLineSegment(sketch, "E1532", {"start": v(12.1, 11.62) * mm, "end": v(11.86, 12.47) * mm});
            skLineSegment(sketch, "E1533", {"start": v(11.86, 12.47) * mm, "end": v(11.6, 14.04) * mm});
            skLineSegment(sketch, "E1534", {"start": v(11.6, 14.04) * mm, "end": v(11.44, 15.33) * mm});
            skLineSegment(sketch, "E1535", {"start": v(11.44, 15.33) * mm, "end": v(11.2, 16.94) * mm});
            skLineSegment(sketch, "E1536", {"start": v(11.2, 16.94) * mm, "end": v(11, 17.87) * mm});
            skLineSegment(sketch, "E1537", {"start": v(15.04, -22.32) * mm, "end": v(16.05, -21.26) * mm});
            skLineSegment(sketch, "E1538", {"start": v(16.05, -21.26) * mm, "end": v(16.93, -20.36) * mm});
            skLineSegment(sketch, "E1539", {"start": v(16.93, -20.36) * mm, "end": v(17.52, -20.16) * mm});
            skLineSegment(sketch, "E1540", {"start": v(17.52, -20.16) * mm, "end": v(18.05, -20.29) * mm});
            skLineSegment(sketch, "E1541", {"start": v(18.05, -20.29) * mm, "end": v(18.47, -20.63) * mm});
            skLineSegment(sketch, "E1542", {"start": v(18.47, -20.63) * mm, "end": v(18.75, -21.25) * mm});
            skLineSegment(sketch, "E1543", {"start": v(18.75, -21.25) * mm, "end": v(18.71, -21.67) * mm});
            skLineSegment(sketch, "E1544", {"start": v(18.71, -21.67) * mm, "end": v(18.32, -22.27) * mm});
            skLineSegment(sketch, "E1545", {"start": v(18.32, -22.27) * mm, "end": v(16.9, -23.67) * mm});
            skLineSegment(sketch, "E1546", {"start": v(16.9, -23.67) * mm, "end": v(14.42, -25.61) * mm});
            skLineSegment(sketch, "E1547", {"start": v(14.42, -25.61) * mm, "end": v(13.7, -25.96) * mm});
            skLineSegment(sketch, "E1548", {"start": v(13.7, -25.96) * mm, "end": v(13.26, -26.04) * mm});
            skLineSegment(sketch, "E1549", {"start": v(13.26, -26.04) * mm, "end": v(12.69, -26) * mm});
            skLineSegment(sketch, "E1550", {"start": v(12.69, -26) * mm, "end": v(12.15, -25.79) * mm});
            skLineSegment(sketch, "E1551", {"start": v(12.15, -25.79) * mm, "end": v(11.87, -25.52) * mm});
            skLineSegment(sketch, "E1552", {"start": v(11.87, -25.52) * mm, "end": v(11.78, -25.17) * mm});
            skLineSegment(sketch, "E1553", {"start": v(11.78, -25.17) * mm, "end": v(11.9, -24.78) * mm});
            skLineSegment(sketch, "E1554", {"start": v(11.9, -24.78) * mm, "end": v(12.2, -24.42) * mm});
            skLineSegment(sketch, "E1555", {"start": v(12.2, -24.42) * mm, "end": v(12.93, -23.87) * mm});
            skLineSegment(sketch, "E1556", {"start": v(12.93, -23.87) * mm, "end": v(14.3, -22.93) * mm});
            skLineSegment(sketch, "E1557", {"start": v(14.3, -22.93) * mm, "end": v(15.04, -22.32) * mm});
            skLineSegment(sketch, "E1558", {"start": v(17.97, -24.55) * mm, "end": v(18.91, -23.56) * mm});
            skLineSegment(sketch, "E1559", {"start": v(18.91, -23.56) * mm, "end": v(19.32, -23.19) * mm});
            skLineSegment(sketch, "E1560", {"start": v(19.32, -23.19) * mm, "end": v(19.64, -23) * mm});
            skLineSegment(sketch, "E1561", {"start": v(19.64, -23) * mm, "end": v(20.02, -22.95) * mm});
            skLineSegment(sketch, "E1562", {"start": v(20.02, -22.95) * mm, "end": v(20.42, -23.06) * mm});
            skLineSegment(sketch, "E1563", {"start": v(20.42, -23.06) * mm, "end": v(20.76, -23.35) * mm});
            skLineSegment(sketch, "E1564", {"start": v(20.76, -23.35) * mm, "end": v(20.88, -23.64) * mm});
            skLineSegment(sketch, "E1565", {"start": v(20.88, -23.64) * mm, "end": v(20.85, -24.02) * mm});
            skLineSegment(sketch, "E1566", {"start": v(20.85, -24.02) * mm, "end": v(20.53, -24.69) * mm});
            skLineSegment(sketch, "E1567", {"start": v(20.53, -24.69) * mm, "end": v(20.04, -25.32) * mm});
            skLineSegment(sketch, "E1568", {"start": v(20.04, -25.32) * mm, "end": v(19.22, -26.1) * mm});
            skLineSegment(sketch, "E1569", {"start": v(19.22, -26.1) * mm, "end": v(18.45, -26.62) * mm});
            skLineSegment(sketch, "E1570", {"start": v(18.45, -26.62) * mm, "end": v(17.82, -26.9) * mm});
            skLineSegment(sketch, "E1571", {"start": v(17.82, -26.9) * mm, "end": v(17.09, -27.02) * mm});
            skLineSegment(sketch, "E1572", {"start": v(17.09, -27.02) * mm, "end": v(16.64, -26.97) * mm});
            skLineSegment(sketch, "E1573", {"start": v(16.64, -26.97) * mm, "end": v(16.25, -26.8) * mm});
            skLineSegment(sketch, "E1574", {"start": v(16.25, -26.8) * mm, "end": v(16.1, -26.6) * mm});
            skLineSegment(sketch, "E1575", {"start": v(16.1, -26.6) * mm, "end": v(16.06, -26.37) * mm});
            skLineSegment(sketch, "E1576", {"start": v(16.06, -26.37) * mm, "end": v(16.15, -26.14) * mm});
            skLineSegment(sketch, "E1577", {"start": v(16.15, -26.14) * mm, "end": v(16.37, -25.84) * mm});
            skLineSegment(sketch, "E1578", {"start": v(16.37, -25.84) * mm, "end": v(16.68, -25.53) * mm});
            skLineSegment(sketch, "E1579", {"start": v(16.68, -25.53) * mm, "end": v(17.33, -25.04) * mm});
            skLineSegment(sketch, "E1580", {"start": v(17.33, -25.04) * mm, "end": v(17.7, -24.78) * mm});
            skLineSegment(sketch, "E1581", {"start": v(17.7, -24.78) * mm, "end": v(17.97, -24.55) * mm});
            skLineSegment(sketch, "E1582", {"start": v(-26.62, -25.15) * mm, "end": v(-26.76, -24.73) * mm});
            skLineSegment(sketch, "E1583", {"start": v(-26.76, -24.73) * mm, "end": v(-26.87, -23.58) * mm});
            skLineSegment(sketch, "E1584", {"start": v(-26.87, -23.58) * mm, "end": v(-27, -22.97) * mm});
            skLineSegment(sketch, "E1585", {"start": v(-27, -22.97) * mm, "end": v(-27.24, -22.69) * mm});
            skLineSegment(sketch, "E1586", {"start": v(-27.24, -22.69) * mm, "end": v(-27.57, -22.7) * mm});
            skLineSegment(sketch, "E1587", {"start": v(-27.57, -22.7) * mm, "end": v(-28.05, -22.97) * mm});
            skLineSegment(sketch, "E1588", {"start": v(-28.05, -22.97) * mm, "end": v(-28.47, -23.43) * mm});
            skLineSegment(sketch, "E1589", {"start": v(-28.47, -23.43) * mm, "end": v(-28.7, -23.99) * mm});
            skLineSegment(sketch, "E1590", {"start": v(-28.7, -23.99) * mm, "end": v(-28.77, -24.51) * mm});
            skLineSegment(sketch, "E1591", {"start": v(-28.77, -24.51) * mm, "end": v(-28.68, -25.2) * mm});
            skLineSegment(sketch, "E1592", {"start": v(-28.68, -25.2) * mm, "end": v(-28.4, -25.87) * mm});
            skLineSegment(sketch, "E1593", {"start": v(-28.4, -25.87) * mm, "end": v(-27.96, -26.5) * mm});
            skLineSegment(sketch, "E1594", {"start": v(-27.96, -26.5) * mm, "end": v(-27.1, -27.24) * mm});
            skLineSegment(sketch, "E1595", {"start": v(-27.1, -27.24) * mm, "end": v(-26.38, -27.6) * mm});
            skLineSegment(sketch, "E1596", {"start": v(-26.38, -27.6) * mm, "end": v(-25.73, -27.78) * mm});
            skLineSegment(sketch, "E1597", {"start": v(-25.73, -27.78) * mm, "end": v(-25.1, -27.84) * mm});
            skLineSegment(sketch, "E1598", {"start": v(-25.1, -27.84) * mm, "end": v(-24.52, -27.73) * mm});
            skLineSegment(sketch, "E1599", {"start": v(-24.52, -27.73) * mm, "end": v(-24.26, -27.49) * mm});
            skLineSegment(sketch, "E1600", {"start": v(-24.26, -27.49) * mm, "end": v(-24.2, -27.17) * mm});
            skLineSegment(sketch, "E1601", {"start": v(-24.2, -27.17) * mm, "end": v(-24.28, -26.89) * mm});
            skLineSegment(sketch, "E1602", {"start": v(-24.28, -26.89) * mm, "end": v(-24.51, -26.57) * mm});
            skLineSegment(sketch, "E1603", {"start": v(-24.51, -26.57) * mm, "end": v(-24.86, -26.3) * mm});
            skLineSegment(sketch, "E1604", {"start": v(-24.86, -26.3) * mm, "end": v(-25.22, -26.1) * mm});
            skLineSegment(sketch, "E1605", {"start": v(-25.22, -26.1) * mm, "end": v(-26.03, -25.75) * mm});
            skLineSegment(sketch, "E1606", {"start": v(-26.03, -25.75) * mm, "end": v(-26.38, -25.49) * mm});
            skLineSegment(sketch, "E1607", {"start": v(-26.38, -25.49) * mm, "end": v(-26.62, -25.15) * mm});
            skLineSegment(sketch, "E1608", {"start": v(-22.38, -26.94) * mm, "end": v(-22.43, -26.03) * mm});
            skLineSegment(sketch, "E1609", {"start": v(-22.43, -26.03) * mm, "end": v(-22.26, -25.3) * mm});
            skLineSegment(sketch, "E1610", {"start": v(-22.26, -25.3) * mm, "end": v(-21.95, -24.86) * mm});
            skLineSegment(sketch, "E1611", {"start": v(-21.95, -24.86) * mm, "end": v(-21.2, -24.43) * mm});
            skLineSegment(sketch, "E1612", {"start": v(-21.2, -24.43) * mm, "end": v(-20.37, -24.45) * mm});
            skLineSegment(sketch, "E1613", {"start": v(-20.37, -24.45) * mm, "end": v(-19.49, -24.79) * mm});
            skLineSegment(sketch, "E1614", {"start": v(-19.49, -24.79) * mm, "end": v(-18.39, -25.45) * mm});
            skLineSegment(sketch, "E1615", {"start": v(-18.39, -25.45) * mm, "end": v(-17.67, -26.16) * mm});
            skLineSegment(sketch, "E1616", {"start": v(-17.67, -26.16) * mm, "end": v(-16.7, -27.86) * mm});
            skLineSegment(sketch, "E1617", {"start": v(-16.7, -27.86) * mm, "end": v(-16.31, -28.63) * mm});
            skLineSegment(sketch, "E1618", {"start": v(-16.31, -28.63) * mm, "end": v(-16.2, -29.17) * mm});
            skLineSegment(sketch, "E1619", {"start": v(-16.2, -29.17) * mm, "end": v(-16.4, -29.45) * mm});
            skLineSegment(sketch, "E1620", {"start": v(-16.4, -29.45) * mm, "end": v(-16.8, -29.54) * mm});
            skLineSegment(sketch, "E1621", {"start": v(-16.8, -29.54) * mm, "end": v(-17.55, -29.51) * mm});
            skLineSegment(sketch, "E1622", {"start": v(-17.55, -29.51) * mm, "end": v(-18.91, -29.28) * mm});
            skLineSegment(sketch, "E1623", {"start": v(-18.91, -29.28) * mm, "end": v(-20.83, -28.73) * mm});
            skLineSegment(sketch, "E1624", {"start": v(-20.83, -28.73) * mm, "end": v(-21.76, -28.2) * mm});
            skLineSegment(sketch, "E1625", {"start": v(-21.76, -28.2) * mm, "end": v(-22.2, -27.56) * mm});
            skLineSegment(sketch, "E1626", {"start": v(-22.2, -27.56) * mm, "end": v(-22.38, -26.94) * mm});
            skLineSegment(sketch, "E1627", {"start": v(-24.1, -20.16) * mm, "end": v(-23.47, -19.97) * mm});
            skLineSegment(sketch, "E1628", {"start": v(-23.47, -19.97) * mm, "end": v(-22.73, -19.9) * mm});
            skLineSegment(sketch, "E1629", {"start": v(-22.73, -19.9) * mm, "end": v(-22.23, -20.03) * mm});
            skLineSegment(sketch, "E1630", {"start": v(-22.23, -20.03) * mm, "end": v(-21.7, -20.3) * mm});
            skLineSegment(sketch, "E1631", {"start": v(-21.7, -20.3) * mm, "end": v(-21.19, -20.68) * mm});
            skLineSegment(sketch, "E1632", {"start": v(-21.19, -20.68) * mm, "end": v(-20.73, -21.17) * mm});
            skLineSegment(sketch, "E1633", {"start": v(-20.73, -21.17) * mm, "end": v(-20.3, -21.88) * mm});
            skLineSegment(sketch, "E1634", {"start": v(-20.3, -21.88) * mm, "end": v(-20.1, -22.45) * mm});
            skLineSegment(sketch, "E1635", {"start": v(-20.1, -22.45) * mm, "end": v(-20.07, -22.83) * mm});
            skLineSegment(sketch, "E1636", {"start": v(-20.07, -22.83) * mm, "end": v(-20.12, -23.05) * mm});
            skLineSegment(sketch, "E1637", {"start": v(-20.12, -23.05) * mm, "end": v(-20.31, -23.27) * mm});
            skLineSegment(sketch, "E1638", {"start": v(-20.31, -23.27) * mm, "end": v(-20.63, -23.39) * mm});
            skLineSegment(sketch, "E1639", {"start": v(-20.63, -23.39) * mm, "end": v(-21.06, -23.4) * mm});
            skLineSegment(sketch, "E1640", {"start": v(-21.06, -23.4) * mm, "end": v(-22.05, -23.38) * mm});
            skLineSegment(sketch, "E1641", {"start": v(-22.05, -23.38) * mm, "end": v(-22.53, -23.42) * mm});
            skLineSegment(sketch, "E1642", {"start": v(-22.53, -23.42) * mm, "end": v(-22.86, -23.55) * mm});
            skLineSegment(sketch, "E1643", {"start": v(-22.86, -23.55) * mm, "end": v(-23.14, -23.74) * mm});
            skLineSegment(sketch, "E1644", {"start": v(-23.14, -23.74) * mm, "end": v(-23.43, -24.01) * mm});
            skLineSegment(sketch, "E1645", {"start": v(-23.43, -24.01) * mm, "end": v(-23.8, -24.45) * mm});
            skLineSegment(sketch, "E1646", {"start": v(-23.8, -24.45) * mm, "end": v(-24, -24.63) * mm});
            skLineSegment(sketch, "E1647", {"start": v(-24, -24.63) * mm, "end": v(-24.12, -24.68) * mm});
            skLineSegment(sketch, "E1648", {"start": v(-24.12, -24.68) * mm, "end": v(-24.26, -24.66) * mm});
            skLineSegment(sketch, "E1649", {"start": v(-24.26, -24.66) * mm, "end": v(-24.46, -24.53) * mm});
            skLineSegment(sketch, "E1650", {"start": v(-24.46, -24.53) * mm, "end": v(-24.7, -24.24) * mm});
            skLineSegment(sketch, "E1651", {"start": v(-24.7, -24.24) * mm, "end": v(-24.82, -24.06) * mm});
            skLineSegment(sketch, "E1652", {"start": v(-24.82, -24.06) * mm, "end": v(-25.01, -23.67) * mm});
            skLineSegment(sketch, "E1653", {"start": v(-25.01, -23.67) * mm, "end": v(-25.12, -23.38) * mm});
            skLineSegment(sketch, "E1654", {"start": v(-25.12, -23.38) * mm, "end": v(-25.28, -22.84) * mm});
            skLineSegment(sketch, "E1655", {"start": v(-25.28, -22.84) * mm, "end": v(-25.47, -22.35) * mm});
            skLineSegment(sketch, "E1656", {"start": v(-25.47, -22.35) * mm, "end": v(-25.8, -21.85) * mm});
            skLineSegment(sketch, "E1657", {"start": v(-25.8, -21.85) * mm, "end": v(-26.01, -21.53) * mm});
            skLineSegment(sketch, "E1658", {"start": v(-26.01, -21.53) * mm, "end": v(-26.08, -21.27) * mm});
            skLineSegment(sketch, "E1659", {"start": v(-26.08, -21.27) * mm, "end": v(-26.02, -21.02) * mm});
            skLineSegment(sketch, "E1660", {"start": v(-26.02, -21.02) * mm, "end": v(-25.84, -20.79) * mm});
            skLineSegment(sketch, "E1661", {"start": v(-25.84, -20.79) * mm, "end": v(-25.52, -20.54) * mm});
            skLineSegment(sketch, "E1662", {"start": v(-25.52, -20.54) * mm, "end": v(-25.1, -20.36) * mm});
            skLineSegment(sketch, "E1663", {"start": v(-25.1, -20.36) * mm, "end": v(-24.34, -20.22) * mm});
            skLineSegment(sketch, "E1664", {"start": v(-24.34, -20.22) * mm, "end": v(-24.1, -20.16) * mm});
            skLineSegment(sketch, "E1665", {"start": v(-22.22, -18.48) * mm, "end": v(-21.42, -18.5) * mm});
            skLineSegment(sketch, "E1666", {"start": v(-21.42, -18.5) * mm, "end": v(-20.93, -18.4) * mm});
            skLineSegment(sketch, "E1667", {"start": v(-20.93, -18.4) * mm, "end": v(-20.65, -18.2) * mm});
            skLineSegment(sketch, "E1668", {"start": v(-20.65, -18.2) * mm, "end": v(-20.5, -17.85) * mm});
            skLineSegment(sketch, "E1669", {"start": v(-20.5, -17.85) * mm, "end": v(-20.53, -17.35) * mm});
            skLineSegment(sketch, "E1670", {"start": v(-20.53, -17.35) * mm, "end": v(-20.68, -16.36) * mm});
            skLineSegment(sketch, "E1671", {"start": v(-20.68, -16.36) * mm, "end": v(-20.83, -15) * mm});
            skLineSegment(sketch, "E1672", {"start": v(-20.83, -15) * mm, "end": v(-20.86, -14.35) * mm});
            skLineSegment(sketch, "E1673", {"start": v(-20.86, -14.35) * mm, "end": v(-20.91, -13.97) * mm});
            skLineSegment(sketch, "E1674", {"start": v(-20.91, -13.97) * mm, "end": v(-21.04, -13.6) * mm});
            skLineSegment(sketch, "E1675", {"start": v(-21.04, -13.6) * mm, "end": v(-21.19, -13.4) * mm});
            skLineSegment(sketch, "E1676", {"start": v(-21.19, -13.4) * mm, "end": v(-21.43, -13.24) * mm});
            skLineSegment(sketch, "E1677", {"start": v(-21.43, -13.24) * mm, "end": v(-21.82, -13.18) * mm});
            skLineSegment(sketch, "E1678", {"start": v(-21.82, -13.18) * mm, "end": v(-22.36, -13.3) * mm});
            skLineSegment(sketch, "E1679", {"start": v(-22.36, -13.3) * mm, "end": v(-22.96, -13.63) * mm});
            skLineSegment(sketch, "E1680", {"start": v(-22.96, -13.63) * mm, "end": v(-23.39, -14.08) * mm});
            skLineSegment(sketch, "E1681", {"start": v(-23.39, -14.08) * mm, "end": v(-23.63, -14.46) * mm});
            skLineSegment(sketch, "E1682", {"start": v(-23.63, -14.46) * mm, "end": v(-23.86, -15.03) * mm});
            skLineSegment(sketch, "E1683", {"start": v(-23.86, -15.03) * mm, "end": v(-23.95, -15.47) * mm});
            skLineSegment(sketch, "E1684", {"start": v(-23.95, -15.47) * mm, "end": v(-23.98, -15.96) * mm});
            skLineSegment(sketch, "E1685", {"start": v(-23.98, -15.96) * mm, "end": v(-23.9, -16.63) * mm});
            skLineSegment(sketch, "E1686", {"start": v(-23.9, -16.63) * mm, "end": v(-23.71, -17.4) * mm});
            skLineSegment(sketch, "E1687", {"start": v(-23.71, -17.4) * mm, "end": v(-23.49, -17.9) * mm});
            skLineSegment(sketch, "E1688", {"start": v(-23.49, -17.9) * mm, "end": v(-23.32, -18.12) * mm});
            skLineSegment(sketch, "E1689", {"start": v(-23.32, -18.12) * mm, "end": v(-23.17, -18.24) * mm});
            skLineSegment(sketch, "E1690", {"start": v(-23.17, -18.24) * mm, "end": v(-22.87, -18.36) * mm});
            skLineSegment(sketch, "E1691", {"start": v(-22.87, -18.36) * mm, "end": v(-22.22, -18.48) * mm});
            skLineSegment(sketch, "E1692", {"start": v(-17.74, -22.5) * mm, "end": v(-17.1, -23.21) * mm});
            skLineSegment(sketch, "E1693", {"start": v(-17.1, -23.21) * mm, "end": v(-16.47, -23.64) * mm});
            skLineSegment(sketch, "E1694", {"start": v(-16.47, -23.64) * mm, "end": v(-16.2, -23.75) * mm});
            skLineSegment(sketch, "E1695", {"start": v(-16.2, -23.75) * mm, "end": v(-15.9, -23.82) * mm});
            skLineSegment(sketch, "E1696", {"start": v(-15.9, -23.82) * mm, "end": v(-15.4, -23.86) * mm});
            skLineSegment(sketch, "E1697", {"start": v(-15.4, -23.86) * mm, "end": v(-14.68, -23.82) * mm});
            skLineSegment(sketch, "E1698", {"start": v(-14.68, -23.82) * mm, "end": v(-13.93, -23.73) * mm});
            skLineSegment(sketch, "E1699", {"start": v(-13.93, -23.73) * mm, "end": v(-13.5, -23.62) * mm});
            skLineSegment(sketch, "E1700", {"start": v(-13.5, -23.62) * mm, "end": v(-13.28, -23.5) * mm});
            skLineSegment(sketch, "E1701", {"start": v(-13.28, -23.5) * mm, "end": v(-13.15, -23.35) * mm});
            skLineSegment(sketch, "E1702", {"start": v(-13.15, -23.35) * mm, "end": v(-13.12, -23.24) * mm});
            skLineSegment(sketch, "E1703", {"start": v(-13.12, -23.24) * mm, "end": v(-13.16, -23.05) * mm});
            skLineSegment(sketch, "E1704", {"start": v(-13.16, -23.05) * mm, "end": v(-13.34, -22.76) * mm});
            skLineSegment(sketch, "E1705", {"start": v(-13.34, -22.76) * mm, "end": v(-13.55, -22.54) * mm});
            skLineSegment(sketch, "E1706", {"start": v(-13.55, -22.54) * mm, "end": v(-13.82, -22.31) * mm});
            skLineSegment(sketch, "E1707", {"start": v(-13.82, -22.31) * mm, "end": v(-14.36, -21.94) * mm});
            skLineSegment(sketch, "E1708", {"start": v(-14.36, -21.94) * mm, "end": v(-15.24, -21.48) * mm});
            skLineSegment(sketch, "E1709", {"start": v(-15.24, -21.48) * mm, "end": v(-16, -21.16) * mm});
            skLineSegment(sketch, "E1710", {"start": v(-16, -21.16) * mm, "end": v(-16.82, -20.9) * mm});
            skLineSegment(sketch, "E1711", {"start": v(-16.82, -20.9) * mm, "end": v(-17.41, -20.8) * mm});
            skLineSegment(sketch, "E1712", {"start": v(-17.41, -20.8) * mm, "end": v(-17.74, -20.78) * mm});
            skLineSegment(sketch, "E1713", {"start": v(-17.74, -20.78) * mm, "end": v(-17.93, -20.82) * mm});
            skLineSegment(sketch, "E1714", {"start": v(-17.93, -20.82) * mm, "end": v(-18.13, -20.92) * mm});
            skLineSegment(sketch, "E1715", {"start": v(-18.13, -20.92) * mm, "end": v(-18.22, -21.04) * mm});
            skLineSegment(sketch, "E1716", {"start": v(-18.22, -21.04) * mm, "end": v(-18.25, -21.22) * mm});
            skLineSegment(sketch, "E1717", {"start": v(-18.25, -21.22) * mm, "end": v(-18.22, -21.5) * mm});
            skLineSegment(sketch, "E1718", {"start": v(-18.22, -21.5) * mm, "end": v(-18.15, -21.76) * mm});
            skLineSegment(sketch, "E1719", {"start": v(-18.15, -21.76) * mm, "end": v(-17.92, -22.22) * mm});
            skLineSegment(sketch, "E1720", {"start": v(-17.92, -22.22) * mm, "end": v(-17.74, -22.5) * mm});
            skLineSegment(sketch, "E1721", {"start": v(-9.95, -22.16) * mm, "end": v(-9.2, -22.23) * mm});
            skLineSegment(sketch, "E1722", {"start": v(-9.2, -22.23) * mm, "end": v(-8.76, -22.28) * mm});
            skLineSegment(sketch, "E1723", {"start": v(-8.76, -22.28) * mm, "end": v(-8.35, -22.39) * mm});
            skLineSegment(sketch, "E1724", {"start": v(-8.35, -22.39) * mm, "end": v(-8.23, -22.49) * mm});
            skLineSegment(sketch, "E1725", {"start": v(-8.23, -22.49) * mm, "end": v(-8.2, -22.64) * mm});
            skLineSegment(sketch, "E1726", {"start": v(-8.2, -22.64) * mm, "end": v(-8.28, -22.82) * mm});
            skLineSegment(sketch, "E1727", {"start": v(-8.28, -22.82) * mm, "end": v(-8.46, -23) * mm});
            skLineSegment(sketch, "E1728", {"start": v(-8.46, -23) * mm, "end": v(-8.84, -23.26) * mm});
            skLineSegment(sketch, "E1729", {"start": v(-8.84, -23.26) * mm, "end": v(-9.22, -23.43) * mm});
            skLineSegment(sketch, "E1730", {"start": v(-9.22, -23.43) * mm, "end": v(-9.55, -23.5) * mm});
            skLineSegment(sketch, "E1731", {"start": v(-9.55, -23.5) * mm, "end": v(-9.9, -23.53) * mm});
            skLineSegment(sketch, "E1732", {"start": v(-9.9, -23.53) * mm, "end": v(-10.25, -23.5) * mm});
            skLineSegment(sketch, "E1733", {"start": v(-10.25, -23.5) * mm, "end": v(-10.65, -23.38) * mm});
            skLineSegment(sketch, "E1734", {"start": v(-10.65, -23.38) * mm, "end": v(-11, -23.2) * mm});
            skLineSegment(sketch, "E1735", {"start": v(-11, -23.2) * mm, "end": v(-11.29, -22.94) * mm});
            skLineSegment(sketch, "E1736", {"start": v(-11.29, -22.94) * mm, "end": v(-11.5, -22.67) * mm});
            skLineSegment(sketch, "E1737", {"start": v(-11.5, -22.67) * mm, "end": v(-11.63, -22.37) * mm});
            skLineSegment(sketch, "E1738", {"start": v(-11.63, -22.37) * mm, "end": v(-11.64, -22.2) * mm});
            skLineSegment(sketch, "E1739", {"start": v(-11.64, -22.2) * mm, "end": v(-11.57, -22.06) * mm});
            skLineSegment(sketch, "E1740", {"start": v(-11.57, -22.06) * mm, "end": v(-11.44, -21.99) * mm});
            skLineSegment(sketch, "E1741", {"start": v(-11.44, -21.99) * mm, "end": v(-11.23, -21.98) * mm});
            skLineSegment(sketch, "E1742", {"start": v(-11.23, -21.98) * mm, "end": v(-10.95, -22) * mm});
            skLineSegment(sketch, "E1743", {"start": v(-10.95, -22) * mm, "end": v(-10.5, -22.08) * mm});
            skLineSegment(sketch, "E1744", {"start": v(-10.5, -22.08) * mm, "end": v(-9.95, -22.16) * mm});
            skLineSegment(sketch, "E1745", {"start": v(-12.37, -25.3) * mm, "end": v(-11.5, -25.68) * mm});
            skLineSegment(sketch, "E1746", {"start": v(-11.5, -25.68) * mm, "end": v(-10.71, -26.23) * mm});
            skLineSegment(sketch, "E1747", {"start": v(-10.71, -26.23) * mm, "end": v(-10.16, -26.82) * mm});
            skLineSegment(sketch, "E1748", {"start": v(-10.16, -26.82) * mm, "end": v(-9.9, -27.28) * mm});
            skLineSegment(sketch, "E1749", {"start": v(-9.9, -27.28) * mm, "end": v(-9.84, -27.57) * mm});
            skLineSegment(sketch, "E1750", {"start": v(-9.84, -27.57) * mm, "end": v(-9.87, -27.85) * mm});
            skLineSegment(sketch, "E1751", {"start": v(-9.87, -27.85) * mm, "end": v(-10.06, -28.17) * mm});
            skLineSegment(sketch, "E1752", {"start": v(-10.06, -28.17) * mm, "end": v(-10.5, -28.5) * mm});
            skLineSegment(sketch, "E1753", {"start": v(-10.5, -28.5) * mm, "end": v(-11.73, -29.1) * mm});
            skLineSegment(sketch, "E1754", {"start": v(-11.73, -29.1) * mm, "end": v(-12.28, -29.26) * mm});
            skLineSegment(sketch, "E1755", {"start": v(-12.28, -29.26) * mm, "end": v(-12.71, -29.28) * mm});
            skLineSegment(sketch, "E1756", {"start": v(-12.71, -29.28) * mm, "end": v(-13.02, -29.21) * mm});
            skLineSegment(sketch, "E1757", {"start": v(-13.02, -29.21) * mm, "end": v(-13.5, -28.93) * mm});
            skLineSegment(sketch, "E1758", {"start": v(-13.5, -28.93) * mm, "end": v(-13.93, -28.5) * mm});
            skLineSegment(sketch, "E1759", {"start": v(-13.93, -28.5) * mm, "end": v(-14.7, -27.48) * mm});
            skLineSegment(sketch, "E1760", {"start": v(-14.7, -27.48) * mm, "end": v(-15.1, -26.77) * mm});
            skLineSegment(sketch, "E1761", {"start": v(-15.1, -26.77) * mm, "end": v(-15.3, -26.2) * mm});
            skLineSegment(sketch, "E1762", {"start": v(-15.3, -26.2) * mm, "end": v(-15.33, -25.85) * mm});
            skLineSegment(sketch, "E1763", {"start": v(-15.33, -25.85) * mm, "end": v(-15.25, -25.47) * mm});
            skLineSegment(sketch, "E1764", {"start": v(-15.25, -25.47) * mm, "end": v(-15.06, -25.24) * mm});
            skLineSegment(sketch, "E1765", {"start": v(-15.06, -25.24) * mm, "end": v(-14.85, -25.11) * mm});
            skLineSegment(sketch, "E1766", {"start": v(-14.85, -25.11) * mm, "end": v(-14.49, -25) * mm});
            skLineSegment(sketch, "E1767", {"start": v(-14.49, -25) * mm, "end": v(-14.05, -24.96) * mm});
            skLineSegment(sketch, "E1768", {"start": v(-14.05, -24.96) * mm, "end": v(-13.42, -25.01) * mm});
            skLineSegment(sketch, "E1769", {"start": v(-13.42, -25.01) * mm, "end": v(-12.9, -25.13) * mm});
            skLineSegment(sketch, "E1770", {"start": v(-12.9, -25.13) * mm, "end": v(-12.37, -25.3) * mm});
            skLineSegment(sketch, "E1771", {"start": v(-6.68, -27.17) * mm, "end": v(-7.15, -27.2) * mm});
            skLineSegment(sketch, "E1772", {"start": v(-7.15, -27.2) * mm, "end": v(-7.56, -27.11) * mm});
            skLineSegment(sketch, "E1773", {"start": v(-7.56, -27.11) * mm, "end": v(-8, -26.88) * mm});
            skLineSegment(sketch, "E1774", {"start": v(-8, -26.88) * mm, "end": v(-8.4, -26.54) * mm});
            skLineSegment(sketch, "E1775", {"start": v(-8.4, -26.54) * mm, "end": v(-8.84, -26.07) * mm});
            skLineSegment(sketch, "E1776", {"start": v(-8.84, -26.07) * mm, "end": v(-9.18, -25.56) * mm});
            skLineSegment(sketch, "E1777", {"start": v(-9.18, -25.56) * mm, "end": v(-9.27, -25.3) * mm});
            skLineSegment(sketch, "E1778", {"start": v(-9.27, -25.3) * mm, "end": v(-9.27, -25.1) * mm});
            skLineSegment(sketch, "E1779", {"start": v(-9.27, -25.1) * mm, "end": v(-9.11, -24.82) * mm});
            skLineSegment(sketch, "E1780", {"start": v(-9.11, -24.82) * mm, "end": v(-8.86, -24.6) * mm});
            skLineSegment(sketch, "E1781", {"start": v(-8.86, -24.6) * mm, "end": v(-8.43, -24.35) * mm});
            skLineSegment(sketch, "E1782", {"start": v(-8.43, -24.35) * mm, "end": v(-7.64, -24) * mm});
            skLineSegment(sketch, "E1783", {"start": v(-7.64, -24) * mm, "end": v(-6.84, -23.8) * mm});
            skLineSegment(sketch, "E1784", {"start": v(-6.84, -23.8) * mm, "end": v(-6.32, -23.76) * mm});
            skLineSegment(sketch, "E1785", {"start": v(-6.32, -23.76) * mm, "end": v(-5.9, -23.8) * mm});
            skLineSegment(sketch, "E1786", {"start": v(-5.9, -23.8) * mm, "end": v(-5.45, -23.93) * mm});
            skLineSegment(sketch, "E1787", {"start": v(-5.45, -23.93) * mm, "end": v(-5, -24.13) * mm});
            skLineSegment(sketch, "E1788", {"start": v(-5, -24.13) * mm, "end": v(-4.44, -24.5) * mm});
            skLineSegment(sketch, "E1789", {"start": v(-4.44, -24.5) * mm, "end": v(-4.06, -24.87) * mm});
            skLineSegment(sketch, "E1790", {"start": v(-4.06, -24.87) * mm, "end": v(-3.85, -25.16) * mm});
            skLineSegment(sketch, "E1791", {"start": v(-3.85, -25.16) * mm, "end": v(-3.76, -25.44) * mm});
            skLineSegment(sketch, "E1792", {"start": v(-3.76, -25.44) * mm, "end": v(-3.77, -25.62) * mm});
            skLineSegment(sketch, "E1793", {"start": v(-3.77, -25.62) * mm, "end": v(-3.9, -25.87) * mm});
            skLineSegment(sketch, "E1794", {"start": v(-3.9, -25.87) * mm, "end": v(-4.13, -26.1) * mm});
            skLineSegment(sketch, "E1795", {"start": v(-4.13, -26.1) * mm, "end": v(-4.56, -26.36) * mm});
            skLineSegment(sketch, "E1796", {"start": v(-4.56, -26.36) * mm, "end": v(-5.31, -26.72) * mm});
            skLineSegment(sketch, "E1797", {"start": v(-5.31, -26.72) * mm, "end": v(-5.92, -26.96) * mm});
            skLineSegment(sketch, "E1798", {"start": v(-5.92, -26.96) * mm, "end": v(-6.68, -27.17) * mm});
            skLineSegment(sketch, "E1799", {"start": v(0.59, -21.92) * mm, "end": v(2.11, -21.6) * mm});
            skLineSegment(sketch, "E1800", {"start": v(2.11, -21.6) * mm, "end": v(3.43, -21.21) * mm});
            skLineSegment(sketch, "E1801", {"start": v(3.43, -21.21) * mm, "end": v(4.35, -20.96) * mm});
            skLineSegment(sketch, "E1802", {"start": v(4.35, -20.96) * mm, "end": v(4.78, -20.9) * mm});
            skLineSegment(sketch, "E1803", {"start": v(4.78, -20.9) * mm, "end": v(4.92, -20.93) * mm});
            skLineSegment(sketch, "E1804", {"start": v(4.92, -20.93) * mm, "end": v(4.94, -21.03) * mm});
            skLineSegment(sketch, "E1805", {"start": v(4.94, -21.03) * mm, "end": v(4.8, -21.26) * mm});
            skLineSegment(sketch, "E1806", {"start": v(4.8, -21.26) * mm, "end": v(4.29, -21.76) * mm});
            skLineSegment(sketch, "E1807", {"start": v(4.29, -21.76) * mm, "end": v(3.66, -22.26) * mm});
            skLineSegment(sketch, "E1808", {"start": v(3.66, -22.26) * mm, "end": v(2.8, -22.87) * mm});
            skLineSegment(sketch, "E1809", {"start": v(2.8, -22.87) * mm, "end": v(1.86, -23.46) * mm});
            skLineSegment(sketch, "E1810", {"start": v(1.86, -23.46) * mm, "end": v(1.29, -23.78) * mm});
            skLineSegment(sketch, "E1811", {"start": v(1.29, -23.78) * mm, "end": v(0.75, -24.05) * mm});
            skLineSegment(sketch, "E1812", {"start": v(0.75, -24.05) * mm, "end": v(0.12, -24.3) * mm});
            skLineSegment(sketch, "E1813", {"start": v(0.12, -24.3) * mm, "end": v(-0.3, -24.41) * mm});
            skLineSegment(sketch, "E1814", {"start": v(-0.3, -24.41) * mm, "end": v(-0.74, -24.44) * mm});
            skLineSegment(sketch, "E1815", {"start": v(-0.74, -24.44) * mm, "end": v(-1.12, -24.38) * mm});
            skLineSegment(sketch, "E1816", {"start": v(-1.12, -24.38) * mm, "end": v(-1.53, -24.18) * mm});
            skLineSegment(sketch, "E1817", {"start": v(-1.53, -24.18) * mm, "end": v(-1.97, -23.84) * mm});
            skLineSegment(sketch, "E1818", {"start": v(-1.97, -23.84) * mm, "end": v(-2.3, -23.45) * mm});
            skLineSegment(sketch, "E1819", {"start": v(-2.3, -23.45) * mm, "end": v(-2.47, -23.16) * mm});
            skLineSegment(sketch, "E1820", {"start": v(-2.47, -23.16) * mm, "end": v(-2.53, -22.92) * mm});
            skLineSegment(sketch, "E1821", {"start": v(-2.53, -22.92) * mm, "end": v(-2.5, -22.75) * mm});
            skLineSegment(sketch, "E1822", {"start": v(-2.5, -22.75) * mm, "end": v(-2.37, -22.6) * mm});
            skLineSegment(sketch, "E1823", {"start": v(-2.37, -22.6) * mm, "end": v(-2.15, -22.47) * mm});
            skLineSegment(sketch, "E1824", {"start": v(-2.15, -22.47) * mm, "end": v(-1.85, -22.34) * mm});
            skLineSegment(sketch, "E1825", {"start": v(-1.85, -22.34) * mm, "end": v(-1.25, -22.19) * mm});
            skLineSegment(sketch, "E1826", {"start": v(-1.25, -22.19) * mm, "end": v(0.59, -21.92) * mm});
            skSolve(sketch);
        }
        {
            var Q0;
            Q0=makeQuery(id+"F0.imprint","IMPRINT",FACE,{"disambiguationData":[TD([[makeQuery(id+"F0.imprint","IMPRINT",EDGE,{"derivedFrom":sQuery(id+"F0.wireOp",EDGE,"E0")}),1.0]])]});
            extrude(context, id + "F1", {"entities" : qUnion([Q0]), "depth" : 2.54 * mm});
        }
        {
            var Q0;
            Q0=qCreatedBy(makeId("Top.planeOp"),FACE);
            var sketch = newSketch(context, id + "F2", { "sketchPlane" : qUnion([Q0])});
            skLineSegment(sketch, "E1827.bottom", {"start": v(-34.93, 43.18) * mm, "end": v(34.93, 43.18) * mm});
            skLineSegment(sketch, "E1827.top", {"start": v(-34.93, -52.07) * mm, "end": v(34.93, -52.07) * mm});
            skLineSegment(sketch, "E1827.left", {"start": v(-34.93, 43.18) * mm, "end": v(-34.93, -52.07) * mm});
            skLineSegment(sketch, "E1827.right", {"start": v(34.93, 43.18) * mm, "end": v(34.93, -52.07) * mm});
            skLineSegment(sketch, "E1828", {"start": v(0, -52.07) * mm, "end": v(0, 43.18) * mm, "construction": true});
            skLineSegment(sketch, "E1829", {"start": v(-34.93, -4.44) * mm, "end": v(34.93, -4.44) * mm, "construction": true});
            skArc(sketch, "E1830", {"start": v(-2.54, 40) * mm, "mid": v(-5.08, 37.47) * mm, "end": v(-2.54, 34.93) * mm});
            skArc(sketch, "E1831", {"start": v(2.54, 34.93) * mm, "mid": v(5.08, 37.47) * mm, "end": v(2.54, 40) * mm});
            skLineSegment(sketch, "E1832", {"start": v(-2.54, 37.47) * mm, "end": v(2.54, 37.47) * mm, "construction": true});
            skLineSegment(sketch, "E1833.0", {"start": v(-2.54, 40) * mm, "end": v(2.54, 40) * mm});
            skLineSegment(sketch, "E1834.0", {"start": v(-2.54, 34.93) * mm, "end": v(2.54, 34.93) * mm});
            skLineSegment(sketch, "E1835", {"start": v(0, 40) * mm, "end": v(0, 34.93) * mm, "construction": true});
            skSolve(sketch);
        }
        {
            var Q0;
            Q0=makeQuery(id+"F2.imprint","IMPRINT",FACE,{"disambiguationData":[TD([[makeQuery(id+"F2.imprint","IMPRINT",EDGE,{"derivedFrom":sQuery(id+"F2.wireOp",EDGE,"E1827.bottom")}),-1.0]])]});
            extrude(context, id + "F3", {"entities" : qUnion([Q0]), "operationType" : NewBodyOperationType.ADD, "oppositeDirection" : true, "depth" : 2.54 * mm});
        }
        {
            var Q0;
            Q0=makeQuery(id+"F3.opExtrude","SWEPT_EDGE",EDGE,{"disambiguationData":[OSD([sQuery(id+"F2.wireOp",EDGE,"E1827.bottom"),sQuery(id+"F2.wireOp",EDGE,"E1827.right")])]});
            var Q1;
            Q1=makeQuery(id+"F3.opExtrude","SWEPT_EDGE",EDGE,{"disambiguationData":[OSD([sQuery(id+"F2.wireOp",EDGE,"E1827.bottom"),sQuery(id+"F2.wireOp",EDGE,"E1827.left")])]});
            var Q2;
            Q2=makeQuery(id+"F3.opExtrude","SWEPT_EDGE",EDGE,{"disambiguationData":[OSD([sQuery(id+"F2.wireOp",EDGE,"E1827.top"),sQuery(id+"F2.wireOp",EDGE,"E1827.left")])]});
            var Q3;
            Q3=makeQuery(id+"F3.opExtrude","SWEPT_EDGE",EDGE,{"disambiguationData":[OSD([sQuery(id+"F2.wireOp",EDGE,"E1827.top"),sQuery(id+"F2.wireOp",EDGE,"E1827.right")])]});
            fillet(context, id + "F4", {"entities" : qUnion([Q0, Q1, Q2, Q3]), "radius" : 9.52 * mm, "tangentPropagation" : true, "allowEdgeOverflow" : false});
        }
        {
            var Q0;
            Q0=makeQuery(id+"F2.imprint","IMPRINT",FACE,{"disambiguationData":[TD([[makeQuery(id+"F2.imprint","IMPRINT",EDGE,{"derivedFrom":sQuery(id+"F2.wireOp",EDGE,"E1827.bottom")}),-1.0]])]});
            var sketch = newSketch(context, id + "F5", { "sketchPlane" : qUnion([Q0])});
            skLineSegment(sketch, "E1836", {"start": v(-4.07, -36.16) * mm, "end": v(-4.07, -46) * mm});
            skLineSegment(sketch, "E1837", {"start": v(-4.07, -46) * mm, "end": v(-2.8, -46) * mm});
            skLineSegment(sketch, "E1838", {"start": v(-2.8, -46) * mm, "end": v(-2.8, -48.86) * mm});
            skLineSegment(sketch, "E1839", {"start": v(-2.8, -48.86) * mm, "end": v(-9.15, -48.86) * mm});
            skLineSegment(sketch, "E1840", {"start": v(-9.15, -48.86) * mm, "end": v(-9.15, -46) * mm});
            skLineSegment(sketch, "E1841", {"start": v(-9.15, -46) * mm, "end": v(-7.56, -46) * mm});
            skLineSegment(sketch, "E1842", {"start": v(-7.56, -46) * mm, "end": v(-7.56, -40.53) * mm});
            skLineSegment(sketch, "E1843", {"start": v(-7.56, -40.53) * mm, "end": v(-9.15, -40.53) * mm});
            skLineSegment(sketch, "E1844", {"start": v(-9.15, -40.53) * mm, "end": v(-9.15, -38.52) * mm});
            skLineSegment(sketch, "E1845", {"start": v(-9.15, -38.52) * mm, "end": v(-6.8, -36.16) * mm});
            skLineSegment(sketch, "E1846", {"start": v(-6.8, -36.16) * mm, "end": v(-4.07, -36.16) * mm});
            skLineSegment(sketch, "E1847", {"start": v(-4.36, -36.47) * mm, "end": v(-4.36, -46.32) * mm});
            skLineSegment(sketch, "E1848", {"start": v(-4.36, -46.32) * mm, "end": v(-3.1, -46.32) * mm});
            skLineSegment(sketch, "E1849", {"start": v(-3.1, -46.32) * mm, "end": v(-3.1, -48.55) * mm});
            skLineSegment(sketch, "E1850", {"start": v(-3.1, -48.55) * mm, "end": v(-8.84, -48.55) * mm});
            skLineSegment(sketch, "E1851", {"start": v(-8.84, -48.55) * mm, "end": v(-8.84, -46.32) * mm});
            skLineSegment(sketch, "E1852", {"start": v(-8.84, -46.32) * mm, "end": v(-7.25, -46.32) * mm});
            skLineSegment(sketch, "E1853", {"start": v(-7.25, -46.32) * mm, "end": v(-7.25, -40.22) * mm});
            skLineSegment(sketch, "E1854", {"start": v(-7.25, -40.22) * mm, "end": v(-8.84, -40.22) * mm});
            skLineSegment(sketch, "E1855", {"start": v(-8.84, -40.22) * mm, "end": v(-8.84, -38.65) * mm});
            skLineSegment(sketch, "E1856", {"start": v(-8.84, -38.65) * mm, "end": v(-6.67, -36.47) * mm});
            skLineSegment(sketch, "E1857", {"start": v(-6.67, -36.47) * mm, "end": v(-4.36, -36.47) * mm});
            skLineSegment(sketch, "E1858", {"start": v(-4.76, -36.86) * mm, "end": v(-4.76, -46.72) * mm});
            skLineSegment(sketch, "E1859", {"start": v(-4.76, -46.72) * mm, "end": v(-3.49, -46.72) * mm});
            skLineSegment(sketch, "E1860", {"start": v(-3.49, -46.72) * mm, "end": v(-3.49, -48.15) * mm});
            skLineSegment(sketch, "E1861", {"start": v(-3.49, -48.15) * mm, "end": v(-8.45, -48.15) * mm});
            skLineSegment(sketch, "E1862", {"start": v(-8.45, -48.15) * mm, "end": v(-8.45, -46.72) * mm});
            skLineSegment(sketch, "E1863", {"start": v(-8.45, -46.72) * mm, "end": v(-6.85, -46.72) * mm});
            skLineSegment(sketch, "E1864", {"start": v(-6.85, -46.72) * mm, "end": v(-6.85, -39.83) * mm});
            skLineSegment(sketch, "E1865", {"start": v(-6.85, -39.83) * mm, "end": v(-8.45, -39.83) * mm});
            skLineSegment(sketch, "E1866", {"start": v(-8.45, -39.83) * mm, "end": v(-8.45, -38.8) * mm});
            skLineSegment(sketch, "E1867", {"start": v(-8.45, -38.8) * mm, "end": v(-6.5, -36.86) * mm});
            skLineSegment(sketch, "E1868", {"start": v(-6.5, -36.86) * mm, "end": v(-4.76, -36.86) * mm});
            skLineSegment(sketch, "E1869", {"start": v(1.62, -36.07) * mm, "end": v(7.2, -36.07) * mm});
            skLineSegment(sketch, "E1870", {"start": v(7.2, -36.07) * mm, "end": v(9.24, -38.11) * mm});
            skLineSegment(sketch, "E1871", {"start": v(9.24, -38.11) * mm, "end": v(9.24, -46.75) * mm});
            skLineSegment(sketch, "E1872", {"start": v(9.24, -46.75) * mm, "end": v(7.13, -48.86) * mm});
            skLineSegment(sketch, "E1873", {"start": v(7.13, -48.86) * mm, "end": v(1.6, -48.86) * mm});
            skLineSegment(sketch, "E1874", {"start": v(1.6, -48.86) * mm, "end": v(-0.45, -46.79) * mm});
            skLineSegment(sketch, "E1875", {"start": v(-0.45, -46.79) * mm, "end": v(-0.45, -44.7) * mm});
            skLineSegment(sketch, "E1876", {"start": v(-0.45, -44.7) * mm, "end": v(3.04, -44.7) * mm});
            skLineSegment(sketch, "E1877", {"start": v(3.04, -44.7) * mm, "end": v(3.04, -45.54) * mm});
            skLineSegment(sketch, "E1878", {"start": v(3.04, -45.54) * mm, "end": v(3.44, -45.95) * mm});
            skLineSegment(sketch, "E1879", {"start": v(3.44, -45.95) * mm, "end": v(5.33, -45.95) * mm});
            skLineSegment(sketch, "E1880", {"start": v(5.33, -45.95) * mm, "end": v(5.7, -45.57) * mm});
            skLineSegment(sketch, "E1881", {"start": v(5.7, -45.57) * mm, "end": v(5.7, -43.74) * mm});
            skLineSegment(sketch, "E1882", {"start": v(5.7, -43.74) * mm, "end": v(1.6, -43.74) * mm});
            skLineSegment(sketch, "E1883", {"start": v(1.6, -43.74) * mm, "end": v(-0.44, -41.7) * mm});
            skLineSegment(sketch, "E1884", {"start": v(-0.44, -41.7) * mm, "end": v(-0.44, -38.14) * mm});
            skLineSegment(sketch, "E1885", {"start": v(-0.44, -38.14) * mm, "end": v(1.62, -36.07) * mm});
            skLineSegment(sketch, "E1886", {"start": v(1.77, -36.43) * mm, "end": v(7.05, -36.43) * mm});
            skLineSegment(sketch, "E1887", {"start": v(7.05, -36.43) * mm, "end": v(8.89, -38.26) * mm});
            skLineSegment(sketch, "E1888", {"start": v(8.89, -38.26) * mm, "end": v(8.89, -46.6) * mm});
            skLineSegment(sketch, "E1889", {"start": v(8.89, -46.6) * mm, "end": v(6.99, -48.5) * mm});
            skLineSegment(sketch, "E1890", {"start": v(6.99, -48.5) * mm, "end": v(1.74, -48.5) * mm});
            skLineSegment(sketch, "E1891", {"start": v(1.74, -48.5) * mm, "end": v(-0.1, -46.64) * mm});
            skLineSegment(sketch, "E1892", {"start": v(-0.1, -46.64) * mm, "end": v(-0.1, -45.06) * mm});
            skLineSegment(sketch, "E1893", {"start": v(-0.1, -45.06) * mm, "end": v(2.68, -45.06) * mm});
            skLineSegment(sketch, "E1894", {"start": v(2.68, -45.06) * mm, "end": v(2.68, -45.68) * mm});
            skLineSegment(sketch, "E1895", {"start": v(2.68, -45.68) * mm, "end": v(3.29, -46.3) * mm});
            skLineSegment(sketch, "E1896", {"start": v(3.29, -46.3) * mm, "end": v(5.48, -46.3) * mm});
            skLineSegment(sketch, "E1897", {"start": v(5.48, -46.3) * mm, "end": v(6.06, -45.71) * mm});
            skLineSegment(sketch, "E1898", {"start": v(6.06, -45.71) * mm, "end": v(6.06, -43.38) * mm});
            skLineSegment(sketch, "E1899", {"start": v(6.06, -43.38) * mm, "end": v(1.74, -43.38) * mm});
            skLineSegment(sketch, "E1900", {"start": v(1.74, -43.38) * mm, "end": v(-0.1, -41.55) * mm});
            skLineSegment(sketch, "E1901", {"start": v(-0.1, -41.55) * mm, "end": v(-0.1, -38.29) * mm});
            skLineSegment(sketch, "E1902", {"start": v(-0.1, -38.29) * mm, "end": v(1.77, -36.43) * mm});
            skLineSegment(sketch, "E1903", {"start": v(1.91, -36.78) * mm, "end": v(6.9, -36.78) * mm});
            skLineSegment(sketch, "E1904", {"start": v(6.9, -36.78) * mm, "end": v(8.53, -38.4) * mm});
            skLineSegment(sketch, "E1905", {"start": v(8.53, -38.4) * mm, "end": v(8.53, -46.46) * mm});
            skLineSegment(sketch, "E1906", {"start": v(8.53, -46.46) * mm, "end": v(6.84, -48.15) * mm});
            skLineSegment(sketch, "E1907", {"start": v(6.84, -48.15) * mm, "end": v(1.89, -48.15) * mm});
            skLineSegment(sketch, "E1908", {"start": v(1.89, -48.15) * mm, "end": v(0.26, -46.5) * mm});
            skLineSegment(sketch, "E1909", {"start": v(0.26, -46.5) * mm, "end": v(0.26, -45.41) * mm});
            skLineSegment(sketch, "E1910", {"start": v(0.26, -45.41) * mm, "end": v(2.33, -45.41) * mm});
            skLineSegment(sketch, "E1911", {"start": v(2.33, -45.41) * mm, "end": v(2.33, -45.82) * mm});
            skLineSegment(sketch, "E1912", {"start": v(2.33, -45.82) * mm, "end": v(3.14, -46.66) * mm});
            skLineSegment(sketch, "E1913", {"start": v(3.14, -46.66) * mm, "end": v(5.62, -46.66) * mm});
            skLineSegment(sketch, "E1914", {"start": v(5.62, -46.66) * mm, "end": v(6.4, -45.86) * mm});
            skLineSegment(sketch, "E1915", {"start": v(6.4, -45.86) * mm, "end": v(6.4, -43.03) * mm});
            skLineSegment(sketch, "E1916", {"start": v(6.4, -43.03) * mm, "end": v(1.89, -43.03) * mm});
            skLineSegment(sketch, "E1917", {"start": v(1.89, -43.03) * mm, "end": v(0.26, -41.4) * mm});
            skLineSegment(sketch, "E1918", {"start": v(0.26, -41.4) * mm, "end": v(0.26, -38.44) * mm});
            skLineSegment(sketch, "E1919", {"start": v(0.26, -38.44) * mm, "end": v(1.91, -36.78) * mm});
            skLineSegment(sketch, "E1920", {"start": v(3.13, -38.3) * mm, "end": v(5.62, -38.3) * mm});
            skLineSegment(sketch, "E1921", {"start": v(5.62, -38.3) * mm, "end": v(6.42, -39.05) * mm});
            skLineSegment(sketch, "E1922", {"start": v(6.42, -39.05) * mm, "end": v(6.42, -40.78) * mm});
            skLineSegment(sketch, "E1923", {"start": v(6.42, -40.78) * mm, "end": v(5.62, -41.57) * mm});
            skLineSegment(sketch, "E1924", {"start": v(5.62, -41.57) * mm, "end": v(3.13, -41.57) * mm});
            skLineSegment(sketch, "E1925", {"start": v(3.13, -41.57) * mm, "end": v(2.35, -40.8) * mm});
            skLineSegment(sketch, "E1926", {"start": v(2.35, -40.8) * mm, "end": v(2.35, -39.05) * mm});
            skLineSegment(sketch, "E1927", {"start": v(2.35, -39.05) * mm, "end": v(3.13, -38.3) * mm});
            skLineSegment(sketch, "E1928", {"start": v(3.29, -38.67) * mm, "end": v(5.47, -38.67) * mm});
            skLineSegment(sketch, "E1929", {"start": v(5.47, -38.67) * mm, "end": v(6.04, -39.21) * mm});
            skLineSegment(sketch, "E1930", {"start": v(6.04, -39.21) * mm, "end": v(6.04, -40.62) * mm});
            skLineSegment(sketch, "E1931", {"start": v(6.04, -40.62) * mm, "end": v(5.46, -41.2) * mm});
            skLineSegment(sketch, "E1932", {"start": v(5.46, -41.2) * mm, "end": v(3.29, -41.2) * mm});
            skLineSegment(sketch, "E1933", {"start": v(3.29, -41.2) * mm, "end": v(2.73, -40.64) * mm});
            skLineSegment(sketch, "E1934", {"start": v(2.73, -40.64) * mm, "end": v(2.73, -39.2) * mm});
            skLineSegment(sketch, "E1935", {"start": v(2.73, -39.2) * mm, "end": v(3.29, -38.67) * mm});
            skLineSegment(sketch, "E1936", {"start": v(3.44, -39.04) * mm, "end": v(5.32, -39.04) * mm});
            skLineSegment(sketch, "E1937", {"start": v(5.32, -39.04) * mm, "end": v(5.67, -39.37) * mm});
            skLineSegment(sketch, "E1938", {"start": v(5.67, -39.37) * mm, "end": v(5.67, -40.47) * mm});
            skLineSegment(sketch, "E1939", {"start": v(5.67, -40.47) * mm, "end": v(5.3, -40.83) * mm});
            skLineSegment(sketch, "E1940", {"start": v(5.3, -40.83) * mm, "end": v(3.44, -40.83) * mm});
            skLineSegment(sketch, "E1941", {"start": v(3.44, -40.83) * mm, "end": v(3.1, -40.48) * mm});
            skLineSegment(sketch, "E1942", {"start": v(3.1, -40.48) * mm, "end": v(3.1, -39.37) * mm});
            skLineSegment(sketch, "E1943", {"start": v(3.1, -39.37) * mm, "end": v(3.44, -39.04) * mm});
            skSolve(sketch);
        }
        {
            var Q0;
            Q0 = qSketchRegion(id + "F5", true);
            var Q1;
            Q1=makeQuery(id+"F5.imprint","IMPRINT",FACE,{"disambiguationData":[TD([[makeQuery(id+"F5.imprint","IMPRINT",EDGE,{"derivedFrom":sQuery(id+"F5.wireOp",EDGE,"E1858")}),-1.0]])]});
            var Q2;
            Q2=makeQuery(id+"F5.imprint","IMPRINT",FACE,{"disambiguationData":[TD([[makeQuery(id+"F5.imprint","IMPRINT",EDGE,{"derivedFrom":sQuery(id+"F5.wireOp",EDGE,"E1903")}),-1.0]])]});
            var Q3;
            Q3=makeQuery(id+"F5.imprint","IMPRINT",FACE,{"disambiguationData":[TD([[makeQuery(id+"F5.imprint","IMPRINT",EDGE,{"derivedFrom":sQuery(id+"F5.wireOp",EDGE,"E1928")}),-1.0]])]});
            var Q4;
            Q4=makeQuery(id+"F5.imprint","IMPRINT",FACE,{"disambiguationData":[TD([[makeQuery(id+"F5.imprint","IMPRINT",EDGE,{"derivedFrom":sQuery(id+"F5.wireOp",EDGE,"E1886")}),-1.0]])]});
            var Q5;
            Q5=makeQuery(id+"F5.imprint","IMPRINT",FACE,{"disambiguationData":[TD([[makeQuery(id+"F5.imprint","IMPRINT",EDGE,{"derivedFrom":sQuery(id+"F5.wireOp",EDGE,"E1847")}),-1.0]])]});
            var Q6;
            Q6=makeQuery(id+"F5.imprint","IMPRINT",FACE,{"disambiguationData":[TD([[makeQuery(id+"F5.imprint","IMPRINT",EDGE,{"derivedFrom":sQuery(id+"F5.wireOp",EDGE,"E1920")}),-1.0]])]});
            extrude(context, id + "F6", {"entities" : qUnion([Q0, Q1, Q2, Q3, Q4, Q5, Q6]), "operationType" : NewBodyOperationType.ADD, "depth" : 2.54 * mm});
        }
    });
